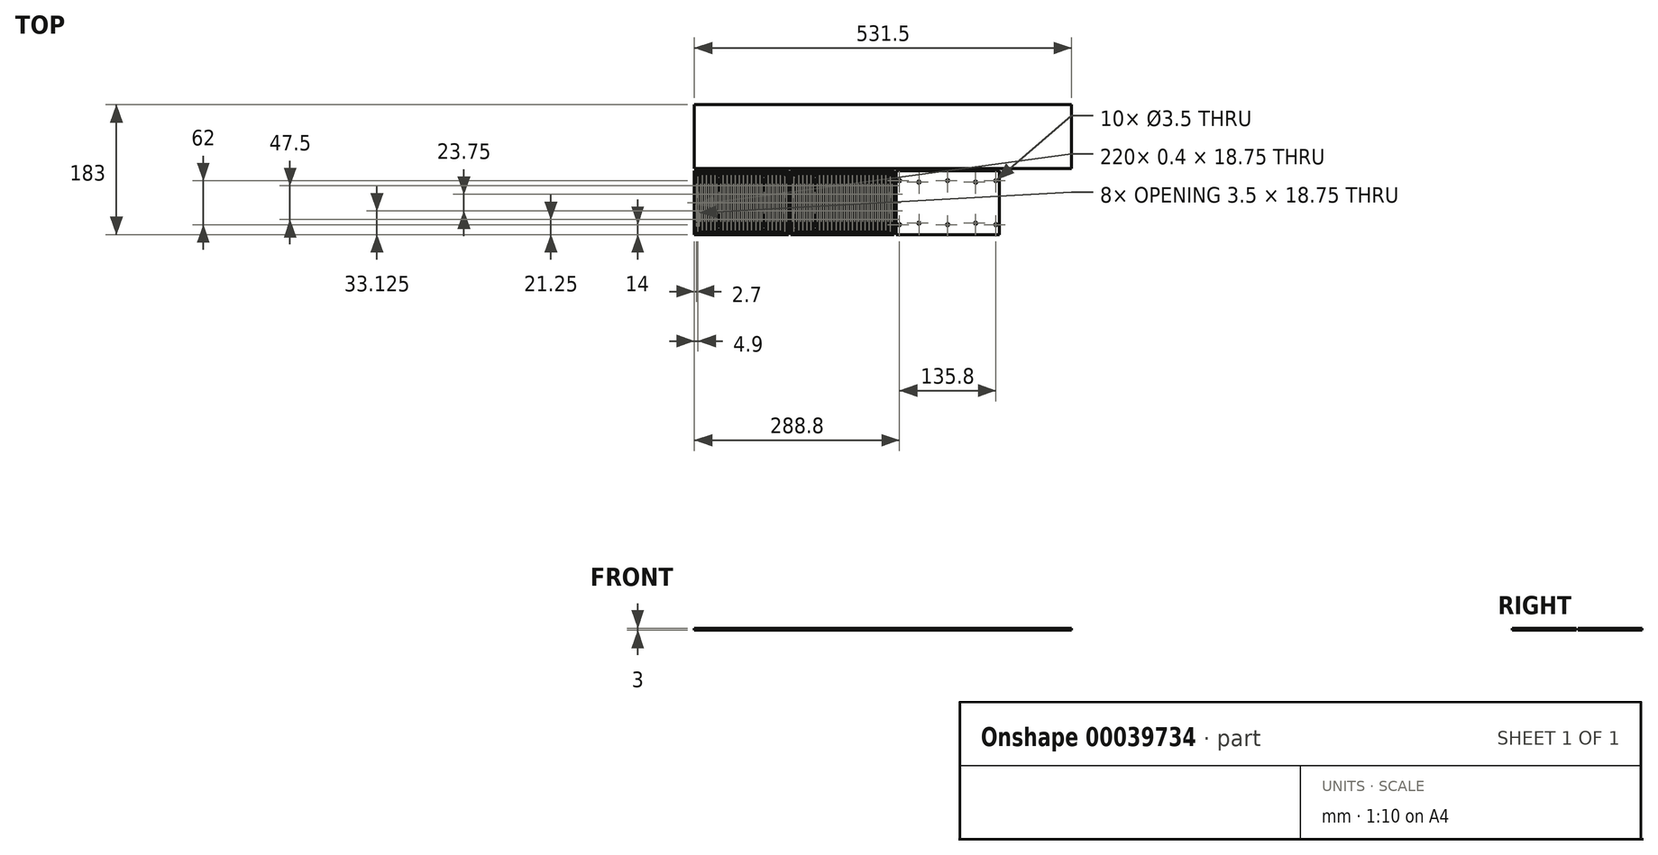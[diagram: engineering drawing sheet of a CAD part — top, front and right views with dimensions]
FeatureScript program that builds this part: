
annotation { "Feature Type Name" : "Feature", "Feature Type Description" : "" }
export const myFeature = defineFeature(function(context is Context, id is Id, definition is map)
    precondition{}
    {
        {
            var Q0;
            Q0=qCreatedBy(makeId("Top.planeOp"),FACE);
            var sketch = newSketch(context, id + "F0", { "sketchPlane" : qUnion([Q0])});
            skLineSegment(sketch, "E0.bottom", {"start": v(0, 0) * mm, "end": v(531.5, 0) * mm});
            skLineSegment(sketch, "E0.top", {"start": v(0, -90) * mm, "end": v(531.5, -90) * mm});
            skLineSegment(sketch, "E0.left", {"start": v(0, 0) * mm, "end": v(0, -90) * mm});
            skLineSegment(sketch, "E0.right", {"start": v(531.5, 0) * mm, "end": v(531.5, -90) * mm});
            skLineSegment(sketch, "E1.bottom", {"start": v(0, -93) * mm, "end": v(132.3, -93) * mm});
            skLineSegment(sketch, "E1.top", {"start": v(0, -183) * mm, "end": v(132.3, -183) * mm});
            skLineSegment(sketch, "E1.left", {"start": v(0, -93) * mm, "end": v(0, -183) * mm});
            skLineSegment(sketch, "E1.right", {"start": v(132.3, -93) * mm, "end": v(132.3, -183) * mm});
            skLineSegment(sketch, "E2.bottom", {"start": v(135.3, -93) * mm, "end": v(280.9, -93) * mm});
            skLineSegment(sketch, "E2.top", {"start": v(135.3, -183) * mm, "end": v(280.9, -183) * mm});
            skLineSegment(sketch, "E2.left", {"start": v(135.3, -93) * mm, "end": v(135.3, -183) * mm});
            skLineSegment(sketch, "E2.right", {"start": v(280.9, -93) * mm, "end": v(280.9, -183) * mm});
            skLineSegment(sketch, "E3", {"start": v(282.4, -93) * mm, "end": v(282.4, -183) * mm, "construction": true});
            skLineSegment(sketch, "E4.bottom", {"start": v(32.85, -109) * mm, "end": v(99.45, -109) * mm, "construction": true});
            skLineSegment(sketch, "E4.top", {"start": v(32.85, -167) * mm, "end": v(99.45, -167) * mm, "construction": true});
            skLineSegment(sketch, "E4.left", {"start": v(32.85, -109) * mm, "end": v(32.85, -167) * mm, "construction": true});
            skLineSegment(sketch, "E4.right", {"start": v(99.45, -109) * mm, "end": v(99.45, -167) * mm, "construction": true});
            skLineSegment(sketch, "E5.bottom", {"start": v(168.65, -109) * mm, "end": v(248.55, -109) * mm, "construction": true});
            skLineSegment(sketch, "E5.top", {"start": v(168.65, -167) * mm, "end": v(248.55, -167) * mm, "construction": true});
            skLineSegment(sketch, "E5.left", {"start": v(168.65, -109) * mm, "end": v(168.65, -167) * mm, "construction": true});
            skLineSegment(sketch, "E5.right", {"start": v(248.55, -109) * mm, "end": v(248.55, -167) * mm, "construction": true});
            skLineSegment(sketch, "E6", {"start": v(66.15, -93) * mm, "end": v(66.15, -183) * mm, "construction": true});
            skLineSegment(sketch, "E7", {"start": v(208.1, -93) * mm, "end": v(208.1, -183) * mm, "construction": true});
            skLineSegment(sketch, "E8", {"start": v(280.9, -138) * mm, "end": v(0, -138) * mm, "construction": true});
            skLineSegment(sketch, "E9.MirrorCS", {"start": v(283.9, -93) * mm, "end": v(283.9, -183) * mm});
            skLineSegment(sketch, "E10.MirrorCS", {"start": v(429.5, -93) * mm, "end": v(283.9, -93) * mm});
            skLineSegment(sketch, "E11.MirrorCS", {"start": v(429.5, -93) * mm, "end": v(429.5, -183) * mm});
            skLineSegment(sketch, "E12.MirrorCS", {"start": v(429.5, -183) * mm, "end": v(283.9, -183) * mm});
            skLineSegment(sketch, "E13.MirrorCS", {"start": v(396.15, -109) * mm, "end": v(316.25, -109) * mm, "construction": true});
            skLineSegment(sketch, "E14.MirrorCS", {"start": v(396.15, -109) * mm, "end": v(396.15, -167) * mm, "construction": true});
            skLineSegment(sketch, "E15.MirrorCS", {"start": v(396.15, -167) * mm, "end": v(316.25, -167) * mm, "construction": true});
            skLineSegment(sketch, "E16.MirrorCS", {"start": v(316.25, -109) * mm, "end": v(316.25, -167) * mm, "construction": true});
            skSolve(sketch);
        }
        {
            var Q0;
            Q0=makeQuery(id+"F0.imprint","IMPRINT",FACE,{"disambiguationData":[TD([[makeQuery(id+"F0.imprint","IMPRINT",EDGE,{"derivedFrom":sQuery(id+"F0.wireOp",EDGE,"E1.bottom")}),-1.0]])]});
            var Q1;
            Q1=makeQuery(id+"F0.imprint","IMPRINT",FACE,{"disambiguationData":[TD([[makeQuery(id+"F0.imprint","IMPRINT",EDGE,{"derivedFrom":sQuery(id+"F0.wireOp",EDGE,"E0.bottom")}),-1.0]])]});
            var Q2;
            Q2=makeQuery(id+"F0.imprint","IMPRINT",FACE,{"disambiguationData":[TD([[makeQuery(id+"F0.imprint","IMPRINT",EDGE,{"derivedFrom":sQuery(id+"F0.wireOp",EDGE,"E2.bottom")}),-1.0]])]});
            var Q3;
            Q3=makeQuery(id+"F0.imprint","IMPRINT",FACE,{"disambiguationData":[TD([[makeQuery(id+"F0.imprint","IMPRINT",EDGE,{"derivedFrom":sQuery(id+"F0.wireOp",EDGE,"E9.MirrorCS")}),1.0]])]});
            extrude(context, id + "F1", {"entities" : qUnion([Q0, Q1, Q2, Q3]), "depth" : 3 * mm});
        }
        {
            var Q0;
            Q0=makeQuery(id+"F1.opExtrude","CAP_FACE",FACE,{"disambiguationData":[OSD([sQuery(id+"F0.wireOp",EDGE,"E1.bottom"),sQuery(id+"F0.wireOp",EDGE,"E1.top"),sQuery(id+"F0.wireOp",EDGE,"E1.left"),sQuery(id+"F0.wireOp",EDGE,"E1.right")])],"isStart":false});
            var sketch = newSketch(context, id + "F2", { "sketchPlane" : qUnion([Q0])});
            skPoint(sketch, "E17.MirrorP", {"position": v(356.7, -183) * mm});
            skLineSegment(sketch, "E18.right", {"start": v(137.8, -183) * mm, "end": v(137.8, -93) * mm, "construction": true});
            skLineSegment(sketch, "E18.left", {"start": v(141.1, -183) * mm, "end": v(141.1, -93) * mm, "construction": true});
            skLineSegment(sketch, "E19.left", {"start": v(137.8, -164.25) * mm, "end": v(137.8, -183) * mm});
            skLineSegment(sketch, "E20.left", {"start": v(140.7, -176.12) * mm, "end": v(140.7, -183) * mm});
            skLineSegment(sketch, "E20.right", {"start": v(141.1, -176.12) * mm, "end": v(141.1, -183) * mm});
            skLineSegment(sketch, "E21.left", {"start": v(140.7, -152.37) * mm, "end": v(140.7, -171.12) * mm});
            skLineSegment(sketch, "E21.right", {"start": v(141.1, -152.37) * mm, "end": v(141.1, -171.12) * mm});
            skLineSegment(sketch, "E22.left", {"start": v(137.8, -140.5) * mm, "end": v(137.8, -159.25) * mm});
            skLineSegment(sketch, "E23.left", {"start": v(140.7, -128.62) * mm, "end": v(140.7, -147.37) * mm});
            skLineSegment(sketch, "E23.right", {"start": v(141.1, -128.62) * mm, "end": v(141.1, -147.37) * mm});
            skLineSegment(sketch, "E24.left", {"start": v(137.8, -116.75) * mm, "end": v(137.8, -135.5) * mm});
            skLineSegment(sketch, "E25.left", {"start": v(140.7, -104.87) * mm, "end": v(140.7, -123.62) * mm});
            skLineSegment(sketch, "E25.right", {"start": v(141.1, -104.87) * mm, "end": v(141.1, -123.62) * mm});
            skLineSegment(sketch, "E26.right", {"start": v(138.2, -93) * mm, "end": v(138.2, -111.75) * mm});
            skLineSegment(sketch, "E26.left", {"start": v(137.8, -93) * mm, "end": v(137.8, -111.75) * mm});
            skLineSegment(sketch, "E27.left", {"start": v(140.7, -99.87) * mm, "end": v(140.7, -93) * mm});
            skLineSegment(sketch, "E27.right", {"start": v(141.1, -99.87) * mm, "end": v(141.1, -93) * mm});
            skLineSegment(sketch, "E20.bottom", {"start": v(140.7, -176.12) * mm, "end": v(141.1, -176.12) * mm});
            skLineSegment(sketch, "E21.top", {"start": v(140.7, -171.12) * mm, "end": v(141.1, -171.12) * mm});
            skLineSegment(sketch, "E21.bottom", {"start": v(140.7, -152.37) * mm, "end": v(141.1, -152.37) * mm});
            skLineSegment(sketch, "E23.top", {"start": v(140.7, -147.37) * mm, "end": v(141.1, -147.37) * mm});
            skLineSegment(sketch, "E23.bottom", {"start": v(140.7, -128.62) * mm, "end": v(141.1, -128.62) * mm});
            skLineSegment(sketch, "E25.top", {"start": v(140.7, -123.62) * mm, "end": v(141.1, -123.62) * mm});
            skLineSegment(sketch, "E25.bottom", {"start": v(140.7, -104.87) * mm, "end": v(141.1, -104.87) * mm});
            skLineSegment(sketch, "E27.bottom", {"start": v(140.7, -99.87) * mm, "end": v(141.1, -99.87) * mm});
            skLineSegment(sketch, "E18.top", {"start": v(141.1, -93) * mm, "end": v(137.8, -93) * mm, "construction": true});
            skLineSegment(sketch, "E27.top", {"start": v(140.7, -93) * mm, "end": v(141.1, -93) * mm});
            skLineSegment(sketch, "E18.bottom", {"start": v(141.1, -183) * mm, "end": v(137.8, -183) * mm, "construction": true});
            skLineSegment(sketch, "E20.top", {"start": v(140.7, -183) * mm, "end": v(141.1, -183) * mm});
            skLineSegment(sketch, "E28", {"start": v(137.8, -111.75) * mm, "end": v(138.2, -111.75) * mm});
            skLineSegment(sketch, "E29.bottom", {"start": v(137.8, -116.75) * mm, "end": v(138.2, -116.75) * mm});
            skLineSegment(sketch, "E29.top", {"start": v(137.8, -135.5) * mm, "end": v(138.2, -135.5) * mm});
            skLineSegment(sketch, "E29.right", {"start": v(138.2, -116.75) * mm, "end": v(138.2, -135.5) * mm});
            skLineSegment(sketch, "E30.bottom", {"start": v(137.8, -159.25) * mm, "end": v(138.2, -159.25) * mm});
            skLineSegment(sketch, "E30.top", {"start": v(137.8, -140.5) * mm, "end": v(138.2, -140.5) * mm});
            skLineSegment(sketch, "E30.left", {"start": v(137.8, -159.25) * mm, "end": v(137.8, -140.5) * mm});
            skLineSegment(sketch, "E30.right", {"start": v(138.2, -159.25) * mm, "end": v(138.2, -140.5) * mm});
            skLineSegment(sketch, "E31.bottom", {"start": v(137.8, -164.25) * mm, "end": v(138.2, -164.25) * mm});
            skLineSegment(sketch, "E31.top", {"start": v(137.8, -183) * mm, "end": v(138.2, -183) * mm});
            skLineSegment(sketch, "E31.right", {"start": v(138.2, -164.25) * mm, "end": v(138.2, -183) * mm});
            skLineSegment(sketch, "E32.bottom", {"start": v(138.2, -111.75) * mm, "end": v(137.8, -111.75) * mm});
            skLineSegment(sketch, "E32.top", {"start": v(138.2, -93) * mm, "end": v(137.8, -93) * mm});
            skLineSegment(sketch, "E32.left", {"start": v(138.2, -111.75) * mm, "end": v(138.2, -93) * mm});
            skLineSegment(sketch, "E32.right", {"start": v(137.8, -111.75) * mm, "end": v(137.8, -93) * mm});
            skLineSegment(sketch, "E33.1.0.0", {"start": v(146.55, -99.87) * mm, "end": v(146.55, -93) * mm});
            skLineSegment(sketch, "E33.1.0.1", {"start": v(143.65, -183) * mm, "end": v(143.65, -93) * mm, "construction": true});
            skLineSegment(sketch, "E33.1.0.2", {"start": v(146.95, -152.37) * mm, "end": v(146.95, -171.12) * mm});
            skLineSegment(sketch, "E33.1.0.3", {"start": v(146.55, -104.87) * mm, "end": v(146.55, -123.62) * mm});
            skLineSegment(sketch, "E33.1.0.4", {"start": v(144.05, -159.25) * mm, "end": v(144.05, -140.5) * mm});
            skLineSegment(sketch, "E33.1.0.5", {"start": v(146.95, -128.62) * mm, "end": v(146.95, -147.37) * mm});
            skLineSegment(sketch, "E33.1.0.6", {"start": v(146.55, -128.62) * mm, "end": v(146.55, -147.37) * mm});
            skLineSegment(sketch, "E33.1.0.7", {"start": v(143.65, -164.25) * mm, "end": v(143.65, -183) * mm});
            skLineSegment(sketch, "E33.1.0.8", {"start": v(144.05, -164.25) * mm, "end": v(144.05, -183) * mm});
            skLineSegment(sketch, "E33.1.0.9", {"start": v(146.55, -176.12) * mm, "end": v(146.55, -183) * mm});
            skLineSegment(sketch, "E33.1.0.10", {"start": v(146.95, -176.12) * mm, "end": v(146.95, -183) * mm});
            skLineSegment(sketch, "E33.1.0.11", {"start": v(146.95, -183) * mm, "end": v(146.95, -93) * mm, "construction": true});
            skLineSegment(sketch, "E33.1.0.12", {"start": v(146.55, -152.37) * mm, "end": v(146.55, -171.12) * mm});
            skLineSegment(sketch, "E33.1.0.13", {"start": v(143.65, -140.5) * mm, "end": v(143.65, -159.25) * mm});
            skLineSegment(sketch, "E33.1.0.14", {"start": v(143.65, -116.75) * mm, "end": v(143.65, -135.5) * mm});
            skLineSegment(sketch, "E33.1.0.15", {"start": v(144.05, -116.75) * mm, "end": v(144.05, -135.5) * mm});
            skLineSegment(sketch, "E33.1.0.16", {"start": v(146.95, -104.87) * mm, "end": v(146.95, -123.62) * mm});
            skLineSegment(sketch, "E33.1.0.17", {"start": v(143.65, -93) * mm, "end": v(143.65, -111.75) * mm});
            skLineSegment(sketch, "E33.1.0.18", {"start": v(144.05, -93) * mm, "end": v(144.05, -111.75) * mm});
            skLineSegment(sketch, "E33.1.0.19", {"start": v(146.95, -99.87) * mm, "end": v(146.95, -93) * mm});
            skLineSegment(sketch, "E33.1.0.20", {"start": v(143.65, -159.25) * mm, "end": v(143.65, -140.5) * mm});
            skLineSegment(sketch, "E33.1.0.21", {"start": v(143.65, -116.75) * mm, "end": v(143.65, -135.5) * mm});
            skLineSegment(sketch, "E33.1.0.22", {"start": v(144.05, -111.75) * mm, "end": v(144.05, -93) * mm});
            skLineSegment(sketch, "E33.1.0.23", {"start": v(143.65, -164.25) * mm, "end": v(143.65, -183) * mm});
            skLineSegment(sketch, "E33.1.0.24", {"start": v(143.65, -111.75) * mm, "end": v(143.65, -93) * mm});
            skLineSegment(sketch, "E33.1.0.25", {"start": v(146.55, -176.12) * mm, "end": v(146.95, -176.12) * mm});
            skLineSegment(sketch, "E33.1.0.26", {"start": v(146.55, -171.12) * mm, "end": v(146.95, -171.12) * mm});
            skLineSegment(sketch, "E33.1.0.27", {"start": v(146.55, -152.37) * mm, "end": v(146.95, -152.37) * mm});
            skLineSegment(sketch, "E33.1.0.28", {"start": v(146.55, -147.37) * mm, "end": v(146.95, -147.37) * mm});
            skLineSegment(sketch, "E33.1.0.29", {"start": v(146.55, -128.62) * mm, "end": v(146.95, -128.62) * mm});
            skLineSegment(sketch, "E33.1.0.30", {"start": v(146.55, -123.62) * mm, "end": v(146.95, -123.62) * mm});
            skLineSegment(sketch, "E33.1.0.31", {"start": v(146.55, -104.87) * mm, "end": v(146.95, -104.87) * mm});
            skLineSegment(sketch, "E33.1.0.32", {"start": v(146.55, -99.87) * mm, "end": v(146.95, -99.87) * mm});
            skLineSegment(sketch, "E33.1.0.33", {"start": v(143.65, -164.25) * mm, "end": v(144.05, -164.25) * mm});
            skLineSegment(sketch, "E33.1.0.34", {"start": v(143.65, -159.25) * mm, "end": v(144.05, -159.25) * mm});
            skLineSegment(sketch, "E33.1.0.35", {"start": v(146.95, -93) * mm, "end": v(143.65, -93) * mm, "construction": true});
            skLineSegment(sketch, "E33.1.0.36", {"start": v(143.65, -140.5) * mm, "end": v(144.05, -140.5) * mm});
            skLineSegment(sketch, "E33.1.0.37", {"start": v(143.65, -135.5) * mm, "end": v(144.05, -135.5) * mm});
            skLineSegment(sketch, "E33.1.0.38", {"start": v(143.65, -116.75) * mm, "end": v(144.05, -116.75) * mm});
            skLineSegment(sketch, "E33.1.0.39", {"start": v(146.55, -183) * mm, "end": v(146.95, -183) * mm});
            skLineSegment(sketch, "E33.1.0.40", {"start": v(146.55, -93) * mm, "end": v(146.95, -93) * mm});
            skLineSegment(sketch, "E33.1.0.41", {"start": v(146.95, -183) * mm, "end": v(143.65, -183) * mm, "construction": true});
            skLineSegment(sketch, "E33.1.0.42", {"start": v(144.05, -111.75) * mm, "end": v(143.65, -111.75) * mm});
            skLineSegment(sketch, "E33.1.0.43", {"start": v(143.65, -183) * mm, "end": v(144.05, -183) * mm});
            skLineSegment(sketch, "E33.1.0.44", {"start": v(143.65, -111.75) * mm, "end": v(144.05, -111.75) * mm});
            skLineSegment(sketch, "E33.1.0.45", {"start": v(144.05, -93) * mm, "end": v(143.65, -93) * mm});
            skLineSegment(sketch, "E33.2.0.0", {"start": v(152.4, -99.87) * mm, "end": v(152.4, -93) * mm});
            skLineSegment(sketch, "E33.2.0.1", {"start": v(149.5, -183) * mm, "end": v(149.5, -93) * mm, "construction": true});
            skLineSegment(sketch, "E33.2.0.2", {"start": v(152.8, -152.37) * mm, "end": v(152.8, -171.12) * mm});
            skLineSegment(sketch, "E33.2.0.3", {"start": v(152.4, -104.87) * mm, "end": v(152.4, -123.62) * mm});
            skLineSegment(sketch, "E33.2.0.4", {"start": v(149.9, -159.25) * mm, "end": v(149.9, -140.5) * mm});
            skLineSegment(sketch, "E33.2.0.5", {"start": v(152.8, -128.62) * mm, "end": v(152.8, -147.37) * mm});
            skLineSegment(sketch, "E33.2.0.6", {"start": v(152.4, -128.62) * mm, "end": v(152.4, -147.37) * mm});
            skLineSegment(sketch, "E33.2.0.7", {"start": v(149.5, -164.25) * mm, "end": v(149.5, -183) * mm});
            skLineSegment(sketch, "E33.2.0.8", {"start": v(149.9, -164.25) * mm, "end": v(149.9, -183) * mm});
            skLineSegment(sketch, "E33.2.0.9", {"start": v(152.4, -176.12) * mm, "end": v(152.4, -183) * mm});
            skLineSegment(sketch, "E33.2.0.10", {"start": v(152.8, -176.12) * mm, "end": v(152.8, -183) * mm});
            skLineSegment(sketch, "E33.2.0.11", {"start": v(152.8, -183) * mm, "end": v(152.8, -93) * mm, "construction": true});
            skLineSegment(sketch, "E33.2.0.12", {"start": v(152.4, -152.37) * mm, "end": v(152.4, -171.12) * mm});
            skLineSegment(sketch, "E33.2.0.13", {"start": v(149.5, -140.5) * mm, "end": v(149.5, -159.25) * mm});
            skLineSegment(sketch, "E33.2.0.14", {"start": v(149.5, -116.75) * mm, "end": v(149.5, -135.5) * mm});
            skLineSegment(sketch, "E33.2.0.15", {"start": v(149.9, -116.75) * mm, "end": v(149.9, -135.5) * mm});
            skLineSegment(sketch, "E33.2.0.16", {"start": v(152.8, -104.87) * mm, "end": v(152.8, -123.62) * mm});
            skLineSegment(sketch, "E33.2.0.17", {"start": v(149.5, -93) * mm, "end": v(149.5, -111.75) * mm});
            skLineSegment(sketch, "E33.2.0.18", {"start": v(149.9, -93) * mm, "end": v(149.9, -111.75) * mm});
            skLineSegment(sketch, "E33.2.0.19", {"start": v(152.8, -99.87) * mm, "end": v(152.8, -93) * mm});
            skLineSegment(sketch, "E33.2.0.20", {"start": v(149.5, -159.25) * mm, "end": v(149.5, -140.5) * mm});
            skLineSegment(sketch, "E33.2.0.21", {"start": v(149.5, -116.75) * mm, "end": v(149.5, -135.5) * mm});
            skLineSegment(sketch, "E33.2.0.22", {"start": v(149.9, -111.75) * mm, "end": v(149.9, -93) * mm});
            skLineSegment(sketch, "E33.2.0.23", {"start": v(149.5, -164.25) * mm, "end": v(149.5, -183) * mm});
            skLineSegment(sketch, "E33.2.0.24", {"start": v(149.5, -111.75) * mm, "end": v(149.5, -93) * mm});
            skLineSegment(sketch, "E33.2.0.25", {"start": v(152.4, -176.12) * mm, "end": v(152.8, -176.12) * mm});
            skLineSegment(sketch, "E33.2.0.26", {"start": v(152.4, -171.12) * mm, "end": v(152.8, -171.12) * mm});
            skLineSegment(sketch, "E33.2.0.27", {"start": v(152.4, -152.37) * mm, "end": v(152.8, -152.37) * mm});
            skLineSegment(sketch, "E33.2.0.28", {"start": v(152.4, -147.37) * mm, "end": v(152.8, -147.37) * mm});
            skLineSegment(sketch, "E33.2.0.29", {"start": v(152.4, -128.62) * mm, "end": v(152.8, -128.62) * mm});
            skLineSegment(sketch, "E33.2.0.30", {"start": v(152.4, -123.62) * mm, "end": v(152.8, -123.62) * mm});
            skLineSegment(sketch, "E33.2.0.31", {"start": v(152.4, -104.87) * mm, "end": v(152.8, -104.87) * mm});
            skLineSegment(sketch, "E33.2.0.32", {"start": v(152.4, -99.87) * mm, "end": v(152.8, -99.87) * mm});
            skLineSegment(sketch, "E33.2.0.33", {"start": v(149.5, -164.25) * mm, "end": v(149.9, -164.25) * mm});
            skLineSegment(sketch, "E33.2.0.34", {"start": v(149.5, -159.25) * mm, "end": v(149.9, -159.25) * mm});
            skLineSegment(sketch, "E33.2.0.35", {"start": v(152.8, -93) * mm, "end": v(149.5, -93) * mm, "construction": true});
            skLineSegment(sketch, "E33.2.0.36", {"start": v(149.5, -140.5) * mm, "end": v(149.9, -140.5) * mm});
            skLineSegment(sketch, "E33.2.0.37", {"start": v(149.5, -135.5) * mm, "end": v(149.9, -135.5) * mm});
            skLineSegment(sketch, "E33.2.0.38", {"start": v(149.5, -116.75) * mm, "end": v(149.9, -116.75) * mm});
            skLineSegment(sketch, "E33.2.0.39", {"start": v(152.4, -183) * mm, "end": v(152.8, -183) * mm});
            skLineSegment(sketch, "E33.2.0.40", {"start": v(152.4, -93) * mm, "end": v(152.8, -93) * mm});
            skLineSegment(sketch, "E33.2.0.41", {"start": v(152.8, -183) * mm, "end": v(149.5, -183) * mm, "construction": true});
            skLineSegment(sketch, "E33.2.0.42", {"start": v(149.9, -111.75) * mm, "end": v(149.5, -111.75) * mm});
            skLineSegment(sketch, "E33.2.0.43", {"start": v(149.5, -183) * mm, "end": v(149.9, -183) * mm});
            skLineSegment(sketch, "E33.2.0.44", {"start": v(149.5, -111.75) * mm, "end": v(149.9, -111.75) * mm});
            skLineSegment(sketch, "E33.2.0.45", {"start": v(149.9, -93) * mm, "end": v(149.5, -93) * mm});
            skLineSegment(sketch, "E33.3.0.0", {"start": v(158.25, -99.87) * mm, "end": v(158.25, -93) * mm});
            skLineSegment(sketch, "E33.3.0.1", {"start": v(155.35, -183) * mm, "end": v(155.35, -93) * mm, "construction": true});
            skLineSegment(sketch, "E33.3.0.2", {"start": v(158.65, -152.37) * mm, "end": v(158.65, -171.12) * mm});
            skLineSegment(sketch, "E33.3.0.3", {"start": v(158.25, -104.87) * mm, "end": v(158.25, -123.62) * mm});
            skLineSegment(sketch, "E33.3.0.4", {"start": v(155.75, -159.25) * mm, "end": v(155.75, -140.5) * mm});
            skLineSegment(sketch, "E33.3.0.5", {"start": v(158.65, -128.62) * mm, "end": v(158.65, -147.37) * mm});
            skLineSegment(sketch, "E33.3.0.6", {"start": v(158.25, -128.62) * mm, "end": v(158.25, -147.37) * mm});
            skLineSegment(sketch, "E33.3.0.7", {"start": v(155.35, -164.25) * mm, "end": v(155.35, -183) * mm});
            skLineSegment(sketch, "E33.3.0.8", {"start": v(155.75, -164.25) * mm, "end": v(155.75, -183) * mm});
            skLineSegment(sketch, "E33.3.0.9", {"start": v(158.25, -176.12) * mm, "end": v(158.25, -183) * mm});
            skLineSegment(sketch, "E33.3.0.10", {"start": v(158.65, -176.12) * mm, "end": v(158.65, -183) * mm});
            skLineSegment(sketch, "E33.3.0.11", {"start": v(158.65, -183) * mm, "end": v(158.65, -93) * mm, "construction": true});
            skLineSegment(sketch, "E33.3.0.12", {"start": v(158.25, -152.37) * mm, "end": v(158.25, -171.12) * mm});
            skLineSegment(sketch, "E33.3.0.13", {"start": v(155.35, -140.5) * mm, "end": v(155.35, -159.25) * mm});
            skLineSegment(sketch, "E33.3.0.14", {"start": v(155.35, -116.75) * mm, "end": v(155.35, -135.5) * mm});
            skLineSegment(sketch, "E33.3.0.15", {"start": v(155.75, -116.75) * mm, "end": v(155.75, -135.5) * mm});
            skLineSegment(sketch, "E33.3.0.16", {"start": v(158.65, -104.87) * mm, "end": v(158.65, -123.62) * mm});
            skLineSegment(sketch, "E33.3.0.17", {"start": v(155.35, -93) * mm, "end": v(155.35, -111.75) * mm});
            skLineSegment(sketch, "E33.3.0.18", {"start": v(155.75, -93) * mm, "end": v(155.75, -111.75) * mm});
            skLineSegment(sketch, "E33.3.0.19", {"start": v(158.65, -99.87) * mm, "end": v(158.65, -93) * mm});
            skLineSegment(sketch, "E33.3.0.20", {"start": v(155.35, -159.25) * mm, "end": v(155.35, -140.5) * mm});
            skLineSegment(sketch, "E33.3.0.21", {"start": v(155.35, -116.75) * mm, "end": v(155.35, -135.5) * mm});
            skLineSegment(sketch, "E33.3.0.22", {"start": v(155.75, -111.75) * mm, "end": v(155.75, -93) * mm});
            skLineSegment(sketch, "E33.3.0.23", {"start": v(155.35, -164.25) * mm, "end": v(155.35, -183) * mm});
            skLineSegment(sketch, "E33.3.0.24", {"start": v(155.35, -111.75) * mm, "end": v(155.35, -93) * mm});
            skLineSegment(sketch, "E33.3.0.25", {"start": v(158.25, -176.12) * mm, "end": v(158.65, -176.12) * mm});
            skLineSegment(sketch, "E33.3.0.26", {"start": v(158.25, -171.12) * mm, "end": v(158.65, -171.12) * mm});
            skLineSegment(sketch, "E33.3.0.27", {"start": v(158.25, -152.37) * mm, "end": v(158.65, -152.37) * mm});
            skLineSegment(sketch, "E33.3.0.28", {"start": v(158.25, -147.37) * mm, "end": v(158.65, -147.37) * mm});
            skLineSegment(sketch, "E33.3.0.29", {"start": v(158.25, -128.62) * mm, "end": v(158.65, -128.62) * mm});
            skLineSegment(sketch, "E33.3.0.30", {"start": v(158.25, -123.62) * mm, "end": v(158.65, -123.62) * mm});
            skLineSegment(sketch, "E33.3.0.31", {"start": v(158.25, -104.87) * mm, "end": v(158.65, -104.87) * mm});
            skLineSegment(sketch, "E33.3.0.32", {"start": v(158.25, -99.87) * mm, "end": v(158.65, -99.87) * mm});
            skLineSegment(sketch, "E33.3.0.33", {"start": v(155.35, -164.25) * mm, "end": v(155.75, -164.25) * mm});
            skLineSegment(sketch, "E33.3.0.34", {"start": v(155.35, -159.25) * mm, "end": v(155.75, -159.25) * mm});
            skLineSegment(sketch, "E33.3.0.35", {"start": v(158.65, -93) * mm, "end": v(155.35, -93) * mm, "construction": true});
            skLineSegment(sketch, "E33.3.0.36", {"start": v(155.35, -140.5) * mm, "end": v(155.75, -140.5) * mm});
            skLineSegment(sketch, "E33.3.0.37", {"start": v(155.35, -135.5) * mm, "end": v(155.75, -135.5) * mm});
            skLineSegment(sketch, "E33.3.0.38", {"start": v(155.35, -116.75) * mm, "end": v(155.75, -116.75) * mm});
            skLineSegment(sketch, "E33.3.0.39", {"start": v(158.25, -183) * mm, "end": v(158.65, -183) * mm});
            skLineSegment(sketch, "E33.3.0.40", {"start": v(158.25, -93) * mm, "end": v(158.65, -93) * mm});
            skLineSegment(sketch, "E33.3.0.41", {"start": v(158.65, -183) * mm, "end": v(155.35, -183) * mm, "construction": true});
            skLineSegment(sketch, "E33.3.0.42", {"start": v(155.75, -111.75) * mm, "end": v(155.35, -111.75) * mm});
            skLineSegment(sketch, "E33.3.0.43", {"start": v(155.35, -183) * mm, "end": v(155.75, -183) * mm});
            skLineSegment(sketch, "E33.3.0.44", {"start": v(155.35, -111.75) * mm, "end": v(155.75, -111.75) * mm});
            skLineSegment(sketch, "E33.3.0.45", {"start": v(155.75, -93) * mm, "end": v(155.35, -93) * mm});
            skLineSegment(sketch, "E33.4.0.0", {"start": v(164.1, -99.87) * mm, "end": v(164.1, -93) * mm});
            skLineSegment(sketch, "E33.4.0.1", {"start": v(161.2, -183) * mm, "end": v(161.2, -93) * mm, "construction": true});
            skLineSegment(sketch, "E33.4.0.2", {"start": v(164.5, -152.37) * mm, "end": v(164.5, -171.12) * mm});
            skLineSegment(sketch, "E33.4.0.3", {"start": v(164.1, -104.87) * mm, "end": v(164.1, -123.62) * mm});
            skLineSegment(sketch, "E33.4.0.4", {"start": v(161.6, -159.25) * mm, "end": v(161.6, -140.5) * mm});
            skLineSegment(sketch, "E33.4.0.5", {"start": v(164.5, -128.62) * mm, "end": v(164.5, -147.37) * mm});
            skLineSegment(sketch, "E33.4.0.6", {"start": v(164.1, -128.62) * mm, "end": v(164.1, -147.37) * mm});
            skLineSegment(sketch, "E33.4.0.7", {"start": v(161.2, -164.25) * mm, "end": v(161.2, -183) * mm});
            skLineSegment(sketch, "E33.4.0.8", {"start": v(161.6, -164.25) * mm, "end": v(161.6, -183) * mm});
            skLineSegment(sketch, "E33.4.0.9", {"start": v(164.1, -176.12) * mm, "end": v(164.1, -183) * mm});
            skLineSegment(sketch, "E33.4.0.10", {"start": v(164.5, -176.12) * mm, "end": v(164.5, -183) * mm});
            skLineSegment(sketch, "E33.4.0.11", {"start": v(164.5, -183) * mm, "end": v(164.5, -93) * mm, "construction": true});
            skLineSegment(sketch, "E33.4.0.12", {"start": v(164.1, -152.37) * mm, "end": v(164.1, -171.12) * mm});
            skLineSegment(sketch, "E33.4.0.13", {"start": v(161.2, -140.5) * mm, "end": v(161.2, -159.25) * mm});
            skLineSegment(sketch, "E33.4.0.14", {"start": v(161.2, -116.75) * mm, "end": v(161.2, -135.5) * mm});
            skLineSegment(sketch, "E33.4.0.15", {"start": v(161.6, -116.75) * mm, "end": v(161.6, -135.5) * mm});
            skLineSegment(sketch, "E33.4.0.16", {"start": v(164.5, -104.87) * mm, "end": v(164.5, -123.62) * mm});
            skLineSegment(sketch, "E33.4.0.17", {"start": v(161.2, -93) * mm, "end": v(161.2, -111.75) * mm});
            skLineSegment(sketch, "E33.4.0.18", {"start": v(161.6, -93) * mm, "end": v(161.6, -111.75) * mm});
            skLineSegment(sketch, "E33.4.0.19", {"start": v(164.5, -99.87) * mm, "end": v(164.5, -93) * mm});
            skLineSegment(sketch, "E33.4.0.20", {"start": v(161.2, -159.25) * mm, "end": v(161.2, -140.5) * mm});
            skLineSegment(sketch, "E33.4.0.21", {"start": v(161.2, -116.75) * mm, "end": v(161.2, -135.5) * mm});
            skLineSegment(sketch, "E33.4.0.22", {"start": v(161.6, -111.75) * mm, "end": v(161.6, -93) * mm});
            skLineSegment(sketch, "E33.4.0.23", {"start": v(161.2, -164.25) * mm, "end": v(161.2, -183) * mm});
            skLineSegment(sketch, "E33.4.0.24", {"start": v(161.2, -111.75) * mm, "end": v(161.2, -93) * mm});
            skLineSegment(sketch, "E33.4.0.25", {"start": v(164.1, -176.12) * mm, "end": v(164.5, -176.12) * mm});
            skLineSegment(sketch, "E33.4.0.26", {"start": v(164.1, -171.12) * mm, "end": v(164.5, -171.12) * mm});
            skLineSegment(sketch, "E33.4.0.27", {"start": v(164.1, -152.37) * mm, "end": v(164.5, -152.37) * mm});
            skLineSegment(sketch, "E33.4.0.28", {"start": v(164.1, -147.37) * mm, "end": v(164.5, -147.37) * mm});
            skLineSegment(sketch, "E33.4.0.29", {"start": v(164.1, -128.62) * mm, "end": v(164.5, -128.62) * mm});
            skLineSegment(sketch, "E33.4.0.30", {"start": v(164.1, -123.62) * mm, "end": v(164.5, -123.62) * mm});
            skLineSegment(sketch, "E33.4.0.31", {"start": v(164.1, -104.87) * mm, "end": v(164.5, -104.87) * mm});
            skLineSegment(sketch, "E33.4.0.32", {"start": v(164.1, -99.87) * mm, "end": v(164.5, -99.87) * mm});
            skLineSegment(sketch, "E33.4.0.33", {"start": v(161.2, -164.25) * mm, "end": v(161.6, -164.25) * mm});
            skLineSegment(sketch, "E33.4.0.34", {"start": v(161.2, -159.25) * mm, "end": v(161.6, -159.25) * mm});
            skLineSegment(sketch, "E33.4.0.35", {"start": v(164.5, -93) * mm, "end": v(161.2, -93) * mm, "construction": true});
            skLineSegment(sketch, "E33.4.0.36", {"start": v(161.2, -140.5) * mm, "end": v(161.6, -140.5) * mm});
            skLineSegment(sketch, "E33.4.0.37", {"start": v(161.2, -135.5) * mm, "end": v(161.6, -135.5) * mm});
            skLineSegment(sketch, "E33.4.0.38", {"start": v(161.2, -116.75) * mm, "end": v(161.6, -116.75) * mm});
            skLineSegment(sketch, "E33.4.0.39", {"start": v(164.1, -183) * mm, "end": v(164.5, -183) * mm});
            skLineSegment(sketch, "E33.4.0.40", {"start": v(164.1, -93) * mm, "end": v(164.5, -93) * mm});
            skLineSegment(sketch, "E33.4.0.41", {"start": v(164.5, -183) * mm, "end": v(161.2, -183) * mm, "construction": true});
            skLineSegment(sketch, "E33.4.0.42", {"start": v(161.6, -111.75) * mm, "end": v(161.2, -111.75) * mm});
            skLineSegment(sketch, "E33.4.0.43", {"start": v(161.2, -183) * mm, "end": v(161.6, -183) * mm});
            skLineSegment(sketch, "E33.4.0.44", {"start": v(161.2, -111.75) * mm, "end": v(161.6, -111.75) * mm});
            skLineSegment(sketch, "E33.4.0.45", {"start": v(161.6, -93) * mm, "end": v(161.2, -93) * mm});
            skLineSegment(sketch, "E33.5.0.0", {"start": v(169.95, -99.87) * mm, "end": v(169.95, -93) * mm});
            skLineSegment(sketch, "E33.5.0.1", {"start": v(167.05, -183) * mm, "end": v(167.05, -93) * mm, "construction": true});
            skLineSegment(sketch, "E33.5.0.2", {"start": v(170.35, -152.37) * mm, "end": v(170.35, -171.12) * mm});
            skLineSegment(sketch, "E33.5.0.3", {"start": v(169.95, -104.87) * mm, "end": v(169.95, -123.62) * mm});
            skLineSegment(sketch, "E33.5.0.4", {"start": v(167.45, -159.25) * mm, "end": v(167.45, -140.5) * mm});
            skLineSegment(sketch, "E33.5.0.5", {"start": v(170.35, -128.62) * mm, "end": v(170.35, -147.37) * mm});
            skLineSegment(sketch, "E33.5.0.6", {"start": v(169.95, -128.62) * mm, "end": v(169.95, -147.37) * mm});
            skLineSegment(sketch, "E33.5.0.7", {"start": v(167.05, -164.25) * mm, "end": v(167.05, -183) * mm});
            skLineSegment(sketch, "E33.5.0.8", {"start": v(167.45, -164.25) * mm, "end": v(167.45, -183) * mm});
            skLineSegment(sketch, "E33.5.0.9", {"start": v(169.95, -176.12) * mm, "end": v(169.95, -183) * mm});
            skLineSegment(sketch, "E33.5.0.10", {"start": v(170.35, -176.12) * mm, "end": v(170.35, -183) * mm});
            skLineSegment(sketch, "E33.5.0.11", {"start": v(170.35, -183) * mm, "end": v(170.35, -93) * mm, "construction": true});
            skLineSegment(sketch, "E33.5.0.12", {"start": v(169.95, -152.37) * mm, "end": v(169.95, -171.12) * mm});
            skLineSegment(sketch, "E33.5.0.13", {"start": v(167.05, -140.5) * mm, "end": v(167.05, -159.25) * mm});
            skLineSegment(sketch, "E33.5.0.14", {"start": v(167.05, -116.75) * mm, "end": v(167.05, -135.5) * mm});
            skLineSegment(sketch, "E33.5.0.15", {"start": v(167.45, -116.75) * mm, "end": v(167.45, -135.5) * mm});
            skLineSegment(sketch, "E33.5.0.16", {"start": v(170.35, -104.87) * mm, "end": v(170.35, -123.62) * mm});
            skLineSegment(sketch, "E33.5.0.17", {"start": v(167.05, -93) * mm, "end": v(167.05, -111.75) * mm});
            skLineSegment(sketch, "E33.5.0.18", {"start": v(167.45, -93) * mm, "end": v(167.45, -111.75) * mm});
            skLineSegment(sketch, "E33.5.0.19", {"start": v(170.35, -99.87) * mm, "end": v(170.35, -93) * mm});
            skLineSegment(sketch, "E33.5.0.20", {"start": v(167.05, -159.25) * mm, "end": v(167.05, -140.5) * mm});
            skLineSegment(sketch, "E33.5.0.21", {"start": v(167.05, -116.75) * mm, "end": v(167.05, -135.5) * mm});
            skLineSegment(sketch, "E33.5.0.22", {"start": v(167.45, -111.75) * mm, "end": v(167.45, -93) * mm});
            skLineSegment(sketch, "E33.5.0.23", {"start": v(167.05, -164.25) * mm, "end": v(167.05, -183) * mm});
            skLineSegment(sketch, "E33.5.0.24", {"start": v(167.05, -111.75) * mm, "end": v(167.05, -93) * mm});
            skLineSegment(sketch, "E33.5.0.25", {"start": v(169.95, -176.12) * mm, "end": v(170.35, -176.12) * mm});
            skLineSegment(sketch, "E33.5.0.26", {"start": v(169.95, -171.12) * mm, "end": v(170.35, -171.12) * mm});
            skLineSegment(sketch, "E33.5.0.27", {"start": v(169.95, -152.37) * mm, "end": v(170.35, -152.37) * mm});
            skLineSegment(sketch, "E33.5.0.28", {"start": v(169.95, -147.37) * mm, "end": v(170.35, -147.37) * mm});
            skLineSegment(sketch, "E33.5.0.29", {"start": v(169.95, -128.62) * mm, "end": v(170.35, -128.62) * mm});
            skLineSegment(sketch, "E33.5.0.30", {"start": v(169.95, -123.62) * mm, "end": v(170.35, -123.62) * mm});
            skLineSegment(sketch, "E33.5.0.31", {"start": v(169.95, -104.87) * mm, "end": v(170.35, -104.87) * mm});
            skLineSegment(sketch, "E33.5.0.32", {"start": v(169.95, -99.87) * mm, "end": v(170.35, -99.87) * mm});
            skLineSegment(sketch, "E33.5.0.33", {"start": v(167.05, -164.25) * mm, "end": v(167.45, -164.25) * mm});
            skLineSegment(sketch, "E33.5.0.34", {"start": v(167.05, -159.25) * mm, "end": v(167.45, -159.25) * mm});
            skLineSegment(sketch, "E33.5.0.35", {"start": v(170.35, -93) * mm, "end": v(167.05, -93) * mm, "construction": true});
            skLineSegment(sketch, "E33.5.0.36", {"start": v(167.05, -140.5) * mm, "end": v(167.45, -140.5) * mm});
            skLineSegment(sketch, "E33.5.0.37", {"start": v(167.05, -135.5) * mm, "end": v(167.45, -135.5) * mm});
            skLineSegment(sketch, "E33.5.0.38", {"start": v(167.05, -116.75) * mm, "end": v(167.45, -116.75) * mm});
            skLineSegment(sketch, "E33.5.0.39", {"start": v(169.95, -183) * mm, "end": v(170.35, -183) * mm});
            skLineSegment(sketch, "E33.5.0.40", {"start": v(169.95, -93) * mm, "end": v(170.35, -93) * mm});
            skLineSegment(sketch, "E33.5.0.41", {"start": v(170.35, -183) * mm, "end": v(167.05, -183) * mm, "construction": true});
            skLineSegment(sketch, "E33.5.0.42", {"start": v(167.45, -111.75) * mm, "end": v(167.05, -111.75) * mm});
            skLineSegment(sketch, "E33.5.0.43", {"start": v(167.05, -183) * mm, "end": v(167.45, -183) * mm});
            skLineSegment(sketch, "E33.5.0.44", {"start": v(167.05, -111.75) * mm, "end": v(167.45, -111.75) * mm});
            skLineSegment(sketch, "E33.5.0.45", {"start": v(167.45, -93) * mm, "end": v(167.05, -93) * mm});
            skLineSegment(sketch, "E33.6.0.0", {"start": v(175.8, -99.87) * mm, "end": v(175.8, -93) * mm});
            skLineSegment(sketch, "E33.6.0.1", {"start": v(172.9, -183) * mm, "end": v(172.9, -93) * mm, "construction": true});
            skLineSegment(sketch, "E33.6.0.2", {"start": v(176.2, -152.37) * mm, "end": v(176.2, -171.12) * mm});
            skLineSegment(sketch, "E33.6.0.3", {"start": v(175.8, -104.87) * mm, "end": v(175.8, -123.62) * mm});
            skLineSegment(sketch, "E33.6.0.4", {"start": v(173.3, -159.25) * mm, "end": v(173.3, -140.5) * mm});
            skLineSegment(sketch, "E33.6.0.5", {"start": v(176.2, -128.62) * mm, "end": v(176.2, -147.37) * mm});
            skLineSegment(sketch, "E33.6.0.6", {"start": v(175.8, -128.62) * mm, "end": v(175.8, -147.37) * mm});
            skLineSegment(sketch, "E33.6.0.7", {"start": v(172.9, -164.25) * mm, "end": v(172.9, -183) * mm});
            skLineSegment(sketch, "E33.6.0.8", {"start": v(173.3, -164.25) * mm, "end": v(173.3, -183) * mm});
            skLineSegment(sketch, "E33.6.0.9", {"start": v(175.8, -176.12) * mm, "end": v(175.8, -183) * mm});
            skLineSegment(sketch, "E33.6.0.10", {"start": v(176.2, -176.12) * mm, "end": v(176.2, -183) * mm});
            skLineSegment(sketch, "E33.6.0.11", {"start": v(176.2, -183) * mm, "end": v(176.2, -93) * mm, "construction": true});
            skLineSegment(sketch, "E33.6.0.12", {"start": v(175.8, -152.37) * mm, "end": v(175.8, -171.12) * mm});
            skLineSegment(sketch, "E33.6.0.13", {"start": v(172.9, -140.5) * mm, "end": v(172.9, -159.25) * mm});
            skLineSegment(sketch, "E33.6.0.14", {"start": v(172.9, -116.75) * mm, "end": v(172.9, -135.5) * mm});
            skLineSegment(sketch, "E33.6.0.15", {"start": v(173.3, -116.75) * mm, "end": v(173.3, -135.5) * mm});
            skLineSegment(sketch, "E33.6.0.16", {"start": v(176.2, -104.87) * mm, "end": v(176.2, -123.62) * mm});
            skLineSegment(sketch, "E33.6.0.17", {"start": v(172.9, -93) * mm, "end": v(172.9, -111.75) * mm});
            skLineSegment(sketch, "E33.6.0.18", {"start": v(173.3, -93) * mm, "end": v(173.3, -111.75) * mm});
            skLineSegment(sketch, "E33.6.0.19", {"start": v(176.2, -99.87) * mm, "end": v(176.2, -93) * mm});
            skLineSegment(sketch, "E33.6.0.20", {"start": v(172.9, -159.25) * mm, "end": v(172.9, -140.5) * mm});
            skLineSegment(sketch, "E33.6.0.21", {"start": v(172.9, -116.75) * mm, "end": v(172.9, -135.5) * mm});
            skLineSegment(sketch, "E33.6.0.22", {"start": v(173.3, -111.75) * mm, "end": v(173.3, -93) * mm});
            skLineSegment(sketch, "E33.6.0.23", {"start": v(172.9, -164.25) * mm, "end": v(172.9, -183) * mm});
            skLineSegment(sketch, "E33.6.0.24", {"start": v(172.9, -111.75) * mm, "end": v(172.9, -93) * mm});
            skLineSegment(sketch, "E33.6.0.25", {"start": v(175.8, -176.12) * mm, "end": v(176.2, -176.12) * mm});
            skLineSegment(sketch, "E33.6.0.26", {"start": v(175.8, -171.12) * mm, "end": v(176.2, -171.12) * mm});
            skLineSegment(sketch, "E33.6.0.27", {"start": v(175.8, -152.37) * mm, "end": v(176.2, -152.37) * mm});
            skLineSegment(sketch, "E33.6.0.28", {"start": v(175.8, -147.37) * mm, "end": v(176.2, -147.37) * mm});
            skLineSegment(sketch, "E33.6.0.29", {"start": v(175.8, -128.62) * mm, "end": v(176.2, -128.62) * mm});
            skLineSegment(sketch, "E33.6.0.30", {"start": v(175.8, -123.62) * mm, "end": v(176.2, -123.62) * mm});
            skLineSegment(sketch, "E33.6.0.31", {"start": v(175.8, -104.87) * mm, "end": v(176.2, -104.87) * mm});
            skLineSegment(sketch, "E33.6.0.32", {"start": v(175.8, -99.87) * mm, "end": v(176.2, -99.87) * mm});
            skLineSegment(sketch, "E33.6.0.33", {"start": v(172.9, -164.25) * mm, "end": v(173.3, -164.25) * mm});
            skLineSegment(sketch, "E33.6.0.34", {"start": v(172.9, -159.25) * mm, "end": v(173.3, -159.25) * mm});
            skLineSegment(sketch, "E33.6.0.35", {"start": v(176.2, -93) * mm, "end": v(172.9, -93) * mm, "construction": true});
            skLineSegment(sketch, "E33.6.0.36", {"start": v(172.9, -140.5) * mm, "end": v(173.3, -140.5) * mm});
            skLineSegment(sketch, "E33.6.0.37", {"start": v(172.9, -135.5) * mm, "end": v(173.3, -135.5) * mm});
            skLineSegment(sketch, "E33.6.0.38", {"start": v(172.9, -116.75) * mm, "end": v(173.3, -116.75) * mm});
            skLineSegment(sketch, "E33.6.0.39", {"start": v(175.8, -183) * mm, "end": v(176.2, -183) * mm});
            skLineSegment(sketch, "E33.6.0.40", {"start": v(175.8, -93) * mm, "end": v(176.2, -93) * mm});
            skLineSegment(sketch, "E33.6.0.41", {"start": v(176.2, -183) * mm, "end": v(172.9, -183) * mm, "construction": true});
            skLineSegment(sketch, "E33.6.0.42", {"start": v(173.3, -111.75) * mm, "end": v(172.9, -111.75) * mm});
            skLineSegment(sketch, "E33.6.0.43", {"start": v(172.9, -183) * mm, "end": v(173.3, -183) * mm});
            skLineSegment(sketch, "E33.6.0.44", {"start": v(172.9, -111.75) * mm, "end": v(173.3, -111.75) * mm});
            skLineSegment(sketch, "E33.6.0.45", {"start": v(173.3, -93) * mm, "end": v(172.9, -93) * mm});
            skLineSegment(sketch, "E33.7.0.0", {"start": v(181.65, -99.87) * mm, "end": v(181.65, -93) * mm});
            skLineSegment(sketch, "E33.7.0.1", {"start": v(178.75, -183) * mm, "end": v(178.75, -93) * mm, "construction": true});
            skLineSegment(sketch, "E33.7.0.2", {"start": v(182.05, -152.37) * mm, "end": v(182.05, -171.12) * mm});
            skLineSegment(sketch, "E33.7.0.3", {"start": v(181.65, -104.87) * mm, "end": v(181.65, -123.62) * mm});
            skLineSegment(sketch, "E33.7.0.4", {"start": v(179.15, -159.25) * mm, "end": v(179.15, -140.5) * mm});
            skLineSegment(sketch, "E33.7.0.5", {"start": v(182.05, -128.62) * mm, "end": v(182.05, -147.37) * mm});
            skLineSegment(sketch, "E33.7.0.6", {"start": v(181.65, -128.62) * mm, "end": v(181.65, -147.37) * mm});
            skLineSegment(sketch, "E33.7.0.7", {"start": v(178.75, -164.25) * mm, "end": v(178.75, -183) * mm});
            skLineSegment(sketch, "E33.7.0.8", {"start": v(179.15, -164.25) * mm, "end": v(179.15, -183) * mm});
            skLineSegment(sketch, "E33.7.0.9", {"start": v(181.65, -176.12) * mm, "end": v(181.65, -183) * mm});
            skLineSegment(sketch, "E33.7.0.10", {"start": v(182.05, -176.12) * mm, "end": v(182.05, -183) * mm});
            skLineSegment(sketch, "E33.7.0.11", {"start": v(182.05, -183) * mm, "end": v(182.05, -93) * mm, "construction": true});
            skLineSegment(sketch, "E33.7.0.12", {"start": v(181.65, -152.37) * mm, "end": v(181.65, -171.12) * mm});
            skLineSegment(sketch, "E33.7.0.13", {"start": v(178.75, -140.5) * mm, "end": v(178.75, -159.25) * mm});
            skLineSegment(sketch, "E33.7.0.14", {"start": v(178.75, -116.75) * mm, "end": v(178.75, -135.5) * mm});
            skLineSegment(sketch, "E33.7.0.15", {"start": v(179.15, -116.75) * mm, "end": v(179.15, -135.5) * mm});
            skLineSegment(sketch, "E33.7.0.16", {"start": v(182.05, -104.87) * mm, "end": v(182.05, -123.62) * mm});
            skLineSegment(sketch, "E33.7.0.17", {"start": v(178.75, -93) * mm, "end": v(178.75, -111.75) * mm});
            skLineSegment(sketch, "E33.7.0.18", {"start": v(179.15, -93) * mm, "end": v(179.15, -111.75) * mm});
            skLineSegment(sketch, "E33.7.0.19", {"start": v(182.05, -99.87) * mm, "end": v(182.05, -93) * mm});
            skLineSegment(sketch, "E33.7.0.20", {"start": v(178.75, -159.25) * mm, "end": v(178.75, -140.5) * mm});
            skLineSegment(sketch, "E33.7.0.21", {"start": v(178.75, -116.75) * mm, "end": v(178.75, -135.5) * mm});
            skLineSegment(sketch, "E33.7.0.22", {"start": v(179.15, -111.75) * mm, "end": v(179.15, -93) * mm});
            skLineSegment(sketch, "E33.7.0.23", {"start": v(178.75, -164.25) * mm, "end": v(178.75, -183) * mm});
            skLineSegment(sketch, "E33.7.0.24", {"start": v(178.75, -111.75) * mm, "end": v(178.75, -93) * mm});
            skLineSegment(sketch, "E33.7.0.25", {"start": v(181.65, -176.12) * mm, "end": v(182.05, -176.12) * mm});
            skLineSegment(sketch, "E33.7.0.26", {"start": v(181.65, -171.12) * mm, "end": v(182.05, -171.12) * mm});
            skLineSegment(sketch, "E33.7.0.27", {"start": v(181.65, -152.37) * mm, "end": v(182.05, -152.37) * mm});
            skLineSegment(sketch, "E33.7.0.28", {"start": v(181.65, -147.37) * mm, "end": v(182.05, -147.37) * mm});
            skLineSegment(sketch, "E33.7.0.29", {"start": v(181.65, -128.62) * mm, "end": v(182.05, -128.62) * mm});
            skLineSegment(sketch, "E33.7.0.30", {"start": v(181.65, -123.62) * mm, "end": v(182.05, -123.62) * mm});
            skLineSegment(sketch, "E33.7.0.31", {"start": v(181.65, -104.87) * mm, "end": v(182.05, -104.87) * mm});
            skLineSegment(sketch, "E33.7.0.32", {"start": v(181.65, -99.87) * mm, "end": v(182.05, -99.87) * mm});
            skLineSegment(sketch, "E33.7.0.33", {"start": v(178.75, -164.25) * mm, "end": v(179.15, -164.25) * mm});
            skLineSegment(sketch, "E33.7.0.34", {"start": v(178.75, -159.25) * mm, "end": v(179.15, -159.25) * mm});
            skLineSegment(sketch, "E33.7.0.35", {"start": v(182.05, -93) * mm, "end": v(178.75, -93) * mm, "construction": true});
            skLineSegment(sketch, "E33.7.0.36", {"start": v(178.75, -140.5) * mm, "end": v(179.15, -140.5) * mm});
            skLineSegment(sketch, "E33.7.0.37", {"start": v(178.75, -135.5) * mm, "end": v(179.15, -135.5) * mm});
            skLineSegment(sketch, "E33.7.0.38", {"start": v(178.75, -116.75) * mm, "end": v(179.15, -116.75) * mm});
            skLineSegment(sketch, "E33.7.0.39", {"start": v(181.65, -183) * mm, "end": v(182.05, -183) * mm});
            skLineSegment(sketch, "E33.7.0.40", {"start": v(181.65, -93) * mm, "end": v(182.05, -93) * mm});
            skLineSegment(sketch, "E33.7.0.41", {"start": v(182.05, -183) * mm, "end": v(178.75, -183) * mm, "construction": true});
            skLineSegment(sketch, "E33.7.0.42", {"start": v(179.15, -111.75) * mm, "end": v(178.75, -111.75) * mm});
            skLineSegment(sketch, "E33.7.0.43", {"start": v(178.75, -183) * mm, "end": v(179.15, -183) * mm});
            skLineSegment(sketch, "E33.7.0.44", {"start": v(178.75, -111.75) * mm, "end": v(179.15, -111.75) * mm});
            skLineSegment(sketch, "E33.7.0.45", {"start": v(179.15, -93) * mm, "end": v(178.75, -93) * mm});
            skLineSegment(sketch, "E33.8.0.0", {"start": v(187.5, -99.87) * mm, "end": v(187.5, -93) * mm});
            skLineSegment(sketch, "E33.8.0.1", {"start": v(184.6, -183) * mm, "end": v(184.6, -93) * mm, "construction": true});
            skLineSegment(sketch, "E33.8.0.2", {"start": v(187.9, -152.37) * mm, "end": v(187.9, -171.12) * mm});
            skLineSegment(sketch, "E33.8.0.3", {"start": v(187.5, -104.87) * mm, "end": v(187.5, -123.62) * mm});
            skLineSegment(sketch, "E33.8.0.4", {"start": v(185, -159.25) * mm, "end": v(185, -140.5) * mm});
            skLineSegment(sketch, "E33.8.0.5", {"start": v(187.9, -128.62) * mm, "end": v(187.9, -147.37) * mm});
            skLineSegment(sketch, "E33.8.0.6", {"start": v(187.5, -128.62) * mm, "end": v(187.5, -147.37) * mm});
            skLineSegment(sketch, "E33.8.0.7", {"start": v(184.6, -164.25) * mm, "end": v(184.6, -183) * mm});
            skLineSegment(sketch, "E33.8.0.8", {"start": v(185, -164.25) * mm, "end": v(185, -183) * mm});
            skLineSegment(sketch, "E33.8.0.9", {"start": v(187.5, -176.12) * mm, "end": v(187.5, -183) * mm});
            skLineSegment(sketch, "E33.8.0.10", {"start": v(187.9, -176.12) * mm, "end": v(187.9, -183) * mm});
            skLineSegment(sketch, "E33.8.0.11", {"start": v(187.9, -183) * mm, "end": v(187.9, -93) * mm, "construction": true});
            skLineSegment(sketch, "E33.8.0.12", {"start": v(187.5, -152.37) * mm, "end": v(187.5, -171.12) * mm});
            skLineSegment(sketch, "E33.8.0.13", {"start": v(184.6, -140.5) * mm, "end": v(184.6, -159.25) * mm});
            skLineSegment(sketch, "E33.8.0.14", {"start": v(184.6, -116.75) * mm, "end": v(184.6, -135.5) * mm});
            skLineSegment(sketch, "E33.8.0.15", {"start": v(185, -116.75) * mm, "end": v(185, -135.5) * mm});
            skLineSegment(sketch, "E33.8.0.16", {"start": v(187.9, -104.87) * mm, "end": v(187.9, -123.62) * mm});
            skLineSegment(sketch, "E33.8.0.17", {"start": v(184.6, -93) * mm, "end": v(184.6, -111.75) * mm});
            skLineSegment(sketch, "E33.8.0.18", {"start": v(185, -93) * mm, "end": v(185, -111.75) * mm});
            skLineSegment(sketch, "E33.8.0.19", {"start": v(187.9, -99.87) * mm, "end": v(187.9, -93) * mm});
            skLineSegment(sketch, "E33.8.0.20", {"start": v(184.6, -159.25) * mm, "end": v(184.6, -140.5) * mm});
            skLineSegment(sketch, "E33.8.0.21", {"start": v(184.6, -116.75) * mm, "end": v(184.6, -135.5) * mm});
            skLineSegment(sketch, "E33.8.0.22", {"start": v(185, -111.75) * mm, "end": v(185, -93) * mm});
            skLineSegment(sketch, "E33.8.0.23", {"start": v(184.6, -164.25) * mm, "end": v(184.6, -183) * mm});
            skLineSegment(sketch, "E33.8.0.24", {"start": v(184.6, -111.75) * mm, "end": v(184.6, -93) * mm});
            skLineSegment(sketch, "E33.8.0.25", {"start": v(187.5, -176.12) * mm, "end": v(187.9, -176.12) * mm});
            skLineSegment(sketch, "E33.8.0.26", {"start": v(187.5, -171.12) * mm, "end": v(187.9, -171.12) * mm});
            skLineSegment(sketch, "E33.8.0.27", {"start": v(187.5, -152.37) * mm, "end": v(187.9, -152.37) * mm});
            skLineSegment(sketch, "E33.8.0.28", {"start": v(187.5, -147.37) * mm, "end": v(187.9, -147.37) * mm});
            skLineSegment(sketch, "E33.8.0.29", {"start": v(187.5, -128.62) * mm, "end": v(187.9, -128.62) * mm});
            skLineSegment(sketch, "E33.8.0.30", {"start": v(187.5, -123.62) * mm, "end": v(187.9, -123.62) * mm});
            skLineSegment(sketch, "E33.8.0.31", {"start": v(187.5, -104.87) * mm, "end": v(187.9, -104.87) * mm});
            skLineSegment(sketch, "E33.8.0.32", {"start": v(187.5, -99.87) * mm, "end": v(187.9, -99.87) * mm});
            skLineSegment(sketch, "E33.8.0.33", {"start": v(184.6, -164.25) * mm, "end": v(185, -164.25) * mm});
            skLineSegment(sketch, "E33.8.0.34", {"start": v(184.6, -159.25) * mm, "end": v(185, -159.25) * mm});
            skLineSegment(sketch, "E33.8.0.35", {"start": v(187.9, -93) * mm, "end": v(184.6, -93) * mm, "construction": true});
            skLineSegment(sketch, "E33.8.0.36", {"start": v(184.6, -140.5) * mm, "end": v(185, -140.5) * mm});
            skLineSegment(sketch, "E33.8.0.37", {"start": v(184.6, -135.5) * mm, "end": v(185, -135.5) * mm});
            skLineSegment(sketch, "E33.8.0.38", {"start": v(184.6, -116.75) * mm, "end": v(185, -116.75) * mm});
            skLineSegment(sketch, "E33.8.0.39", {"start": v(187.5, -183) * mm, "end": v(187.9, -183) * mm});
            skLineSegment(sketch, "E33.8.0.40", {"start": v(187.5, -93) * mm, "end": v(187.9, -93) * mm});
            skLineSegment(sketch, "E33.8.0.41", {"start": v(187.9, -183) * mm, "end": v(184.6, -183) * mm, "construction": true});
            skLineSegment(sketch, "E33.8.0.42", {"start": v(185, -111.75) * mm, "end": v(184.6, -111.75) * mm});
            skLineSegment(sketch, "E33.8.0.43", {"start": v(184.6, -183) * mm, "end": v(185, -183) * mm});
            skLineSegment(sketch, "E33.8.0.44", {"start": v(184.6, -111.75) * mm, "end": v(185, -111.75) * mm});
            skLineSegment(sketch, "E33.8.0.45", {"start": v(185, -93) * mm, "end": v(184.6, -93) * mm});
            skLineSegment(sketch, "E33.9.0.0", {"start": v(193.35, -99.87) * mm, "end": v(193.35, -93) * mm});
            skLineSegment(sketch, "E33.9.0.1", {"start": v(190.45, -183) * mm, "end": v(190.45, -93) * mm, "construction": true});
            skLineSegment(sketch, "E33.9.0.2", {"start": v(193.75, -152.37) * mm, "end": v(193.75, -171.12) * mm});
            skLineSegment(sketch, "E33.9.0.3", {"start": v(193.35, -104.87) * mm, "end": v(193.35, -123.62) * mm});
            skLineSegment(sketch, "E33.9.0.4", {"start": v(190.85, -159.25) * mm, "end": v(190.85, -140.5) * mm});
            skLineSegment(sketch, "E33.9.0.5", {"start": v(193.75, -128.62) * mm, "end": v(193.75, -147.37) * mm});
            skLineSegment(sketch, "E33.9.0.6", {"start": v(193.35, -128.62) * mm, "end": v(193.35, -147.37) * mm});
            skLineSegment(sketch, "E33.9.0.7", {"start": v(190.45, -164.25) * mm, "end": v(190.45, -183) * mm});
            skLineSegment(sketch, "E33.9.0.8", {"start": v(190.85, -164.25) * mm, "end": v(190.85, -183) * mm});
            skLineSegment(sketch, "E33.9.0.9", {"start": v(193.35, -176.12) * mm, "end": v(193.35, -183) * mm});
            skLineSegment(sketch, "E33.9.0.10", {"start": v(193.75, -176.12) * mm, "end": v(193.75, -183) * mm});
            skLineSegment(sketch, "E33.9.0.11", {"start": v(193.75, -183) * mm, "end": v(193.75, -93) * mm, "construction": true});
            skLineSegment(sketch, "E33.9.0.12", {"start": v(193.35, -152.37) * mm, "end": v(193.35, -171.12) * mm});
            skLineSegment(sketch, "E33.9.0.13", {"start": v(190.45, -140.5) * mm, "end": v(190.45, -159.25) * mm});
            skLineSegment(sketch, "E33.9.0.14", {"start": v(190.45, -116.75) * mm, "end": v(190.45, -135.5) * mm});
            skLineSegment(sketch, "E33.9.0.15", {"start": v(190.85, -116.75) * mm, "end": v(190.85, -135.5) * mm});
            skLineSegment(sketch, "E33.9.0.16", {"start": v(193.75, -104.87) * mm, "end": v(193.75, -123.62) * mm});
            skLineSegment(sketch, "E33.9.0.17", {"start": v(190.45, -93) * mm, "end": v(190.45, -111.75) * mm});
            skLineSegment(sketch, "E33.9.0.18", {"start": v(190.85, -93) * mm, "end": v(190.85, -111.75) * mm});
            skLineSegment(sketch, "E33.9.0.19", {"start": v(193.75, -99.87) * mm, "end": v(193.75, -93) * mm});
            skLineSegment(sketch, "E33.9.0.20", {"start": v(190.45, -159.25) * mm, "end": v(190.45, -140.5) * mm});
            skLineSegment(sketch, "E33.9.0.21", {"start": v(190.45, -116.75) * mm, "end": v(190.45, -135.5) * mm});
            skLineSegment(sketch, "E33.9.0.22", {"start": v(190.85, -111.75) * mm, "end": v(190.85, -93) * mm});
            skLineSegment(sketch, "E33.9.0.23", {"start": v(190.45, -164.25) * mm, "end": v(190.45, -183) * mm});
            skLineSegment(sketch, "E33.9.0.24", {"start": v(190.45, -111.75) * mm, "end": v(190.45, -93) * mm});
            skLineSegment(sketch, "E33.9.0.25", {"start": v(193.35, -176.12) * mm, "end": v(193.75, -176.12) * mm});
            skLineSegment(sketch, "E33.9.0.26", {"start": v(193.35, -171.12) * mm, "end": v(193.75, -171.12) * mm});
            skLineSegment(sketch, "E33.9.0.27", {"start": v(193.35, -152.37) * mm, "end": v(193.75, -152.37) * mm});
            skLineSegment(sketch, "E33.9.0.28", {"start": v(193.35, -147.37) * mm, "end": v(193.75, -147.37) * mm});
            skLineSegment(sketch, "E33.9.0.29", {"start": v(193.35, -128.62) * mm, "end": v(193.75, -128.62) * mm});
            skLineSegment(sketch, "E33.9.0.30", {"start": v(193.35, -123.62) * mm, "end": v(193.75, -123.62) * mm});
            skLineSegment(sketch, "E33.9.0.31", {"start": v(193.35, -104.87) * mm, "end": v(193.75, -104.87) * mm});
            skLineSegment(sketch, "E33.9.0.32", {"start": v(193.35, -99.87) * mm, "end": v(193.75, -99.87) * mm});
            skLineSegment(sketch, "E33.9.0.33", {"start": v(190.45, -164.25) * mm, "end": v(190.85, -164.25) * mm});
            skLineSegment(sketch, "E33.9.0.34", {"start": v(190.45, -159.25) * mm, "end": v(190.85, -159.25) * mm});
            skLineSegment(sketch, "E33.9.0.35", {"start": v(193.75, -93) * mm, "end": v(190.45, -93) * mm, "construction": true});
            skLineSegment(sketch, "E33.9.0.36", {"start": v(190.45, -140.5) * mm, "end": v(190.85, -140.5) * mm});
            skLineSegment(sketch, "E33.9.0.37", {"start": v(190.45, -135.5) * mm, "end": v(190.85, -135.5) * mm});
            skLineSegment(sketch, "E33.9.0.38", {"start": v(190.45, -116.75) * mm, "end": v(190.85, -116.75) * mm});
            skLineSegment(sketch, "E33.9.0.39", {"start": v(193.35, -183) * mm, "end": v(193.75, -183) * mm});
            skLineSegment(sketch, "E33.9.0.40", {"start": v(193.35, -93) * mm, "end": v(193.75, -93) * mm});
            skLineSegment(sketch, "E33.9.0.41", {"start": v(193.75, -183) * mm, "end": v(190.45, -183) * mm, "construction": true});
            skLineSegment(sketch, "E33.9.0.42", {"start": v(190.85, -111.75) * mm, "end": v(190.45, -111.75) * mm});
            skLineSegment(sketch, "E33.9.0.43", {"start": v(190.45, -183) * mm, "end": v(190.85, -183) * mm});
            skLineSegment(sketch, "E33.9.0.44", {"start": v(190.45, -111.75) * mm, "end": v(190.85, -111.75) * mm});
            skLineSegment(sketch, "E33.9.0.45", {"start": v(190.85, -93) * mm, "end": v(190.45, -93) * mm});
            skLineSegment(sketch, "E33.10.0.0", {"start": v(199.2, -99.87) * mm, "end": v(199.2, -93) * mm});
            skLineSegment(sketch, "E33.10.0.1", {"start": v(196.3, -183) * mm, "end": v(196.3, -93) * mm, "construction": true});
            skLineSegment(sketch, "E33.10.0.2", {"start": v(199.6, -152.37) * mm, "end": v(199.6, -171.12) * mm});
            skLineSegment(sketch, "E33.10.0.3", {"start": v(199.2, -104.87) * mm, "end": v(199.2, -123.62) * mm});
            skLineSegment(sketch, "E33.10.0.4", {"start": v(196.7, -159.25) * mm, "end": v(196.7, -140.5) * mm});
            skLineSegment(sketch, "E33.10.0.5", {"start": v(199.6, -128.62) * mm, "end": v(199.6, -147.37) * mm});
            skLineSegment(sketch, "E33.10.0.6", {"start": v(199.2, -128.62) * mm, "end": v(199.2, -147.37) * mm});
            skLineSegment(sketch, "E33.10.0.7", {"start": v(196.3, -164.25) * mm, "end": v(196.3, -183) * mm});
            skLineSegment(sketch, "E33.10.0.8", {"start": v(196.7, -164.25) * mm, "end": v(196.7, -183) * mm});
            skLineSegment(sketch, "E33.10.0.9", {"start": v(199.2, -176.12) * mm, "end": v(199.2, -183) * mm});
            skLineSegment(sketch, "E33.10.0.10", {"start": v(199.6, -176.12) * mm, "end": v(199.6, -183) * mm});
            skLineSegment(sketch, "E33.10.0.11", {"start": v(199.6, -183) * mm, "end": v(199.6, -93) * mm, "construction": true});
            skLineSegment(sketch, "E33.10.0.12", {"start": v(199.2, -152.37) * mm, "end": v(199.2, -171.12) * mm});
            skLineSegment(sketch, "E33.10.0.13", {"start": v(196.3, -140.5) * mm, "end": v(196.3, -159.25) * mm});
            skLineSegment(sketch, "E33.10.0.14", {"start": v(196.3, -116.75) * mm, "end": v(196.3, -135.5) * mm});
            skLineSegment(sketch, "E33.10.0.15", {"start": v(196.7, -116.75) * mm, "end": v(196.7, -135.5) * mm});
            skLineSegment(sketch, "E33.10.0.16", {"start": v(199.6, -104.87) * mm, "end": v(199.6, -123.62) * mm});
            skLineSegment(sketch, "E33.10.0.17", {"start": v(196.3, -93) * mm, "end": v(196.3, -111.75) * mm});
            skLineSegment(sketch, "E33.10.0.18", {"start": v(196.7, -93) * mm, "end": v(196.7, -111.75) * mm});
            skLineSegment(sketch, "E33.10.0.19", {"start": v(199.6, -99.87) * mm, "end": v(199.6, -93) * mm});
            skLineSegment(sketch, "E33.10.0.20", {"start": v(196.3, -159.25) * mm, "end": v(196.3, -140.5) * mm});
            skLineSegment(sketch, "E33.10.0.21", {"start": v(196.3, -116.75) * mm, "end": v(196.3, -135.5) * mm});
            skLineSegment(sketch, "E33.10.0.22", {"start": v(196.7, -111.75) * mm, "end": v(196.7, -93) * mm});
            skLineSegment(sketch, "E33.10.0.23", {"start": v(196.3, -164.25) * mm, "end": v(196.3, -183) * mm});
            skLineSegment(sketch, "E33.10.0.24", {"start": v(196.3, -111.75) * mm, "end": v(196.3, -93) * mm});
            skLineSegment(sketch, "E33.10.0.25", {"start": v(199.2, -176.12) * mm, "end": v(199.6, -176.12) * mm});
            skLineSegment(sketch, "E33.10.0.26", {"start": v(199.2, -171.12) * mm, "end": v(199.6, -171.12) * mm});
            skLineSegment(sketch, "E33.10.0.27", {"start": v(199.2, -152.37) * mm, "end": v(199.6, -152.37) * mm});
            skLineSegment(sketch, "E33.10.0.28", {"start": v(199.2, -147.37) * mm, "end": v(199.6, -147.37) * mm});
            skLineSegment(sketch, "E33.10.0.29", {"start": v(199.2, -128.62) * mm, "end": v(199.6, -128.62) * mm});
            skLineSegment(sketch, "E33.10.0.30", {"start": v(199.2, -123.62) * mm, "end": v(199.6, -123.62) * mm});
            skLineSegment(sketch, "E33.10.0.31", {"start": v(199.2, -104.87) * mm, "end": v(199.6, -104.87) * mm});
            skLineSegment(sketch, "E33.10.0.32", {"start": v(199.2, -99.87) * mm, "end": v(199.6, -99.87) * mm});
            skLineSegment(sketch, "E33.10.0.33", {"start": v(196.3, -164.25) * mm, "end": v(196.7, -164.25) * mm});
            skLineSegment(sketch, "E33.10.0.34", {"start": v(196.3, -159.25) * mm, "end": v(196.7, -159.25) * mm});
            skLineSegment(sketch, "E33.10.0.35", {"start": v(199.6, -93) * mm, "end": v(196.3, -93) * mm, "construction": true});
            skLineSegment(sketch, "E33.10.0.36", {"start": v(196.3, -140.5) * mm, "end": v(196.7, -140.5) * mm});
            skLineSegment(sketch, "E33.10.0.37", {"start": v(196.3, -135.5) * mm, "end": v(196.7, -135.5) * mm});
            skLineSegment(sketch, "E33.10.0.38", {"start": v(196.3, -116.75) * mm, "end": v(196.7, -116.75) * mm});
            skLineSegment(sketch, "E33.10.0.39", {"start": v(199.2, -183) * mm, "end": v(199.6, -183) * mm});
            skLineSegment(sketch, "E33.10.0.40", {"start": v(199.2, -93) * mm, "end": v(199.6, -93) * mm});
            skLineSegment(sketch, "E33.10.0.41", {"start": v(199.6, -183) * mm, "end": v(196.3, -183) * mm, "construction": true});
            skLineSegment(sketch, "E33.10.0.42", {"start": v(196.7, -111.75) * mm, "end": v(196.3, -111.75) * mm});
            skLineSegment(sketch, "E33.10.0.43", {"start": v(196.3, -183) * mm, "end": v(196.7, -183) * mm});
            skLineSegment(sketch, "E33.10.0.44", {"start": v(196.3, -111.75) * mm, "end": v(196.7, -111.75) * mm});
            skLineSegment(sketch, "E33.10.0.45", {"start": v(196.7, -93) * mm, "end": v(196.3, -93) * mm});
            skLineSegment(sketch, "E33.11.0.0", {"start": v(205.05, -99.87) * mm, "end": v(205.05, -93) * mm});
            skLineSegment(sketch, "E33.11.0.1", {"start": v(202.15, -183) * mm, "end": v(202.15, -93) * mm, "construction": true});
            skLineSegment(sketch, "E33.11.0.2", {"start": v(205.45, -152.37) * mm, "end": v(205.45, -171.12) * mm});
            skLineSegment(sketch, "E33.11.0.3", {"start": v(205.05, -104.87) * mm, "end": v(205.05, -123.62) * mm});
            skLineSegment(sketch, "E33.11.0.4", {"start": v(202.55, -159.25) * mm, "end": v(202.55, -140.5) * mm});
            skLineSegment(sketch, "E33.11.0.5", {"start": v(205.45, -128.62) * mm, "end": v(205.45, -147.37) * mm});
            skLineSegment(sketch, "E33.11.0.6", {"start": v(205.05, -128.62) * mm, "end": v(205.05, -147.37) * mm});
            skLineSegment(sketch, "E33.11.0.7", {"start": v(202.15, -164.25) * mm, "end": v(202.15, -183) * mm});
            skLineSegment(sketch, "E33.11.0.8", {"start": v(202.55, -164.25) * mm, "end": v(202.55, -183) * mm});
            skLineSegment(sketch, "E33.11.0.9", {"start": v(205.05, -176.12) * mm, "end": v(205.05, -183) * mm});
            skLineSegment(sketch, "E33.11.0.10", {"start": v(205.45, -176.12) * mm, "end": v(205.45, -183) * mm});
            skLineSegment(sketch, "E33.11.0.11", {"start": v(205.45, -183) * mm, "end": v(205.45, -93) * mm, "construction": true});
            skLineSegment(sketch, "E33.11.0.12", {"start": v(205.05, -152.37) * mm, "end": v(205.05, -171.12) * mm});
            skLineSegment(sketch, "E33.11.0.13", {"start": v(202.15, -140.5) * mm, "end": v(202.15, -159.25) * mm});
            skLineSegment(sketch, "E33.11.0.14", {"start": v(202.15, -116.75) * mm, "end": v(202.15, -135.5) * mm});
            skLineSegment(sketch, "E33.11.0.15", {"start": v(202.55, -116.75) * mm, "end": v(202.55, -135.5) * mm});
            skLineSegment(sketch, "E33.11.0.16", {"start": v(205.45, -104.87) * mm, "end": v(205.45, -123.62) * mm});
            skLineSegment(sketch, "E33.11.0.17", {"start": v(202.15, -93) * mm, "end": v(202.15, -111.75) * mm});
            skLineSegment(sketch, "E33.11.0.18", {"start": v(202.55, -93) * mm, "end": v(202.55, -111.75) * mm});
            skLineSegment(sketch, "E33.11.0.19", {"start": v(205.45, -99.87) * mm, "end": v(205.45, -93) * mm});
            skLineSegment(sketch, "E33.11.0.20", {"start": v(202.15, -159.25) * mm, "end": v(202.15, -140.5) * mm});
            skLineSegment(sketch, "E33.11.0.21", {"start": v(202.15, -116.75) * mm, "end": v(202.15, -135.5) * mm});
            skLineSegment(sketch, "E33.11.0.22", {"start": v(202.55, -111.75) * mm, "end": v(202.55, -93) * mm});
            skLineSegment(sketch, "E33.11.0.23", {"start": v(202.15, -164.25) * mm, "end": v(202.15, -183) * mm});
            skLineSegment(sketch, "E33.11.0.24", {"start": v(202.15, -111.75) * mm, "end": v(202.15, -93) * mm});
            skLineSegment(sketch, "E33.11.0.25", {"start": v(205.05, -176.12) * mm, "end": v(205.45, -176.12) * mm});
            skLineSegment(sketch, "E33.11.0.26", {"start": v(205.05, -171.12) * mm, "end": v(205.45, -171.12) * mm});
            skLineSegment(sketch, "E33.11.0.27", {"start": v(205.05, -152.37) * mm, "end": v(205.45, -152.37) * mm});
            skLineSegment(sketch, "E33.11.0.28", {"start": v(205.05, -147.37) * mm, "end": v(205.45, -147.37) * mm});
            skLineSegment(sketch, "E33.11.0.29", {"start": v(205.05, -128.62) * mm, "end": v(205.45, -128.62) * mm});
            skLineSegment(sketch, "E33.11.0.30", {"start": v(205.05, -123.62) * mm, "end": v(205.45, -123.62) * mm});
            skLineSegment(sketch, "E33.11.0.31", {"start": v(205.05, -104.87) * mm, "end": v(205.45, -104.87) * mm});
            skLineSegment(sketch, "E33.11.0.32", {"start": v(205.05, -99.87) * mm, "end": v(205.45, -99.87) * mm});
            skLineSegment(sketch, "E33.11.0.33", {"start": v(202.15, -164.25) * mm, "end": v(202.55, -164.25) * mm});
            skLineSegment(sketch, "E33.11.0.34", {"start": v(202.15, -159.25) * mm, "end": v(202.55, -159.25) * mm});
            skLineSegment(sketch, "E33.11.0.35", {"start": v(205.45, -93) * mm, "end": v(202.15, -93) * mm, "construction": true});
            skLineSegment(sketch, "E33.11.0.36", {"start": v(202.15, -140.5) * mm, "end": v(202.55, -140.5) * mm});
            skLineSegment(sketch, "E33.11.0.37", {"start": v(202.15, -135.5) * mm, "end": v(202.55, -135.5) * mm});
            skLineSegment(sketch, "E33.11.0.38", {"start": v(202.15, -116.75) * mm, "end": v(202.55, -116.75) * mm});
            skLineSegment(sketch, "E33.11.0.39", {"start": v(205.05, -183) * mm, "end": v(205.45, -183) * mm});
            skLineSegment(sketch, "E33.11.0.40", {"start": v(205.05, -93) * mm, "end": v(205.45, -93) * mm});
            skLineSegment(sketch, "E33.11.0.41", {"start": v(205.45, -183) * mm, "end": v(202.15, -183) * mm, "construction": true});
            skLineSegment(sketch, "E33.11.0.42", {"start": v(202.55, -111.75) * mm, "end": v(202.15, -111.75) * mm});
            skLineSegment(sketch, "E33.11.0.43", {"start": v(202.15, -183) * mm, "end": v(202.55, -183) * mm});
            skLineSegment(sketch, "E33.11.0.44", {"start": v(202.15, -111.75) * mm, "end": v(202.55, -111.75) * mm});
            skLineSegment(sketch, "E33.11.0.45", {"start": v(202.55, -93) * mm, "end": v(202.15, -93) * mm});
            skLineSegment(sketch, "E33.12.0.0", {"start": v(210.9, -99.87) * mm, "end": v(210.9, -93) * mm});
            skLineSegment(sketch, "E33.12.0.1", {"start": v(208, -183) * mm, "end": v(208, -93) * mm, "construction": true});
            skLineSegment(sketch, "E33.12.0.2", {"start": v(211.3, -152.37) * mm, "end": v(211.3, -171.12) * mm});
            skLineSegment(sketch, "E33.12.0.3", {"start": v(210.9, -104.87) * mm, "end": v(210.9, -123.62) * mm});
            skLineSegment(sketch, "E33.12.0.4", {"start": v(208.4, -159.25) * mm, "end": v(208.4, -140.5) * mm});
            skLineSegment(sketch, "E33.12.0.5", {"start": v(211.3, -128.62) * mm, "end": v(211.3, -147.37) * mm});
            skLineSegment(sketch, "E33.12.0.6", {"start": v(210.9, -128.62) * mm, "end": v(210.9, -147.37) * mm});
            skLineSegment(sketch, "E33.12.0.7", {"start": v(208, -164.25) * mm, "end": v(208, -183) * mm});
            skLineSegment(sketch, "E33.12.0.8", {"start": v(208.4, -164.25) * mm, "end": v(208.4, -183) * mm});
            skLineSegment(sketch, "E33.12.0.9", {"start": v(210.9, -176.12) * mm, "end": v(210.9, -183) * mm});
            skLineSegment(sketch, "E33.12.0.10", {"start": v(211.3, -176.12) * mm, "end": v(211.3, -183) * mm});
            skLineSegment(sketch, "E33.12.0.11", {"start": v(211.3, -183) * mm, "end": v(211.3, -93) * mm, "construction": true});
            skLineSegment(sketch, "E33.12.0.12", {"start": v(210.9, -152.37) * mm, "end": v(210.9, -171.12) * mm});
            skLineSegment(sketch, "E33.12.0.13", {"start": v(208, -140.5) * mm, "end": v(208, -159.25) * mm});
            skLineSegment(sketch, "E33.12.0.14", {"start": v(208, -116.75) * mm, "end": v(208, -135.5) * mm});
            skLineSegment(sketch, "E33.12.0.15", {"start": v(208.4, -116.75) * mm, "end": v(208.4, -135.5) * mm});
            skLineSegment(sketch, "E33.12.0.16", {"start": v(211.3, -104.87) * mm, "end": v(211.3, -123.62) * mm});
            skLineSegment(sketch, "E33.12.0.17", {"start": v(208, -93) * mm, "end": v(208, -111.75) * mm});
            skLineSegment(sketch, "E33.12.0.18", {"start": v(208.4, -93) * mm, "end": v(208.4, -111.75) * mm});
            skLineSegment(sketch, "E33.12.0.19", {"start": v(211.3, -99.87) * mm, "end": v(211.3, -93) * mm});
            skLineSegment(sketch, "E33.12.0.20", {"start": v(208, -159.25) * mm, "end": v(208, -140.5) * mm});
            skLineSegment(sketch, "E33.12.0.21", {"start": v(208, -116.75) * mm, "end": v(208, -135.5) * mm});
            skLineSegment(sketch, "E33.12.0.22", {"start": v(208.4, -111.75) * mm, "end": v(208.4, -93) * mm});
            skLineSegment(sketch, "E33.12.0.23", {"start": v(208, -164.25) * mm, "end": v(208, -183) * mm});
            skLineSegment(sketch, "E33.12.0.24", {"start": v(208, -111.75) * mm, "end": v(208, -93) * mm});
            skLineSegment(sketch, "E33.12.0.25", {"start": v(210.9, -176.12) * mm, "end": v(211.3, -176.12) * mm});
            skLineSegment(sketch, "E33.12.0.26", {"start": v(210.9, -171.12) * mm, "end": v(211.3, -171.12) * mm});
            skLineSegment(sketch, "E33.12.0.27", {"start": v(210.9, -152.37) * mm, "end": v(211.3, -152.37) * mm});
            skLineSegment(sketch, "E33.12.0.28", {"start": v(210.9, -147.37) * mm, "end": v(211.3, -147.37) * mm});
            skLineSegment(sketch, "E33.12.0.29", {"start": v(210.9, -128.62) * mm, "end": v(211.3, -128.62) * mm});
            skLineSegment(sketch, "E33.12.0.30", {"start": v(210.9, -123.62) * mm, "end": v(211.3, -123.62) * mm});
            skLineSegment(sketch, "E33.12.0.31", {"start": v(210.9, -104.87) * mm, "end": v(211.3, -104.87) * mm});
            skLineSegment(sketch, "E33.12.0.32", {"start": v(210.9, -99.87) * mm, "end": v(211.3, -99.87) * mm});
            skLineSegment(sketch, "E33.12.0.33", {"start": v(208, -164.25) * mm, "end": v(208.4, -164.25) * mm});
            skLineSegment(sketch, "E33.12.0.34", {"start": v(208, -159.25) * mm, "end": v(208.4, -159.25) * mm});
            skLineSegment(sketch, "E33.12.0.35", {"start": v(211.3, -93) * mm, "end": v(208, -93) * mm, "construction": true});
            skLineSegment(sketch, "E33.12.0.36", {"start": v(208, -140.5) * mm, "end": v(208.4, -140.5) * mm});
            skLineSegment(sketch, "E33.12.0.37", {"start": v(208, -135.5) * mm, "end": v(208.4, -135.5) * mm});
            skLineSegment(sketch, "E33.12.0.38", {"start": v(208, -116.75) * mm, "end": v(208.4, -116.75) * mm});
            skLineSegment(sketch, "E33.12.0.39", {"start": v(210.9, -183) * mm, "end": v(211.3, -183) * mm});
            skLineSegment(sketch, "E33.12.0.40", {"start": v(210.9, -93) * mm, "end": v(211.3, -93) * mm});
            skLineSegment(sketch, "E33.12.0.41", {"start": v(211.3, -183) * mm, "end": v(208, -183) * mm, "construction": true});
            skLineSegment(sketch, "E33.12.0.42", {"start": v(208.4, -111.75) * mm, "end": v(208, -111.75) * mm});
            skLineSegment(sketch, "E33.12.0.43", {"start": v(208, -183) * mm, "end": v(208.4, -183) * mm});
            skLineSegment(sketch, "E33.12.0.44", {"start": v(208, -111.75) * mm, "end": v(208.4, -111.75) * mm});
            skLineSegment(sketch, "E33.12.0.45", {"start": v(208.4, -93) * mm, "end": v(208, -93) * mm});
            skLineSegment(sketch, "E33.13.0.0", {"start": v(216.75, -99.87) * mm, "end": v(216.75, -93) * mm});
            skLineSegment(sketch, "E33.13.0.1", {"start": v(213.85, -183) * mm, "end": v(213.85, -93) * mm, "construction": true});
            skLineSegment(sketch, "E33.13.0.2", {"start": v(217.15, -152.37) * mm, "end": v(217.15, -171.12) * mm});
            skLineSegment(sketch, "E33.13.0.3", {"start": v(216.75, -104.87) * mm, "end": v(216.75, -123.62) * mm});
            skLineSegment(sketch, "E33.13.0.4", {"start": v(214.25, -159.25) * mm, "end": v(214.25, -140.5) * mm});
            skLineSegment(sketch, "E33.13.0.5", {"start": v(217.15, -128.62) * mm, "end": v(217.15, -147.37) * mm});
            skLineSegment(sketch, "E33.13.0.6", {"start": v(216.75, -128.62) * mm, "end": v(216.75, -147.37) * mm});
            skLineSegment(sketch, "E33.13.0.7", {"start": v(213.85, -164.25) * mm, "end": v(213.85, -183) * mm});
            skLineSegment(sketch, "E33.13.0.8", {"start": v(214.25, -164.25) * mm, "end": v(214.25, -183) * mm});
            skLineSegment(sketch, "E33.13.0.9", {"start": v(216.75, -176.12) * mm, "end": v(216.75, -183) * mm});
            skLineSegment(sketch, "E33.13.0.10", {"start": v(217.15, -176.12) * mm, "end": v(217.15, -183) * mm});
            skLineSegment(sketch, "E33.13.0.11", {"start": v(217.15, -183) * mm, "end": v(217.15, -93) * mm, "construction": true});
            skLineSegment(sketch, "E33.13.0.12", {"start": v(216.75, -152.37) * mm, "end": v(216.75, -171.12) * mm});
            skLineSegment(sketch, "E33.13.0.13", {"start": v(213.85, -140.5) * mm, "end": v(213.85, -159.25) * mm});
            skLineSegment(sketch, "E33.13.0.14", {"start": v(213.85, -116.75) * mm, "end": v(213.85, -135.5) * mm});
            skLineSegment(sketch, "E33.13.0.15", {"start": v(214.25, -116.75) * mm, "end": v(214.25, -135.5) * mm});
            skLineSegment(sketch, "E33.13.0.16", {"start": v(217.15, -104.87) * mm, "end": v(217.15, -123.62) * mm});
            skLineSegment(sketch, "E33.13.0.17", {"start": v(213.85, -93) * mm, "end": v(213.85, -111.75) * mm});
            skLineSegment(sketch, "E33.13.0.18", {"start": v(214.25, -93) * mm, "end": v(214.25, -111.75) * mm});
            skLineSegment(sketch, "E33.13.0.19", {"start": v(217.15, -99.87) * mm, "end": v(217.15, -93) * mm});
            skLineSegment(sketch, "E33.13.0.20", {"start": v(213.85, -159.25) * mm, "end": v(213.85, -140.5) * mm});
            skLineSegment(sketch, "E33.13.0.21", {"start": v(213.85, -116.75) * mm, "end": v(213.85, -135.5) * mm});
            skLineSegment(sketch, "E33.13.0.22", {"start": v(214.25, -111.75) * mm, "end": v(214.25, -93) * mm});
            skLineSegment(sketch, "E33.13.0.23", {"start": v(213.85, -164.25) * mm, "end": v(213.85, -183) * mm});
            skLineSegment(sketch, "E33.13.0.24", {"start": v(213.85, -111.75) * mm, "end": v(213.85, -93) * mm});
            skLineSegment(sketch, "E33.13.0.25", {"start": v(216.75, -176.12) * mm, "end": v(217.15, -176.12) * mm});
            skLineSegment(sketch, "E33.13.0.26", {"start": v(216.75, -171.12) * mm, "end": v(217.15, -171.12) * mm});
            skLineSegment(sketch, "E33.13.0.27", {"start": v(216.75, -152.37) * mm, "end": v(217.15, -152.37) * mm});
            skLineSegment(sketch, "E33.13.0.28", {"start": v(216.75, -147.37) * mm, "end": v(217.15, -147.37) * mm});
            skLineSegment(sketch, "E33.13.0.29", {"start": v(216.75, -128.62) * mm, "end": v(217.15, -128.62) * mm});
            skLineSegment(sketch, "E33.13.0.30", {"start": v(216.75, -123.62) * mm, "end": v(217.15, -123.62) * mm});
            skLineSegment(sketch, "E33.13.0.31", {"start": v(216.75, -104.87) * mm, "end": v(217.15, -104.87) * mm});
            skLineSegment(sketch, "E33.13.0.32", {"start": v(216.75, -99.87) * mm, "end": v(217.15, -99.87) * mm});
            skLineSegment(sketch, "E33.13.0.33", {"start": v(213.85, -164.25) * mm, "end": v(214.25, -164.25) * mm});
            skLineSegment(sketch, "E33.13.0.34", {"start": v(213.85, -159.25) * mm, "end": v(214.25, -159.25) * mm});
            skLineSegment(sketch, "E33.13.0.35", {"start": v(217.15, -93) * mm, "end": v(213.85, -93) * mm, "construction": true});
            skLineSegment(sketch, "E33.13.0.36", {"start": v(213.85, -140.5) * mm, "end": v(214.25, -140.5) * mm});
            skLineSegment(sketch, "E33.13.0.37", {"start": v(213.85, -135.5) * mm, "end": v(214.25, -135.5) * mm});
            skLineSegment(sketch, "E33.13.0.38", {"start": v(213.85, -116.75) * mm, "end": v(214.25, -116.75) * mm});
            skLineSegment(sketch, "E33.13.0.39", {"start": v(216.75, -183) * mm, "end": v(217.15, -183) * mm});
            skLineSegment(sketch, "E33.13.0.40", {"start": v(216.75, -93) * mm, "end": v(217.15, -93) * mm});
            skLineSegment(sketch, "E33.13.0.41", {"start": v(217.15, -183) * mm, "end": v(213.85, -183) * mm, "construction": true});
            skLineSegment(sketch, "E33.13.0.42", {"start": v(214.25, -111.75) * mm, "end": v(213.85, -111.75) * mm});
            skLineSegment(sketch, "E33.13.0.43", {"start": v(213.85, -183) * mm, "end": v(214.25, -183) * mm});
            skLineSegment(sketch, "E33.13.0.44", {"start": v(213.85, -111.75) * mm, "end": v(214.25, -111.75) * mm});
            skLineSegment(sketch, "E33.13.0.45", {"start": v(214.25, -93) * mm, "end": v(213.85, -93) * mm});
            skLineSegment(sketch, "E33.14.0.0", {"start": v(222.6, -99.87) * mm, "end": v(222.6, -93) * mm});
            skLineSegment(sketch, "E33.14.0.1", {"start": v(219.7, -183) * mm, "end": v(219.7, -93) * mm, "construction": true});
            skLineSegment(sketch, "E33.14.0.2", {"start": v(223, -152.37) * mm, "end": v(223, -171.12) * mm});
            skLineSegment(sketch, "E33.14.0.3", {"start": v(222.6, -104.87) * mm, "end": v(222.6, -123.62) * mm});
            skLineSegment(sketch, "E33.14.0.4", {"start": v(220.1, -159.25) * mm, "end": v(220.1, -140.5) * mm});
            skLineSegment(sketch, "E33.14.0.5", {"start": v(223, -128.62) * mm, "end": v(223, -147.37) * mm});
            skLineSegment(sketch, "E33.14.0.6", {"start": v(222.6, -128.62) * mm, "end": v(222.6, -147.37) * mm});
            skLineSegment(sketch, "E33.14.0.7", {"start": v(219.7, -164.25) * mm, "end": v(219.7, -183) * mm});
            skLineSegment(sketch, "E33.14.0.8", {"start": v(220.1, -164.25) * mm, "end": v(220.1, -183) * mm});
            skLineSegment(sketch, "E33.14.0.9", {"start": v(222.6, -176.12) * mm, "end": v(222.6, -183) * mm});
            skLineSegment(sketch, "E33.14.0.10", {"start": v(223, -176.12) * mm, "end": v(223, -183) * mm});
            skLineSegment(sketch, "E33.14.0.11", {"start": v(223, -183) * mm, "end": v(223, -93) * mm, "construction": true});
            skLineSegment(sketch, "E33.14.0.12", {"start": v(222.6, -152.37) * mm, "end": v(222.6, -171.12) * mm});
            skLineSegment(sketch, "E33.14.0.13", {"start": v(219.7, -140.5) * mm, "end": v(219.7, -159.25) * mm});
            skLineSegment(sketch, "E33.14.0.14", {"start": v(219.7, -116.75) * mm, "end": v(219.7, -135.5) * mm});
            skLineSegment(sketch, "E33.14.0.15", {"start": v(220.1, -116.75) * mm, "end": v(220.1, -135.5) * mm});
            skLineSegment(sketch, "E33.14.0.16", {"start": v(223, -104.87) * mm, "end": v(223, -123.62) * mm});
            skLineSegment(sketch, "E33.14.0.17", {"start": v(219.7, -93) * mm, "end": v(219.7, -111.75) * mm});
            skLineSegment(sketch, "E33.14.0.18", {"start": v(220.1, -93) * mm, "end": v(220.1, -111.75) * mm});
            skLineSegment(sketch, "E33.14.0.19", {"start": v(223, -99.87) * mm, "end": v(223, -93) * mm});
            skLineSegment(sketch, "E33.14.0.20", {"start": v(219.7, -159.25) * mm, "end": v(219.7, -140.5) * mm});
            skLineSegment(sketch, "E33.14.0.21", {"start": v(219.7, -116.75) * mm, "end": v(219.7, -135.5) * mm});
            skLineSegment(sketch, "E33.14.0.22", {"start": v(220.1, -111.75) * mm, "end": v(220.1, -93) * mm});
            skLineSegment(sketch, "E33.14.0.23", {"start": v(219.7, -164.25) * mm, "end": v(219.7, -183) * mm});
            skLineSegment(sketch, "E33.14.0.24", {"start": v(219.7, -111.75) * mm, "end": v(219.7, -93) * mm});
            skLineSegment(sketch, "E33.14.0.25", {"start": v(222.6, -176.12) * mm, "end": v(223, -176.12) * mm});
            skLineSegment(sketch, "E33.14.0.26", {"start": v(222.6, -171.12) * mm, "end": v(223, -171.12) * mm});
            skLineSegment(sketch, "E33.14.0.27", {"start": v(222.6, -152.37) * mm, "end": v(223, -152.37) * mm});
            skLineSegment(sketch, "E33.14.0.28", {"start": v(222.6, -147.37) * mm, "end": v(223, -147.37) * mm});
            skLineSegment(sketch, "E33.14.0.29", {"start": v(222.6, -128.62) * mm, "end": v(223, -128.62) * mm});
            skLineSegment(sketch, "E33.14.0.30", {"start": v(222.6, -123.62) * mm, "end": v(223, -123.62) * mm});
            skLineSegment(sketch, "E33.14.0.31", {"start": v(222.6, -104.87) * mm, "end": v(223, -104.87) * mm});
            skLineSegment(sketch, "E33.14.0.32", {"start": v(222.6, -99.87) * mm, "end": v(223, -99.87) * mm});
            skLineSegment(sketch, "E33.14.0.33", {"start": v(219.7, -164.25) * mm, "end": v(220.1, -164.25) * mm});
            skLineSegment(sketch, "E33.14.0.34", {"start": v(219.7, -159.25) * mm, "end": v(220.1, -159.25) * mm});
            skLineSegment(sketch, "E33.14.0.35", {"start": v(223, -93) * mm, "end": v(219.7, -93) * mm, "construction": true});
            skLineSegment(sketch, "E33.14.0.36", {"start": v(219.7, -140.5) * mm, "end": v(220.1, -140.5) * mm});
            skLineSegment(sketch, "E33.14.0.37", {"start": v(219.7, -135.5) * mm, "end": v(220.1, -135.5) * mm});
            skLineSegment(sketch, "E33.14.0.38", {"start": v(219.7, -116.75) * mm, "end": v(220.1, -116.75) * mm});
            skLineSegment(sketch, "E33.14.0.39", {"start": v(222.6, -183) * mm, "end": v(223, -183) * mm});
            skLineSegment(sketch, "E33.14.0.40", {"start": v(222.6, -93) * mm, "end": v(223, -93) * mm});
            skLineSegment(sketch, "E33.14.0.41", {"start": v(223, -183) * mm, "end": v(219.7, -183) * mm, "construction": true});
            skLineSegment(sketch, "E33.14.0.42", {"start": v(220.1, -111.75) * mm, "end": v(219.7, -111.75) * mm});
            skLineSegment(sketch, "E33.14.0.43", {"start": v(219.7, -183) * mm, "end": v(220.1, -183) * mm});
            skLineSegment(sketch, "E33.14.0.44", {"start": v(219.7, -111.75) * mm, "end": v(220.1, -111.75) * mm});
            skLineSegment(sketch, "E33.14.0.45", {"start": v(220.1, -93) * mm, "end": v(219.7, -93) * mm});
            skLineSegment(sketch, "E33.15.0.0", {"start": v(228.45, -99.87) * mm, "end": v(228.45, -93) * mm});
            skLineSegment(sketch, "E33.15.0.1", {"start": v(225.55, -183) * mm, "end": v(225.55, -93) * mm, "construction": true});
            skLineSegment(sketch, "E33.15.0.2", {"start": v(228.85, -152.37) * mm, "end": v(228.85, -171.12) * mm});
            skLineSegment(sketch, "E33.15.0.3", {"start": v(228.45, -104.87) * mm, "end": v(228.45, -123.62) * mm});
            skLineSegment(sketch, "E33.15.0.4", {"start": v(225.95, -159.25) * mm, "end": v(225.95, -140.5) * mm});
            skLineSegment(sketch, "E33.15.0.5", {"start": v(228.85, -128.62) * mm, "end": v(228.85, -147.37) * mm});
            skLineSegment(sketch, "E33.15.0.6", {"start": v(228.45, -128.62) * mm, "end": v(228.45, -147.37) * mm});
            skLineSegment(sketch, "E33.15.0.7", {"start": v(225.55, -164.25) * mm, "end": v(225.55, -183) * mm});
            skLineSegment(sketch, "E33.15.0.8", {"start": v(225.95, -164.25) * mm, "end": v(225.95, -183) * mm});
            skLineSegment(sketch, "E33.15.0.9", {"start": v(228.45, -176.12) * mm, "end": v(228.45, -183) * mm});
            skLineSegment(sketch, "E33.15.0.10", {"start": v(228.85, -176.12) * mm, "end": v(228.85, -183) * mm});
            skLineSegment(sketch, "E33.15.0.11", {"start": v(228.85, -183) * mm, "end": v(228.85, -93) * mm, "construction": true});
            skLineSegment(sketch, "E33.15.0.12", {"start": v(228.45, -152.37) * mm, "end": v(228.45, -171.12) * mm});
            skLineSegment(sketch, "E33.15.0.13", {"start": v(225.55, -140.5) * mm, "end": v(225.55, -159.25) * mm});
            skLineSegment(sketch, "E33.15.0.14", {"start": v(225.55, -116.75) * mm, "end": v(225.55, -135.5) * mm});
            skLineSegment(sketch, "E33.15.0.15", {"start": v(225.95, -116.75) * mm, "end": v(225.95, -135.5) * mm});
            skLineSegment(sketch, "E33.15.0.16", {"start": v(228.85, -104.87) * mm, "end": v(228.85, -123.62) * mm});
            skLineSegment(sketch, "E33.15.0.17", {"start": v(225.55, -93) * mm, "end": v(225.55, -111.75) * mm});
            skLineSegment(sketch, "E33.15.0.18", {"start": v(225.95, -93) * mm, "end": v(225.95, -111.75) * mm});
            skLineSegment(sketch, "E33.15.0.19", {"start": v(228.85, -99.87) * mm, "end": v(228.85, -93) * mm});
            skLineSegment(sketch, "E33.15.0.20", {"start": v(225.55, -159.25) * mm, "end": v(225.55, -140.5) * mm});
            skLineSegment(sketch, "E33.15.0.21", {"start": v(225.55, -116.75) * mm, "end": v(225.55, -135.5) * mm});
            skLineSegment(sketch, "E33.15.0.22", {"start": v(225.95, -111.75) * mm, "end": v(225.95, -93) * mm});
            skLineSegment(sketch, "E33.15.0.23", {"start": v(225.55, -164.25) * mm, "end": v(225.55, -183) * mm});
            skLineSegment(sketch, "E33.15.0.24", {"start": v(225.55, -111.75) * mm, "end": v(225.55, -93) * mm});
            skLineSegment(sketch, "E33.15.0.25", {"start": v(228.45, -176.12) * mm, "end": v(228.85, -176.12) * mm});
            skLineSegment(sketch, "E33.15.0.26", {"start": v(228.45, -171.12) * mm, "end": v(228.85, -171.12) * mm});
            skLineSegment(sketch, "E33.15.0.27", {"start": v(228.45, -152.37) * mm, "end": v(228.85, -152.37) * mm});
            skLineSegment(sketch, "E33.15.0.28", {"start": v(228.45, -147.37) * mm, "end": v(228.85, -147.37) * mm});
            skLineSegment(sketch, "E33.15.0.29", {"start": v(228.45, -128.62) * mm, "end": v(228.85, -128.62) * mm});
            skLineSegment(sketch, "E33.15.0.30", {"start": v(228.45, -123.62) * mm, "end": v(228.85, -123.62) * mm});
            skLineSegment(sketch, "E33.15.0.31", {"start": v(228.45, -104.87) * mm, "end": v(228.85, -104.87) * mm});
            skLineSegment(sketch, "E33.15.0.32", {"start": v(228.45, -99.87) * mm, "end": v(228.85, -99.87) * mm});
            skLineSegment(sketch, "E33.15.0.33", {"start": v(225.55, -164.25) * mm, "end": v(225.95, -164.25) * mm});
            skLineSegment(sketch, "E33.15.0.34", {"start": v(225.55, -159.25) * mm, "end": v(225.95, -159.25) * mm});
            skLineSegment(sketch, "E33.15.0.35", {"start": v(228.85, -93) * mm, "end": v(225.55, -93) * mm, "construction": true});
            skLineSegment(sketch, "E33.15.0.36", {"start": v(225.55, -140.5) * mm, "end": v(225.95, -140.5) * mm});
            skLineSegment(sketch, "E33.15.0.37", {"start": v(225.55, -135.5) * mm, "end": v(225.95, -135.5) * mm});
            skLineSegment(sketch, "E33.15.0.38", {"start": v(225.55, -116.75) * mm, "end": v(225.95, -116.75) * mm});
            skLineSegment(sketch, "E33.15.0.39", {"start": v(228.45, -183) * mm, "end": v(228.85, -183) * mm});
            skLineSegment(sketch, "E33.15.0.40", {"start": v(228.45, -93) * mm, "end": v(228.85, -93) * mm});
            skLineSegment(sketch, "E33.15.0.41", {"start": v(228.85, -183) * mm, "end": v(225.55, -183) * mm, "construction": true});
            skLineSegment(sketch, "E33.15.0.42", {"start": v(225.95, -111.75) * mm, "end": v(225.55, -111.75) * mm});
            skLineSegment(sketch, "E33.15.0.43", {"start": v(225.55, -183) * mm, "end": v(225.95, -183) * mm});
            skLineSegment(sketch, "E33.15.0.44", {"start": v(225.55, -111.75) * mm, "end": v(225.95, -111.75) * mm});
            skLineSegment(sketch, "E33.15.0.45", {"start": v(225.95, -93) * mm, "end": v(225.55, -93) * mm});
            skLineSegment(sketch, "E33.16.0.0", {"start": v(234.3, -99.87) * mm, "end": v(234.3, -93) * mm});
            skLineSegment(sketch, "E33.16.0.1", {"start": v(231.4, -183) * mm, "end": v(231.4, -93) * mm, "construction": true});
            skLineSegment(sketch, "E33.16.0.2", {"start": v(234.7, -152.37) * mm, "end": v(234.7, -171.12) * mm});
            skLineSegment(sketch, "E33.16.0.3", {"start": v(234.3, -104.87) * mm, "end": v(234.3, -123.62) * mm});
            skLineSegment(sketch, "E33.16.0.4", {"start": v(231.8, -159.25) * mm, "end": v(231.8, -140.5) * mm});
            skLineSegment(sketch, "E33.16.0.5", {"start": v(234.7, -128.62) * mm, "end": v(234.7, -147.37) * mm});
            skLineSegment(sketch, "E33.16.0.6", {"start": v(234.3, -128.62) * mm, "end": v(234.3, -147.37) * mm});
            skLineSegment(sketch, "E33.16.0.7", {"start": v(231.4, -164.25) * mm, "end": v(231.4, -183) * mm});
            skLineSegment(sketch, "E33.16.0.8", {"start": v(231.8, -164.25) * mm, "end": v(231.8, -183) * mm});
            skLineSegment(sketch, "E33.16.0.9", {"start": v(234.3, -176.12) * mm, "end": v(234.3, -183) * mm});
            skLineSegment(sketch, "E33.16.0.10", {"start": v(234.7, -176.12) * mm, "end": v(234.7, -183) * mm});
            skLineSegment(sketch, "E33.16.0.11", {"start": v(234.7, -183) * mm, "end": v(234.7, -93) * mm, "construction": true});
            skLineSegment(sketch, "E33.16.0.12", {"start": v(234.3, -152.37) * mm, "end": v(234.3, -171.12) * mm});
            skLineSegment(sketch, "E33.16.0.13", {"start": v(231.4, -140.5) * mm, "end": v(231.4, -159.25) * mm});
            skLineSegment(sketch, "E33.16.0.14", {"start": v(231.4, -116.75) * mm, "end": v(231.4, -135.5) * mm});
            skLineSegment(sketch, "E33.16.0.15", {"start": v(231.8, -116.75) * mm, "end": v(231.8, -135.5) * mm});
            skLineSegment(sketch, "E33.16.0.16", {"start": v(234.7, -104.87) * mm, "end": v(234.7, -123.62) * mm});
            skLineSegment(sketch, "E33.16.0.17", {"start": v(231.4, -93) * mm, "end": v(231.4, -111.75) * mm});
            skLineSegment(sketch, "E33.16.0.18", {"start": v(231.8, -93) * mm, "end": v(231.8, -111.75) * mm});
            skLineSegment(sketch, "E33.16.0.19", {"start": v(234.7, -99.87) * mm, "end": v(234.7, -93) * mm});
            skLineSegment(sketch, "E33.16.0.20", {"start": v(231.4, -159.25) * mm, "end": v(231.4, -140.5) * mm});
            skLineSegment(sketch, "E33.16.0.21", {"start": v(231.4, -116.75) * mm, "end": v(231.4, -135.5) * mm});
            skLineSegment(sketch, "E33.16.0.22", {"start": v(231.8, -111.75) * mm, "end": v(231.8, -93) * mm});
            skLineSegment(sketch, "E33.16.0.23", {"start": v(231.4, -164.25) * mm, "end": v(231.4, -183) * mm});
            skLineSegment(sketch, "E33.16.0.24", {"start": v(231.4, -111.75) * mm, "end": v(231.4, -93) * mm});
            skLineSegment(sketch, "E33.16.0.25", {"start": v(234.3, -176.12) * mm, "end": v(234.7, -176.12) * mm});
            skLineSegment(sketch, "E33.16.0.26", {"start": v(234.3, -171.12) * mm, "end": v(234.7, -171.12) * mm});
            skLineSegment(sketch, "E33.16.0.27", {"start": v(234.3, -152.37) * mm, "end": v(234.7, -152.37) * mm});
            skLineSegment(sketch, "E33.16.0.28", {"start": v(234.3, -147.37) * mm, "end": v(234.7, -147.37) * mm});
            skLineSegment(sketch, "E33.16.0.29", {"start": v(234.3, -128.62) * mm, "end": v(234.7, -128.62) * mm});
            skLineSegment(sketch, "E33.16.0.30", {"start": v(234.3, -123.62) * mm, "end": v(234.7, -123.62) * mm});
            skLineSegment(sketch, "E33.16.0.31", {"start": v(234.3, -104.87) * mm, "end": v(234.7, -104.87) * mm});
            skLineSegment(sketch, "E33.16.0.32", {"start": v(234.3, -99.87) * mm, "end": v(234.7, -99.87) * mm});
            skLineSegment(sketch, "E33.16.0.33", {"start": v(231.4, -164.25) * mm, "end": v(231.8, -164.25) * mm});
            skLineSegment(sketch, "E33.16.0.34", {"start": v(231.4, -159.25) * mm, "end": v(231.8, -159.25) * mm});
            skLineSegment(sketch, "E33.16.0.35", {"start": v(234.7, -93) * mm, "end": v(231.4, -93) * mm, "construction": true});
            skLineSegment(sketch, "E33.16.0.36", {"start": v(231.4, -140.5) * mm, "end": v(231.8, -140.5) * mm});
            skLineSegment(sketch, "E33.16.0.37", {"start": v(231.4, -135.5) * mm, "end": v(231.8, -135.5) * mm});
            skLineSegment(sketch, "E33.16.0.38", {"start": v(231.4, -116.75) * mm, "end": v(231.8, -116.75) * mm});
            skLineSegment(sketch, "E33.16.0.39", {"start": v(234.3, -183) * mm, "end": v(234.7, -183) * mm});
            skLineSegment(sketch, "E33.16.0.40", {"start": v(234.3, -93) * mm, "end": v(234.7, -93) * mm});
            skLineSegment(sketch, "E33.16.0.41", {"start": v(234.7, -183) * mm, "end": v(231.4, -183) * mm, "construction": true});
            skLineSegment(sketch, "E33.16.0.42", {"start": v(231.8, -111.75) * mm, "end": v(231.4, -111.75) * mm});
            skLineSegment(sketch, "E33.16.0.43", {"start": v(231.4, -183) * mm, "end": v(231.8, -183) * mm});
            skLineSegment(sketch, "E33.16.0.44", {"start": v(231.4, -111.75) * mm, "end": v(231.8, -111.75) * mm});
            skLineSegment(sketch, "E33.16.0.45", {"start": v(231.8, -93) * mm, "end": v(231.4, -93) * mm});
            skLineSegment(sketch, "E33.17.0.0", {"start": v(240.15, -99.87) * mm, "end": v(240.15, -93) * mm});
            skLineSegment(sketch, "E33.17.0.1", {"start": v(237.25, -183) * mm, "end": v(237.25, -93) * mm, "construction": true});
            skLineSegment(sketch, "E33.17.0.2", {"start": v(240.55, -152.37) * mm, "end": v(240.55, -171.12) * mm});
            skLineSegment(sketch, "E33.17.0.3", {"start": v(240.15, -104.87) * mm, "end": v(240.15, -123.62) * mm});
            skLineSegment(sketch, "E33.17.0.4", {"start": v(237.65, -159.25) * mm, "end": v(237.65, -140.5) * mm});
            skLineSegment(sketch, "E33.17.0.5", {"start": v(240.55, -128.62) * mm, "end": v(240.55, -147.37) * mm});
            skLineSegment(sketch, "E33.17.0.6", {"start": v(240.15, -128.62) * mm, "end": v(240.15, -147.37) * mm});
            skLineSegment(sketch, "E33.17.0.7", {"start": v(237.25, -164.25) * mm, "end": v(237.25, -183) * mm});
            skLineSegment(sketch, "E33.17.0.8", {"start": v(237.65, -164.25) * mm, "end": v(237.65, -183) * mm});
            skLineSegment(sketch, "E33.17.0.9", {"start": v(240.15, -176.12) * mm, "end": v(240.15, -183) * mm});
            skLineSegment(sketch, "E33.17.0.10", {"start": v(240.55, -176.12) * mm, "end": v(240.55, -183) * mm});
            skLineSegment(sketch, "E33.17.0.11", {"start": v(240.55, -183) * mm, "end": v(240.55, -93) * mm, "construction": true});
            skLineSegment(sketch, "E33.17.0.12", {"start": v(240.15, -152.37) * mm, "end": v(240.15, -171.12) * mm});
            skLineSegment(sketch, "E33.17.0.13", {"start": v(237.25, -140.5) * mm, "end": v(237.25, -159.25) * mm});
            skLineSegment(sketch, "E33.17.0.14", {"start": v(237.25, -116.75) * mm, "end": v(237.25, -135.5) * mm});
            skLineSegment(sketch, "E33.17.0.15", {"start": v(237.65, -116.75) * mm, "end": v(237.65, -135.5) * mm});
            skLineSegment(sketch, "E33.17.0.16", {"start": v(240.55, -104.87) * mm, "end": v(240.55, -123.62) * mm});
            skLineSegment(sketch, "E33.17.0.17", {"start": v(237.25, -93) * mm, "end": v(237.25, -111.75) * mm});
            skLineSegment(sketch, "E33.17.0.18", {"start": v(237.65, -93) * mm, "end": v(237.65, -111.75) * mm});
            skLineSegment(sketch, "E33.17.0.19", {"start": v(240.55, -99.87) * mm, "end": v(240.55, -93) * mm});
            skLineSegment(sketch, "E33.17.0.20", {"start": v(237.25, -159.25) * mm, "end": v(237.25, -140.5) * mm});
            skLineSegment(sketch, "E33.17.0.21", {"start": v(237.25, -116.75) * mm, "end": v(237.25, -135.5) * mm});
            skLineSegment(sketch, "E33.17.0.22", {"start": v(237.65, -111.75) * mm, "end": v(237.65, -93) * mm});
            skLineSegment(sketch, "E33.17.0.23", {"start": v(237.25, -164.25) * mm, "end": v(237.25, -183) * mm});
            skLineSegment(sketch, "E33.17.0.24", {"start": v(237.25, -111.75) * mm, "end": v(237.25, -93) * mm});
            skLineSegment(sketch, "E33.17.0.25", {"start": v(240.15, -176.12) * mm, "end": v(240.55, -176.12) * mm});
            skLineSegment(sketch, "E33.17.0.26", {"start": v(240.15, -171.12) * mm, "end": v(240.55, -171.12) * mm});
            skLineSegment(sketch, "E33.17.0.27", {"start": v(240.15, -152.37) * mm, "end": v(240.55, -152.37) * mm});
            skLineSegment(sketch, "E33.17.0.28", {"start": v(240.15, -147.37) * mm, "end": v(240.55, -147.37) * mm});
            skLineSegment(sketch, "E33.17.0.29", {"start": v(240.15, -128.62) * mm, "end": v(240.55, -128.62) * mm});
            skLineSegment(sketch, "E33.17.0.30", {"start": v(240.15, -123.62) * mm, "end": v(240.55, -123.62) * mm});
            skLineSegment(sketch, "E33.17.0.31", {"start": v(240.15, -104.87) * mm, "end": v(240.55, -104.87) * mm});
            skLineSegment(sketch, "E33.17.0.32", {"start": v(240.15, -99.87) * mm, "end": v(240.55, -99.87) * mm});
            skLineSegment(sketch, "E33.17.0.33", {"start": v(237.25, -164.25) * mm, "end": v(237.65, -164.25) * mm});
            skLineSegment(sketch, "E33.17.0.34", {"start": v(237.25, -159.25) * mm, "end": v(237.65, -159.25) * mm});
            skLineSegment(sketch, "E33.17.0.35", {"start": v(240.55, -93) * mm, "end": v(237.25, -93) * mm, "construction": true});
            skLineSegment(sketch, "E33.17.0.36", {"start": v(237.25, -140.5) * mm, "end": v(237.65, -140.5) * mm});
            skLineSegment(sketch, "E33.17.0.37", {"start": v(237.25, -135.5) * mm, "end": v(237.65, -135.5) * mm});
            skLineSegment(sketch, "E33.17.0.38", {"start": v(237.25, -116.75) * mm, "end": v(237.65, -116.75) * mm});
            skLineSegment(sketch, "E33.17.0.39", {"start": v(240.15, -183) * mm, "end": v(240.55, -183) * mm});
            skLineSegment(sketch, "E33.17.0.40", {"start": v(240.15, -93) * mm, "end": v(240.55, -93) * mm});
            skLineSegment(sketch, "E33.17.0.41", {"start": v(240.55, -183) * mm, "end": v(237.25, -183) * mm, "construction": true});
            skLineSegment(sketch, "E33.17.0.42", {"start": v(237.65, -111.75) * mm, "end": v(237.25, -111.75) * mm});
            skLineSegment(sketch, "E33.17.0.43", {"start": v(237.25, -183) * mm, "end": v(237.65, -183) * mm});
            skLineSegment(sketch, "E33.17.0.44", {"start": v(237.25, -111.75) * mm, "end": v(237.65, -111.75) * mm});
            skLineSegment(sketch, "E33.17.0.45", {"start": v(237.65, -93) * mm, "end": v(237.25, -93) * mm});
            skLineSegment(sketch, "E33.18.0.0", {"start": v(246, -99.87) * mm, "end": v(246, -93) * mm});
            skLineSegment(sketch, "E33.18.0.1", {"start": v(243.1, -183) * mm, "end": v(243.1, -93) * mm, "construction": true});
            skLineSegment(sketch, "E33.18.0.2", {"start": v(246.4, -152.37) * mm, "end": v(246.4, -171.12) * mm});
            skLineSegment(sketch, "E33.18.0.3", {"start": v(246, -104.87) * mm, "end": v(246, -123.62) * mm});
            skLineSegment(sketch, "E33.18.0.4", {"start": v(243.5, -159.25) * mm, "end": v(243.5, -140.5) * mm});
            skLineSegment(sketch, "E33.18.0.5", {"start": v(246.4, -128.62) * mm, "end": v(246.4, -147.37) * mm});
            skLineSegment(sketch, "E33.18.0.6", {"start": v(246, -128.62) * mm, "end": v(246, -147.37) * mm});
            skLineSegment(sketch, "E33.18.0.7", {"start": v(243.1, -164.25) * mm, "end": v(243.1, -183) * mm});
            skLineSegment(sketch, "E33.18.0.8", {"start": v(243.5, -164.25) * mm, "end": v(243.5, -183) * mm});
            skLineSegment(sketch, "E33.18.0.9", {"start": v(246, -176.12) * mm, "end": v(246, -183) * mm});
            skLineSegment(sketch, "E33.18.0.10", {"start": v(246.4, -176.12) * mm, "end": v(246.4, -183) * mm});
            skLineSegment(sketch, "E33.18.0.11", {"start": v(246.4, -183) * mm, "end": v(246.4, -93) * mm, "construction": true});
            skLineSegment(sketch, "E33.18.0.12", {"start": v(246, -152.37) * mm, "end": v(246, -171.12) * mm});
            skLineSegment(sketch, "E33.18.0.13", {"start": v(243.1, -140.5) * mm, "end": v(243.1, -159.25) * mm});
            skLineSegment(sketch, "E33.18.0.14", {"start": v(243.1, -116.75) * mm, "end": v(243.1, -135.5) * mm});
            skLineSegment(sketch, "E33.18.0.15", {"start": v(243.5, -116.75) * mm, "end": v(243.5, -135.5) * mm});
            skLineSegment(sketch, "E33.18.0.16", {"start": v(246.4, -104.87) * mm, "end": v(246.4, -123.62) * mm});
            skLineSegment(sketch, "E33.18.0.17", {"start": v(243.1, -93) * mm, "end": v(243.1, -111.75) * mm});
            skLineSegment(sketch, "E33.18.0.18", {"start": v(243.5, -93) * mm, "end": v(243.5, -111.75) * mm});
            skLineSegment(sketch, "E33.18.0.19", {"start": v(246.4, -99.87) * mm, "end": v(246.4, -93) * mm});
            skLineSegment(sketch, "E33.18.0.20", {"start": v(243.1, -159.25) * mm, "end": v(243.1, -140.5) * mm});
            skLineSegment(sketch, "E33.18.0.21", {"start": v(243.1, -116.75) * mm, "end": v(243.1, -135.5) * mm});
            skLineSegment(sketch, "E33.18.0.22", {"start": v(243.5, -111.75) * mm, "end": v(243.5, -93) * mm});
            skLineSegment(sketch, "E33.18.0.23", {"start": v(243.1, -164.25) * mm, "end": v(243.1, -183) * mm});
            skLineSegment(sketch, "E33.18.0.24", {"start": v(243.1, -111.75) * mm, "end": v(243.1, -93) * mm});
            skLineSegment(sketch, "E33.18.0.25", {"start": v(246, -176.12) * mm, "end": v(246.4, -176.12) * mm});
            skLineSegment(sketch, "E33.18.0.26", {"start": v(246, -171.12) * mm, "end": v(246.4, -171.12) * mm});
            skLineSegment(sketch, "E33.18.0.27", {"start": v(246, -152.37) * mm, "end": v(246.4, -152.37) * mm});
            skLineSegment(sketch, "E33.18.0.28", {"start": v(246, -147.37) * mm, "end": v(246.4, -147.37) * mm});
            skLineSegment(sketch, "E33.18.0.29", {"start": v(246, -128.62) * mm, "end": v(246.4, -128.62) * mm});
            skLineSegment(sketch, "E33.18.0.30", {"start": v(246, -123.62) * mm, "end": v(246.4, -123.62) * mm});
            skLineSegment(sketch, "E33.18.0.31", {"start": v(246, -104.87) * mm, "end": v(246.4, -104.87) * mm});
            skLineSegment(sketch, "E33.18.0.32", {"start": v(246, -99.87) * mm, "end": v(246.4, -99.87) * mm});
            skLineSegment(sketch, "E33.18.0.33", {"start": v(243.1, -164.25) * mm, "end": v(243.5, -164.25) * mm});
            skLineSegment(sketch, "E33.18.0.34", {"start": v(243.1, -159.25) * mm, "end": v(243.5, -159.25) * mm});
            skLineSegment(sketch, "E33.18.0.35", {"start": v(246.4, -93) * mm, "end": v(243.1, -93) * mm, "construction": true});
            skLineSegment(sketch, "E33.18.0.36", {"start": v(243.1, -140.5) * mm, "end": v(243.5, -140.5) * mm});
            skLineSegment(sketch, "E33.18.0.37", {"start": v(243.1, -135.5) * mm, "end": v(243.5, -135.5) * mm});
            skLineSegment(sketch, "E33.18.0.38", {"start": v(243.1, -116.75) * mm, "end": v(243.5, -116.75) * mm});
            skLineSegment(sketch, "E33.18.0.39", {"start": v(246, -183) * mm, "end": v(246.4, -183) * mm});
            skLineSegment(sketch, "E33.18.0.40", {"start": v(246, -93) * mm, "end": v(246.4, -93) * mm});
            skLineSegment(sketch, "E33.18.0.41", {"start": v(246.4, -183) * mm, "end": v(243.1, -183) * mm, "construction": true});
            skLineSegment(sketch, "E33.18.0.42", {"start": v(243.5, -111.75) * mm, "end": v(243.1, -111.75) * mm});
            skLineSegment(sketch, "E33.18.0.43", {"start": v(243.1, -183) * mm, "end": v(243.5, -183) * mm});
            skLineSegment(sketch, "E33.18.0.44", {"start": v(243.1, -111.75) * mm, "end": v(243.5, -111.75) * mm});
            skLineSegment(sketch, "E33.18.0.45", {"start": v(243.5, -93) * mm, "end": v(243.1, -93) * mm});
            skLineSegment(sketch, "E33.19.0.0", {"start": v(251.85, -99.87) * mm, "end": v(251.85, -93) * mm});
            skLineSegment(sketch, "E33.19.0.1", {"start": v(248.95, -183) * mm, "end": v(248.95, -93) * mm, "construction": true});
            skLineSegment(sketch, "E33.19.0.2", {"start": v(252.25, -152.37) * mm, "end": v(252.25, -171.12) * mm});
            skLineSegment(sketch, "E33.19.0.3", {"start": v(251.85, -104.87) * mm, "end": v(251.85, -123.62) * mm});
            skLineSegment(sketch, "E33.19.0.4", {"start": v(249.35, -159.25) * mm, "end": v(249.35, -140.5) * mm});
            skLineSegment(sketch, "E33.19.0.5", {"start": v(252.25, -128.62) * mm, "end": v(252.25, -147.37) * mm});
            skLineSegment(sketch, "E33.19.0.6", {"start": v(251.85, -128.62) * mm, "end": v(251.85, -147.37) * mm});
            skLineSegment(sketch, "E33.19.0.7", {"start": v(248.95, -164.25) * mm, "end": v(248.95, -183) * mm});
            skLineSegment(sketch, "E33.19.0.8", {"start": v(249.35, -164.25) * mm, "end": v(249.35, -183) * mm});
            skLineSegment(sketch, "E33.19.0.9", {"start": v(251.85, -176.12) * mm, "end": v(251.85, -183) * mm});
            skLineSegment(sketch, "E33.19.0.10", {"start": v(252.25, -176.12) * mm, "end": v(252.25, -183) * mm});
            skLineSegment(sketch, "E33.19.0.11", {"start": v(252.25, -183) * mm, "end": v(252.25, -93) * mm, "construction": true});
            skLineSegment(sketch, "E33.19.0.12", {"start": v(251.85, -152.37) * mm, "end": v(251.85, -171.12) * mm});
            skLineSegment(sketch, "E33.19.0.13", {"start": v(248.95, -140.5) * mm, "end": v(248.95, -159.25) * mm});
            skLineSegment(sketch, "E33.19.0.14", {"start": v(248.95, -116.75) * mm, "end": v(248.95, -135.5) * mm});
            skLineSegment(sketch, "E33.19.0.15", {"start": v(249.35, -116.75) * mm, "end": v(249.35, -135.5) * mm});
            skLineSegment(sketch, "E33.19.0.16", {"start": v(252.25, -104.87) * mm, "end": v(252.25, -123.62) * mm});
            skLineSegment(sketch, "E33.19.0.17", {"start": v(248.95, -93) * mm, "end": v(248.95, -111.75) * mm});
            skLineSegment(sketch, "E33.19.0.18", {"start": v(249.35, -93) * mm, "end": v(249.35, -111.75) * mm});
            skLineSegment(sketch, "E33.19.0.19", {"start": v(252.25, -99.87) * mm, "end": v(252.25, -93) * mm});
            skLineSegment(sketch, "E33.19.0.20", {"start": v(248.95, -159.25) * mm, "end": v(248.95, -140.5) * mm});
            skLineSegment(sketch, "E33.19.0.21", {"start": v(248.95, -116.75) * mm, "end": v(248.95, -135.5) * mm});
            skLineSegment(sketch, "E33.19.0.22", {"start": v(249.35, -111.75) * mm, "end": v(249.35, -93) * mm});
            skLineSegment(sketch, "E33.19.0.23", {"start": v(248.95, -164.25) * mm, "end": v(248.95, -183) * mm});
            skLineSegment(sketch, "E33.19.0.24", {"start": v(248.95, -111.75) * mm, "end": v(248.95, -93) * mm});
            skLineSegment(sketch, "E33.19.0.25", {"start": v(251.85, -176.12) * mm, "end": v(252.25, -176.12) * mm});
            skLineSegment(sketch, "E33.19.0.26", {"start": v(251.85, -171.12) * mm, "end": v(252.25, -171.12) * mm});
            skLineSegment(sketch, "E33.19.0.27", {"start": v(251.85, -152.37) * mm, "end": v(252.25, -152.37) * mm});
            skLineSegment(sketch, "E33.19.0.28", {"start": v(251.85, -147.37) * mm, "end": v(252.25, -147.37) * mm});
            skLineSegment(sketch, "E33.19.0.29", {"start": v(251.85, -128.62) * mm, "end": v(252.25, -128.62) * mm});
            skLineSegment(sketch, "E33.19.0.30", {"start": v(251.85, -123.62) * mm, "end": v(252.25, -123.62) * mm});
            skLineSegment(sketch, "E33.19.0.31", {"start": v(251.85, -104.87) * mm, "end": v(252.25, -104.87) * mm});
            skLineSegment(sketch, "E33.19.0.32", {"start": v(251.85, -99.87) * mm, "end": v(252.25, -99.87) * mm});
            skLineSegment(sketch, "E33.19.0.33", {"start": v(248.95, -164.25) * mm, "end": v(249.35, -164.25) * mm});
            skLineSegment(sketch, "E33.19.0.34", {"start": v(248.95, -159.25) * mm, "end": v(249.35, -159.25) * mm});
            skLineSegment(sketch, "E33.19.0.35", {"start": v(252.25, -93) * mm, "end": v(248.95, -93) * mm, "construction": true});
            skLineSegment(sketch, "E33.19.0.36", {"start": v(248.95, -140.5) * mm, "end": v(249.35, -140.5) * mm});
            skLineSegment(sketch, "E33.19.0.37", {"start": v(248.95, -135.5) * mm, "end": v(249.35, -135.5) * mm});
            skLineSegment(sketch, "E33.19.0.38", {"start": v(248.95, -116.75) * mm, "end": v(249.35, -116.75) * mm});
            skLineSegment(sketch, "E33.19.0.39", {"start": v(251.85, -183) * mm, "end": v(252.25, -183) * mm});
            skLineSegment(sketch, "E33.19.0.40", {"start": v(251.85, -93) * mm, "end": v(252.25, -93) * mm});
            skLineSegment(sketch, "E33.19.0.41", {"start": v(252.25, -183) * mm, "end": v(248.95, -183) * mm, "construction": true});
            skLineSegment(sketch, "E33.19.0.42", {"start": v(249.35, -111.75) * mm, "end": v(248.95, -111.75) * mm});
            skLineSegment(sketch, "E33.19.0.43", {"start": v(248.95, -183) * mm, "end": v(249.35, -183) * mm});
            skLineSegment(sketch, "E33.19.0.44", {"start": v(248.95, -111.75) * mm, "end": v(249.35, -111.75) * mm});
            skLineSegment(sketch, "E33.19.0.45", {"start": v(249.35, -93) * mm, "end": v(248.95, -93) * mm});
            skLineSegment(sketch, "E33.20.0.0", {"start": v(257.7, -99.87) * mm, "end": v(257.7, -93) * mm});
            skLineSegment(sketch, "E33.20.0.1", {"start": v(254.8, -183) * mm, "end": v(254.8, -93) * mm, "construction": true});
            skLineSegment(sketch, "E33.20.0.2", {"start": v(258.1, -152.37) * mm, "end": v(258.1, -171.12) * mm});
            skLineSegment(sketch, "E33.20.0.3", {"start": v(257.7, -104.87) * mm, "end": v(257.7, -123.62) * mm});
            skLineSegment(sketch, "E33.20.0.4", {"start": v(255.2, -159.25) * mm, "end": v(255.2, -140.5) * mm});
            skLineSegment(sketch, "E33.20.0.5", {"start": v(258.1, -128.62) * mm, "end": v(258.1, -147.37) * mm});
            skLineSegment(sketch, "E33.20.0.6", {"start": v(257.7, -128.62) * mm, "end": v(257.7, -147.37) * mm});
            skLineSegment(sketch, "E33.20.0.7", {"start": v(254.8, -164.25) * mm, "end": v(254.8, -183) * mm});
            skLineSegment(sketch, "E33.20.0.8", {"start": v(255.2, -164.25) * mm, "end": v(255.2, -183) * mm});
            skLineSegment(sketch, "E33.20.0.9", {"start": v(257.7, -176.12) * mm, "end": v(257.7, -183) * mm});
            skLineSegment(sketch, "E33.20.0.10", {"start": v(258.1, -176.12) * mm, "end": v(258.1, -183) * mm});
            skLineSegment(sketch, "E33.20.0.11", {"start": v(258.1, -183) * mm, "end": v(258.1, -93) * mm, "construction": true});
            skLineSegment(sketch, "E33.20.0.12", {"start": v(257.7, -152.37) * mm, "end": v(257.7, -171.12) * mm});
            skLineSegment(sketch, "E33.20.0.13", {"start": v(254.8, -140.5) * mm, "end": v(254.8, -159.25) * mm});
            skLineSegment(sketch, "E33.20.0.14", {"start": v(254.8, -116.75) * mm, "end": v(254.8, -135.5) * mm});
            skLineSegment(sketch, "E33.20.0.15", {"start": v(255.2, -116.75) * mm, "end": v(255.2, -135.5) * mm});
            skLineSegment(sketch, "E33.20.0.16", {"start": v(258.1, -104.87) * mm, "end": v(258.1, -123.62) * mm});
            skLineSegment(sketch, "E33.20.0.17", {"start": v(254.8, -93) * mm, "end": v(254.8, -111.75) * mm});
            skLineSegment(sketch, "E33.20.0.18", {"start": v(255.2, -93) * mm, "end": v(255.2, -111.75) * mm});
            skLineSegment(sketch, "E33.20.0.19", {"start": v(258.1, -99.87) * mm, "end": v(258.1, -93) * mm});
            skLineSegment(sketch, "E33.20.0.20", {"start": v(254.8, -159.25) * mm, "end": v(254.8, -140.5) * mm});
            skLineSegment(sketch, "E33.20.0.21", {"start": v(254.8, -116.75) * mm, "end": v(254.8, -135.5) * mm});
            skLineSegment(sketch, "E33.20.0.22", {"start": v(255.2, -111.75) * mm, "end": v(255.2, -93) * mm});
            skLineSegment(sketch, "E33.20.0.23", {"start": v(254.8, -164.25) * mm, "end": v(254.8, -183) * mm});
            skLineSegment(sketch, "E33.20.0.24", {"start": v(254.8, -111.75) * mm, "end": v(254.8, -93) * mm});
            skLineSegment(sketch, "E33.20.0.25", {"start": v(257.7, -176.12) * mm, "end": v(258.1, -176.12) * mm});
            skLineSegment(sketch, "E33.20.0.26", {"start": v(257.7, -171.12) * mm, "end": v(258.1, -171.12) * mm});
            skLineSegment(sketch, "E33.20.0.27", {"start": v(257.7, -152.37) * mm, "end": v(258.1, -152.37) * mm});
            skLineSegment(sketch, "E33.20.0.28", {"start": v(257.7, -147.37) * mm, "end": v(258.1, -147.37) * mm});
            skLineSegment(sketch, "E33.20.0.29", {"start": v(257.7, -128.62) * mm, "end": v(258.1, -128.62) * mm});
            skLineSegment(sketch, "E33.20.0.30", {"start": v(257.7, -123.62) * mm, "end": v(258.1, -123.62) * mm});
            skLineSegment(sketch, "E33.20.0.31", {"start": v(257.7, -104.87) * mm, "end": v(258.1, -104.87) * mm});
            skLineSegment(sketch, "E33.20.0.32", {"start": v(257.7, -99.87) * mm, "end": v(258.1, -99.87) * mm});
            skLineSegment(sketch, "E33.20.0.33", {"start": v(254.8, -164.25) * mm, "end": v(255.2, -164.25) * mm});
            skLineSegment(sketch, "E33.20.0.34", {"start": v(254.8, -159.25) * mm, "end": v(255.2, -159.25) * mm});
            skLineSegment(sketch, "E33.20.0.35", {"start": v(258.1, -93) * mm, "end": v(254.8, -93) * mm, "construction": true});
            skLineSegment(sketch, "E33.20.0.36", {"start": v(254.8, -140.5) * mm, "end": v(255.2, -140.5) * mm});
            skLineSegment(sketch, "E33.20.0.37", {"start": v(254.8, -135.5) * mm, "end": v(255.2, -135.5) * mm});
            skLineSegment(sketch, "E33.20.0.38", {"start": v(254.8, -116.75) * mm, "end": v(255.2, -116.75) * mm});
            skLineSegment(sketch, "E33.20.0.39", {"start": v(257.7, -183) * mm, "end": v(258.1, -183) * mm});
            skLineSegment(sketch, "E33.20.0.40", {"start": v(257.7, -93) * mm, "end": v(258.1, -93) * mm});
            skLineSegment(sketch, "E33.20.0.41", {"start": v(258.1, -183) * mm, "end": v(254.8, -183) * mm, "construction": true});
            skLineSegment(sketch, "E33.20.0.42", {"start": v(255.2, -111.75) * mm, "end": v(254.8, -111.75) * mm});
            skLineSegment(sketch, "E33.20.0.43", {"start": v(254.8, -183) * mm, "end": v(255.2, -183) * mm});
            skLineSegment(sketch, "E33.20.0.44", {"start": v(254.8, -111.75) * mm, "end": v(255.2, -111.75) * mm});
            skLineSegment(sketch, "E33.20.0.45", {"start": v(255.2, -93) * mm, "end": v(254.8, -93) * mm});
            skLineSegment(sketch, "E33.21.0.0", {"start": v(263.55, -99.87) * mm, "end": v(263.55, -93) * mm});
            skLineSegment(sketch, "E33.21.0.1", {"start": v(260.65, -183) * mm, "end": v(260.65, -93) * mm, "construction": true});
            skLineSegment(sketch, "E33.21.0.2", {"start": v(263.95, -152.37) * mm, "end": v(263.95, -171.12) * mm});
            skLineSegment(sketch, "E33.21.0.3", {"start": v(263.55, -104.87) * mm, "end": v(263.55, -123.62) * mm});
            skLineSegment(sketch, "E33.21.0.4", {"start": v(261.05, -159.25) * mm, "end": v(261.05, -140.5) * mm});
            skLineSegment(sketch, "E33.21.0.5", {"start": v(263.95, -128.62) * mm, "end": v(263.95, -147.37) * mm});
            skLineSegment(sketch, "E33.21.0.6", {"start": v(263.55, -128.62) * mm, "end": v(263.55, -147.37) * mm});
            skLineSegment(sketch, "E33.21.0.7", {"start": v(260.65, -164.25) * mm, "end": v(260.65, -183) * mm});
            skLineSegment(sketch, "E33.21.0.8", {"start": v(261.05, -164.25) * mm, "end": v(261.05, -183) * mm});
            skLineSegment(sketch, "E33.21.0.9", {"start": v(263.55, -176.12) * mm, "end": v(263.55, -183) * mm});
            skLineSegment(sketch, "E33.21.0.10", {"start": v(263.95, -176.12) * mm, "end": v(263.95, -183) * mm});
            skLineSegment(sketch, "E33.21.0.11", {"start": v(263.95, -183) * mm, "end": v(263.95, -93) * mm, "construction": true});
            skLineSegment(sketch, "E33.21.0.12", {"start": v(263.55, -152.37) * mm, "end": v(263.55, -171.12) * mm});
            skLineSegment(sketch, "E33.21.0.13", {"start": v(260.65, -140.5) * mm, "end": v(260.65, -159.25) * mm});
            skLineSegment(sketch, "E33.21.0.14", {"start": v(260.65, -116.75) * mm, "end": v(260.65, -135.5) * mm});
            skLineSegment(sketch, "E33.21.0.15", {"start": v(261.05, -116.75) * mm, "end": v(261.05, -135.5) * mm});
            skLineSegment(sketch, "E33.21.0.16", {"start": v(263.95, -104.87) * mm, "end": v(263.95, -123.62) * mm});
            skLineSegment(sketch, "E33.21.0.17", {"start": v(260.65, -93) * mm, "end": v(260.65, -111.75) * mm});
            skLineSegment(sketch, "E33.21.0.18", {"start": v(261.05, -93) * mm, "end": v(261.05, -111.75) * mm});
            skLineSegment(sketch, "E33.21.0.19", {"start": v(263.95, -99.87) * mm, "end": v(263.95, -93) * mm});
            skLineSegment(sketch, "E33.21.0.20", {"start": v(260.65, -159.25) * mm, "end": v(260.65, -140.5) * mm});
            skLineSegment(sketch, "E33.21.0.21", {"start": v(260.65, -116.75) * mm, "end": v(260.65, -135.5) * mm});
            skLineSegment(sketch, "E33.21.0.22", {"start": v(261.05, -111.75) * mm, "end": v(261.05, -93) * mm});
            skLineSegment(sketch, "E33.21.0.23", {"start": v(260.65, -164.25) * mm, "end": v(260.65, -183) * mm});
            skLineSegment(sketch, "E33.21.0.24", {"start": v(260.65, -111.75) * mm, "end": v(260.65, -93) * mm});
            skLineSegment(sketch, "E33.21.0.25", {"start": v(263.55, -176.12) * mm, "end": v(263.95, -176.12) * mm});
            skLineSegment(sketch, "E33.21.0.26", {"start": v(263.55, -171.12) * mm, "end": v(263.95, -171.12) * mm});
            skLineSegment(sketch, "E33.21.0.27", {"start": v(263.55, -152.37) * mm, "end": v(263.95, -152.37) * mm});
            skLineSegment(sketch, "E33.21.0.28", {"start": v(263.55, -147.37) * mm, "end": v(263.95, -147.37) * mm});
            skLineSegment(sketch, "E33.21.0.29", {"start": v(263.55, -128.62) * mm, "end": v(263.95, -128.62) * mm});
            skLineSegment(sketch, "E33.21.0.30", {"start": v(263.55, -123.62) * mm, "end": v(263.95, -123.62) * mm});
            skLineSegment(sketch, "E33.21.0.31", {"start": v(263.55, -104.87) * mm, "end": v(263.95, -104.87) * mm});
            skLineSegment(sketch, "E33.21.0.32", {"start": v(263.55, -99.87) * mm, "end": v(263.95, -99.87) * mm});
            skLineSegment(sketch, "E33.21.0.33", {"start": v(260.65, -164.25) * mm, "end": v(261.05, -164.25) * mm});
            skLineSegment(sketch, "E33.21.0.34", {"start": v(260.65, -159.25) * mm, "end": v(261.05, -159.25) * mm});
            skLineSegment(sketch, "E33.21.0.35", {"start": v(263.95, -93) * mm, "end": v(260.65, -93) * mm, "construction": true});
            skLineSegment(sketch, "E33.21.0.36", {"start": v(260.65, -140.5) * mm, "end": v(261.05, -140.5) * mm});
            skLineSegment(sketch, "E33.21.0.37", {"start": v(260.65, -135.5) * mm, "end": v(261.05, -135.5) * mm});
            skLineSegment(sketch, "E33.21.0.38", {"start": v(260.65, -116.75) * mm, "end": v(261.05, -116.75) * mm});
            skLineSegment(sketch, "E33.21.0.39", {"start": v(263.55, -183) * mm, "end": v(263.95, -183) * mm});
            skLineSegment(sketch, "E33.21.0.40", {"start": v(263.55, -93) * mm, "end": v(263.95, -93) * mm});
            skLineSegment(sketch, "E33.21.0.41", {"start": v(263.95, -183) * mm, "end": v(260.65, -183) * mm, "construction": true});
            skLineSegment(sketch, "E33.21.0.42", {"start": v(261.05, -111.75) * mm, "end": v(260.65, -111.75) * mm});
            skLineSegment(sketch, "E33.21.0.43", {"start": v(260.65, -183) * mm, "end": v(261.05, -183) * mm});
            skLineSegment(sketch, "E33.21.0.44", {"start": v(260.65, -111.75) * mm, "end": v(261.05, -111.75) * mm});
            skLineSegment(sketch, "E33.21.0.45", {"start": v(261.05, -93) * mm, "end": v(260.65, -93) * mm});
            skLineSegment(sketch, "E33.22.0.0", {"start": v(269.4, -99.87) * mm, "end": v(269.4, -93) * mm});
            skLineSegment(sketch, "E33.22.0.1", {"start": v(266.5, -183) * mm, "end": v(266.5, -93) * mm, "construction": true});
            skLineSegment(sketch, "E33.22.0.2", {"start": v(269.8, -152.37) * mm, "end": v(269.8, -171.12) * mm});
            skLineSegment(sketch, "E33.22.0.3", {"start": v(269.4, -104.87) * mm, "end": v(269.4, -123.62) * mm});
            skLineSegment(sketch, "E33.22.0.4", {"start": v(266.9, -159.25) * mm, "end": v(266.9, -140.5) * mm});
            skLineSegment(sketch, "E33.22.0.5", {"start": v(269.8, -128.62) * mm, "end": v(269.8, -147.37) * mm});
            skLineSegment(sketch, "E33.22.0.6", {"start": v(269.4, -128.62) * mm, "end": v(269.4, -147.37) * mm});
            skLineSegment(sketch, "E33.22.0.7", {"start": v(266.5, -164.25) * mm, "end": v(266.5, -183) * mm});
            skLineSegment(sketch, "E33.22.0.8", {"start": v(266.9, -164.25) * mm, "end": v(266.9, -183) * mm});
            skLineSegment(sketch, "E33.22.0.9", {"start": v(269.4, -176.12) * mm, "end": v(269.4, -183) * mm});
            skLineSegment(sketch, "E33.22.0.10", {"start": v(269.8, -176.12) * mm, "end": v(269.8, -183) * mm});
            skLineSegment(sketch, "E33.22.0.11", {"start": v(269.8, -183) * mm, "end": v(269.8, -93) * mm, "construction": true});
            skLineSegment(sketch, "E33.22.0.12", {"start": v(269.4, -152.37) * mm, "end": v(269.4, -171.12) * mm});
            skLineSegment(sketch, "E33.22.0.13", {"start": v(266.5, -140.5) * mm, "end": v(266.5, -159.25) * mm});
            skLineSegment(sketch, "E33.22.0.14", {"start": v(266.5, -116.75) * mm, "end": v(266.5, -135.5) * mm});
            skLineSegment(sketch, "E33.22.0.15", {"start": v(266.9, -116.75) * mm, "end": v(266.9, -135.5) * mm});
            skLineSegment(sketch, "E33.22.0.16", {"start": v(269.8, -104.87) * mm, "end": v(269.8, -123.62) * mm});
            skLineSegment(sketch, "E33.22.0.17", {"start": v(266.5, -93) * mm, "end": v(266.5, -111.75) * mm});
            skLineSegment(sketch, "E33.22.0.18", {"start": v(266.9, -93) * mm, "end": v(266.9, -111.75) * mm});
            skLineSegment(sketch, "E33.22.0.19", {"start": v(269.8, -99.87) * mm, "end": v(269.8, -93) * mm});
            skLineSegment(sketch, "E33.22.0.20", {"start": v(266.5, -159.25) * mm, "end": v(266.5, -140.5) * mm});
            skLineSegment(sketch, "E33.22.0.21", {"start": v(266.5, -116.75) * mm, "end": v(266.5, -135.5) * mm});
            skLineSegment(sketch, "E33.22.0.22", {"start": v(266.9, -111.75) * mm, "end": v(266.9, -93) * mm});
            skLineSegment(sketch, "E33.22.0.23", {"start": v(266.5, -164.25) * mm, "end": v(266.5, -183) * mm});
            skLineSegment(sketch, "E33.22.0.24", {"start": v(266.5, -111.75) * mm, "end": v(266.5, -93) * mm});
            skLineSegment(sketch, "E33.22.0.25", {"start": v(269.4, -176.12) * mm, "end": v(269.8, -176.12) * mm});
            skLineSegment(sketch, "E33.22.0.26", {"start": v(269.4, -171.12) * mm, "end": v(269.8, -171.12) * mm});
            skLineSegment(sketch, "E33.22.0.27", {"start": v(269.4, -152.37) * mm, "end": v(269.8, -152.37) * mm});
            skLineSegment(sketch, "E33.22.0.28", {"start": v(269.4, -147.37) * mm, "end": v(269.8, -147.37) * mm});
            skLineSegment(sketch, "E33.22.0.29", {"start": v(269.4, -128.62) * mm, "end": v(269.8, -128.62) * mm});
            skLineSegment(sketch, "E33.22.0.30", {"start": v(269.4, -123.62) * mm, "end": v(269.8, -123.62) * mm});
            skLineSegment(sketch, "E33.22.0.31", {"start": v(269.4, -104.87) * mm, "end": v(269.8, -104.87) * mm});
            skLineSegment(sketch, "E33.22.0.32", {"start": v(269.4, -99.87) * mm, "end": v(269.8, -99.87) * mm});
            skLineSegment(sketch, "E33.22.0.33", {"start": v(266.5, -164.25) * mm, "end": v(266.9, -164.25) * mm});
            skLineSegment(sketch, "E33.22.0.34", {"start": v(266.5, -159.25) * mm, "end": v(266.9, -159.25) * mm});
            skLineSegment(sketch, "E33.22.0.35", {"start": v(269.8, -93) * mm, "end": v(266.5, -93) * mm, "construction": true});
            skLineSegment(sketch, "E33.22.0.36", {"start": v(266.5, -140.5) * mm, "end": v(266.9, -140.5) * mm});
            skLineSegment(sketch, "E33.22.0.37", {"start": v(266.5, -135.5) * mm, "end": v(266.9, -135.5) * mm});
            skLineSegment(sketch, "E33.22.0.38", {"start": v(266.5, -116.75) * mm, "end": v(266.9, -116.75) * mm});
            skLineSegment(sketch, "E33.22.0.39", {"start": v(269.4, -183) * mm, "end": v(269.8, -183) * mm});
            skLineSegment(sketch, "E33.22.0.40", {"start": v(269.4, -93) * mm, "end": v(269.8, -93) * mm});
            skLineSegment(sketch, "E33.22.0.41", {"start": v(269.8, -183) * mm, "end": v(266.5, -183) * mm, "construction": true});
            skLineSegment(sketch, "E33.22.0.42", {"start": v(266.9, -111.75) * mm, "end": v(266.5, -111.75) * mm});
            skLineSegment(sketch, "E33.22.0.43", {"start": v(266.5, -183) * mm, "end": v(266.9, -183) * mm});
            skLineSegment(sketch, "E33.22.0.44", {"start": v(266.5, -111.75) * mm, "end": v(266.9, -111.75) * mm});
            skLineSegment(sketch, "E33.22.0.45", {"start": v(266.9, -93) * mm, "end": v(266.5, -93) * mm});
            skLineSegment(sketch, "E33.23.0.0", {"start": v(275.25, -99.87) * mm, "end": v(275.25, -93) * mm});
            skLineSegment(sketch, "E33.23.0.1", {"start": v(272.35, -183) * mm, "end": v(272.35, -93) * mm, "construction": true});
            skLineSegment(sketch, "E33.23.0.2", {"start": v(275.65, -152.37) * mm, "end": v(275.65, -171.12) * mm});
            skLineSegment(sketch, "E33.23.0.3", {"start": v(275.25, -104.87) * mm, "end": v(275.25, -123.62) * mm});
            skLineSegment(sketch, "E33.23.0.4", {"start": v(272.75, -159.25) * mm, "end": v(272.75, -140.5) * mm});
            skLineSegment(sketch, "E33.23.0.5", {"start": v(275.65, -128.62) * mm, "end": v(275.65, -147.37) * mm});
            skLineSegment(sketch, "E33.23.0.6", {"start": v(275.25, -128.62) * mm, "end": v(275.25, -147.37) * mm});
            skLineSegment(sketch, "E33.23.0.7", {"start": v(272.35, -164.25) * mm, "end": v(272.35, -183) * mm});
            skLineSegment(sketch, "E33.23.0.8", {"start": v(272.75, -164.25) * mm, "end": v(272.75, -183) * mm});
            skLineSegment(sketch, "E33.23.0.9", {"start": v(275.25, -176.12) * mm, "end": v(275.25, -183) * mm});
            skLineSegment(sketch, "E33.23.0.10", {"start": v(275.65, -176.12) * mm, "end": v(275.65, -183) * mm});
            skLineSegment(sketch, "E33.23.0.11", {"start": v(275.65, -183) * mm, "end": v(275.65, -93) * mm, "construction": true});
            skLineSegment(sketch, "E33.23.0.12", {"start": v(275.25, -152.37) * mm, "end": v(275.25, -171.12) * mm});
            skLineSegment(sketch, "E33.23.0.13", {"start": v(272.35, -140.5) * mm, "end": v(272.35, -159.25) * mm});
            skLineSegment(sketch, "E33.23.0.14", {"start": v(272.35, -116.75) * mm, "end": v(272.35, -135.5) * mm});
            skLineSegment(sketch, "E33.23.0.15", {"start": v(272.75, -116.75) * mm, "end": v(272.75, -135.5) * mm});
            skLineSegment(sketch, "E33.23.0.16", {"start": v(275.65, -104.87) * mm, "end": v(275.65, -123.62) * mm});
            skLineSegment(sketch, "E33.23.0.17", {"start": v(272.35, -93) * mm, "end": v(272.35, -111.75) * mm});
            skLineSegment(sketch, "E33.23.0.18", {"start": v(272.75, -93) * mm, "end": v(272.75, -111.75) * mm});
            skLineSegment(sketch, "E33.23.0.19", {"start": v(275.65, -99.87) * mm, "end": v(275.65, -93) * mm});
            skLineSegment(sketch, "E33.23.0.20", {"start": v(272.35, -159.25) * mm, "end": v(272.35, -140.5) * mm});
            skLineSegment(sketch, "E33.23.0.21", {"start": v(272.35, -116.75) * mm, "end": v(272.35, -135.5) * mm});
            skLineSegment(sketch, "E33.23.0.22", {"start": v(272.75, -111.75) * mm, "end": v(272.75, -93) * mm});
            skLineSegment(sketch, "E33.23.0.23", {"start": v(272.35, -164.25) * mm, "end": v(272.35, -183) * mm});
            skLineSegment(sketch, "E33.23.0.24", {"start": v(272.35, -111.75) * mm, "end": v(272.35, -93) * mm});
            skLineSegment(sketch, "E33.23.0.25", {"start": v(275.25, -176.12) * mm, "end": v(275.65, -176.12) * mm});
            skLineSegment(sketch, "E33.23.0.26", {"start": v(275.25, -171.12) * mm, "end": v(275.65, -171.12) * mm});
            skLineSegment(sketch, "E33.23.0.27", {"start": v(275.25, -152.37) * mm, "end": v(275.65, -152.37) * mm});
            skLineSegment(sketch, "E33.23.0.28", {"start": v(275.25, -147.37) * mm, "end": v(275.65, -147.37) * mm});
            skLineSegment(sketch, "E33.23.0.29", {"start": v(275.25, -128.62) * mm, "end": v(275.65, -128.62) * mm});
            skLineSegment(sketch, "E33.23.0.30", {"start": v(275.25, -123.62) * mm, "end": v(275.65, -123.62) * mm});
            skLineSegment(sketch, "E33.23.0.31", {"start": v(275.25, -104.87) * mm, "end": v(275.65, -104.87) * mm});
            skLineSegment(sketch, "E33.23.0.32", {"start": v(275.25, -99.87) * mm, "end": v(275.65, -99.87) * mm});
            skLineSegment(sketch, "E33.23.0.33", {"start": v(272.35, -164.25) * mm, "end": v(272.75, -164.25) * mm});
            skLineSegment(sketch, "E33.23.0.34", {"start": v(272.35, -159.25) * mm, "end": v(272.75, -159.25) * mm});
            skLineSegment(sketch, "E33.23.0.35", {"start": v(275.65, -93) * mm, "end": v(272.35, -93) * mm, "construction": true});
            skLineSegment(sketch, "E33.23.0.36", {"start": v(272.35, -140.5) * mm, "end": v(272.75, -140.5) * mm});
            skLineSegment(sketch, "E33.23.0.37", {"start": v(272.35, -135.5) * mm, "end": v(272.75, -135.5) * mm});
            skLineSegment(sketch, "E33.23.0.38", {"start": v(272.35, -116.75) * mm, "end": v(272.75, -116.75) * mm});
            skLineSegment(sketch, "E33.23.0.39", {"start": v(275.25, -183) * mm, "end": v(275.65, -183) * mm});
            skLineSegment(sketch, "E33.23.0.40", {"start": v(275.25, -93) * mm, "end": v(275.65, -93) * mm});
            skLineSegment(sketch, "E33.23.0.41", {"start": v(275.65, -183) * mm, "end": v(272.35, -183) * mm, "construction": true});
            skLineSegment(sketch, "E33.23.0.42", {"start": v(272.75, -111.75) * mm, "end": v(272.35, -111.75) * mm});
            skLineSegment(sketch, "E33.23.0.43", {"start": v(272.35, -183) * mm, "end": v(272.75, -183) * mm});
            skLineSegment(sketch, "E33.23.0.44", {"start": v(272.35, -111.75) * mm, "end": v(272.75, -111.75) * mm});
            skLineSegment(sketch, "E33.23.0.45", {"start": v(272.75, -93) * mm, "end": v(272.35, -93) * mm});
            skLineSegment(sketch, "E33.24.0.0", {"start": v(281.1, -99.87) * mm, "end": v(281.1, -93) * mm});
            skLineSegment(sketch, "E33.24.0.1", {"start": v(278.2, -183) * mm, "end": v(278.2, -93) * mm, "construction": true});
            skLineSegment(sketch, "E33.24.0.2", {"start": v(281.5, -152.37) * mm, "end": v(281.5, -171.12) * mm});
            skLineSegment(sketch, "E33.24.0.3", {"start": v(281.1, -104.87) * mm, "end": v(281.1, -123.62) * mm});
            skLineSegment(sketch, "E33.24.0.4", {"start": v(278.6, -159.25) * mm, "end": v(278.6, -140.5) * mm});
            skLineSegment(sketch, "E33.24.0.5", {"start": v(281.5, -128.62) * mm, "end": v(281.5, -147.37) * mm});
            skLineSegment(sketch, "E33.24.0.6", {"start": v(281.1, -128.62) * mm, "end": v(281.1, -147.37) * mm});
            skLineSegment(sketch, "E33.24.0.7", {"start": v(278.2, -164.25) * mm, "end": v(278.2, -183) * mm});
            skLineSegment(sketch, "E33.24.0.8", {"start": v(278.6, -164.25) * mm, "end": v(278.6, -183) * mm});
            skLineSegment(sketch, "E33.24.0.9", {"start": v(281.1, -176.12) * mm, "end": v(281.1, -183) * mm});
            skLineSegment(sketch, "E33.24.0.10", {"start": v(281.5, -176.12) * mm, "end": v(281.5, -183) * mm});
            skLineSegment(sketch, "E33.24.0.11", {"start": v(281.5, -183) * mm, "end": v(281.5, -93) * mm, "construction": true});
            skLineSegment(sketch, "E33.24.0.12", {"start": v(281.1, -152.37) * mm, "end": v(281.1, -171.12) * mm});
            skLineSegment(sketch, "E33.24.0.13", {"start": v(278.2, -140.5) * mm, "end": v(278.2, -159.25) * mm});
            skLineSegment(sketch, "E33.24.0.14", {"start": v(278.2, -116.75) * mm, "end": v(278.2, -135.5) * mm});
            skLineSegment(sketch, "E33.24.0.15", {"start": v(278.6, -116.75) * mm, "end": v(278.6, -135.5) * mm});
            skLineSegment(sketch, "E33.24.0.16", {"start": v(281.5, -104.87) * mm, "end": v(281.5, -123.62) * mm});
            skLineSegment(sketch, "E33.24.0.17", {"start": v(278.2, -93) * mm, "end": v(278.2, -111.75) * mm});
            skLineSegment(sketch, "E33.24.0.18", {"start": v(278.6, -93) * mm, "end": v(278.6, -111.75) * mm});
            skLineSegment(sketch, "E33.24.0.19", {"start": v(281.5, -99.87) * mm, "end": v(281.5, -93) * mm});
            skLineSegment(sketch, "E33.24.0.20", {"start": v(278.2, -159.25) * mm, "end": v(278.2, -140.5) * mm});
            skLineSegment(sketch, "E33.24.0.21", {"start": v(278.2, -116.75) * mm, "end": v(278.2, -135.5) * mm});
            skLineSegment(sketch, "E33.24.0.22", {"start": v(278.6, -111.75) * mm, "end": v(278.6, -93) * mm});
            skLineSegment(sketch, "E33.24.0.23", {"start": v(278.2, -164.25) * mm, "end": v(278.2, -183) * mm});
            skLineSegment(sketch, "E33.24.0.24", {"start": v(278.2, -111.75) * mm, "end": v(278.2, -93) * mm});
            skLineSegment(sketch, "E33.24.0.25", {"start": v(281.1, -176.12) * mm, "end": v(281.5, -176.12) * mm});
            skLineSegment(sketch, "E33.24.0.26", {"start": v(281.1, -171.12) * mm, "end": v(281.5, -171.12) * mm});
            skLineSegment(sketch, "E33.24.0.27", {"start": v(281.1, -152.37) * mm, "end": v(281.5, -152.37) * mm});
            skLineSegment(sketch, "E33.24.0.28", {"start": v(281.1, -147.37) * mm, "end": v(281.5, -147.37) * mm});
            skLineSegment(sketch, "E33.24.0.29", {"start": v(281.1, -128.62) * mm, "end": v(281.5, -128.62) * mm});
            skLineSegment(sketch, "E33.24.0.30", {"start": v(281.1, -123.62) * mm, "end": v(281.5, -123.62) * mm});
            skLineSegment(sketch, "E33.24.0.31", {"start": v(281.1, -104.87) * mm, "end": v(281.5, -104.87) * mm});
            skLineSegment(sketch, "E33.24.0.32", {"start": v(281.1, -99.87) * mm, "end": v(281.5, -99.87) * mm});
            skLineSegment(sketch, "E33.24.0.33", {"start": v(278.2, -164.25) * mm, "end": v(278.6, -164.25) * mm});
            skLineSegment(sketch, "E33.24.0.34", {"start": v(278.2, -159.25) * mm, "end": v(278.6, -159.25) * mm});
            skLineSegment(sketch, "E33.24.0.35", {"start": v(281.5, -93) * mm, "end": v(278.2, -93) * mm, "construction": true});
            skLineSegment(sketch, "E33.24.0.36", {"start": v(278.2, -140.5) * mm, "end": v(278.6, -140.5) * mm});
            skLineSegment(sketch, "E33.24.0.37", {"start": v(278.2, -135.5) * mm, "end": v(278.6, -135.5) * mm});
            skLineSegment(sketch, "E33.24.0.38", {"start": v(278.2, -116.75) * mm, "end": v(278.6, -116.75) * mm});
            skLineSegment(sketch, "E33.24.0.39", {"start": v(281.1, -183) * mm, "end": v(281.5, -183) * mm});
            skLineSegment(sketch, "E33.24.0.40", {"start": v(281.1, -93) * mm, "end": v(281.5, -93) * mm});
            skLineSegment(sketch, "E33.24.0.41", {"start": v(281.5, -183) * mm, "end": v(278.2, -183) * mm, "construction": true});
            skLineSegment(sketch, "E33.24.0.42", {"start": v(278.6, -111.75) * mm, "end": v(278.2, -111.75) * mm});
            skLineSegment(sketch, "E33.24.0.43", {"start": v(278.2, -183) * mm, "end": v(278.6, -183) * mm});
            skLineSegment(sketch, "E33.24.0.44", {"start": v(278.2, -111.75) * mm, "end": v(278.6, -111.75) * mm});
            skLineSegment(sketch, "E33.24.0.45", {"start": v(278.6, -93) * mm, "end": v(278.2, -93) * mm});
            skSolve(sketch);
        }
        {
            var Q0;
            Q0 = qSketchRegion(id + "F2", true);
            extrude(context, id + "F3", {"entities" : qUnion([Q0]), "operationType" : NewBodyOperationType.REMOVE, "oppositeDirection" : true, "depth" : 25 * mm});
        }
        {
            var Q0;
            Q0=makeQuery(id+"F2.imprint","IMPRINT",FACE,{"disambiguationData":[TD([[makeQuery(id+"F2.imprint","IMPRINT",EDGE,{"derivedFrom":makeQuery(id+"F1.opExtrude","CAP_EDGE",EDGE,{"disambiguationData":[OSD([sQuery(id+"F0.wireOp",EDGE,"E1.bottom")])],"isStart":false})}),-1.0]])]});
            var sketch = newSketch(context, id + "F4", { "sketchPlane" : qUnion([Q0])});
            skLineSegment(sketch, "E34.left", {"start": v(2.5, -164.25) * mm, "end": v(2.5, -183) * mm});
            skLineSegment(sketch, "E35.left", {"start": v(5.4, -176.12) * mm, "end": v(5.4, -183) * mm});
            skLineSegment(sketch, "E35.right", {"start": v(5.8, -176.12) * mm, "end": v(5.8, -183) * mm});
            skLineSegment(sketch, "E36.left", {"start": v(5.8, -183) * mm, "end": v(5.8, -93) * mm, "construction": true});
            skLineSegment(sketch, "E37.left", {"start": v(5.4, -152.37) * mm, "end": v(5.4, -171.12) * mm});
            skLineSegment(sketch, "E37.right", {"start": v(5.8, -152.37) * mm, "end": v(5.8, -171.12) * mm});
            skLineSegment(sketch, "E36.right", {"start": v(2.5, -183) * mm, "end": v(2.5, -93) * mm, "construction": true});
            skLineSegment(sketch, "E38.left", {"start": v(2.5, -140.5) * mm, "end": v(2.5, -159.25) * mm});
            skLineSegment(sketch, "E39.left", {"start": v(5.4, -128.62) * mm, "end": v(5.4, -147.37) * mm});
            skLineSegment(sketch, "E39.right", {"start": v(5.8, -128.62) * mm, "end": v(5.8, -147.37) * mm});
            skLineSegment(sketch, "E40.left", {"start": v(2.5, -116.75) * mm, "end": v(2.5, -135.5) * mm});
            skLineSegment(sketch, "E41.left", {"start": v(5.4, -104.87) * mm, "end": v(5.4, -123.62) * mm});
            skLineSegment(sketch, "E41.right", {"start": v(5.8, -104.87) * mm, "end": v(5.8, -123.62) * mm});
            skLineSegment(sketch, "E42.left", {"start": v(2.5, -93) * mm, "end": v(2.5, -111.75) * mm});
            skLineSegment(sketch, "E43.left", {"start": v(5.4, -99.87) * mm, "end": v(5.4, -93) * mm});
            skLineSegment(sketch, "E43.right", {"start": v(5.8, -99.87) * mm, "end": v(5.8, -93) * mm});
            skLineSegment(sketch, "E44.right", {"start": v(2.9, -164.25) * mm, "end": v(2.9, -183) * mm});
            skLineSegment(sketch, "E45.right", {"start": v(2.9, -159.25) * mm, "end": v(2.9, -140.5) * mm});
            skLineSegment(sketch, "E46.right", {"start": v(2.9, -116.75) * mm, "end": v(2.9, -135.5) * mm});
            skLineSegment(sketch, "E42.right", {"start": v(2.9, -93) * mm, "end": v(2.9, -111.75) * mm});
            skLineSegment(sketch, "E35.bottom", {"start": v(5.4, -176.12) * mm, "end": v(5.8, -176.12) * mm});
            skLineSegment(sketch, "E37.top", {"start": v(5.4, -171.12) * mm, "end": v(5.8, -171.12) * mm});
            skLineSegment(sketch, "E37.bottom", {"start": v(5.4, -152.37) * mm, "end": v(5.8, -152.37) * mm});
            skLineSegment(sketch, "E39.top", {"start": v(5.4, -147.37) * mm, "end": v(5.8, -147.37) * mm});
            skLineSegment(sketch, "E39.bottom", {"start": v(5.4, -128.62) * mm, "end": v(5.8, -128.62) * mm});
            skLineSegment(sketch, "E41.top", {"start": v(5.4, -123.62) * mm, "end": v(5.8, -123.62) * mm});
            skLineSegment(sketch, "E41.bottom", {"start": v(5.4, -104.87) * mm, "end": v(5.8, -104.87) * mm});
            skLineSegment(sketch, "E43.bottom", {"start": v(5.4, -99.87) * mm, "end": v(5.8, -99.87) * mm});
            skLineSegment(sketch, "E36.bottom", {"start": v(5.8, -183) * mm, "end": v(2.5, -183) * mm, "construction": true});
            skLineSegment(sketch, "E35.top", {"start": v(5.4, -183) * mm, "end": v(5.8, -183) * mm});
            skLineSegment(sketch, "E36.top", {"start": v(5.8, -93) * mm, "end": v(2.5, -93) * mm, "construction": true});
            skLineSegment(sketch, "E43.top", {"start": v(5.4, -93) * mm, "end": v(5.8, -93) * mm});
            skLineSegment(sketch, "E47", {"start": v(2.5, -111.75) * mm, "end": v(2.9, -111.75) * mm});
            skLineSegment(sketch, "E48", {"start": v(2.5, -116.75) * mm, "end": v(2.9, -116.75) * mm});
            skLineSegment(sketch, "E49", {"start": v(2.5, -135.5) * mm, "end": v(2.9, -135.5) * mm});
            skLineSegment(sketch, "E50", {"start": v(2.5, -140.5) * mm, "end": v(2.9, -140.5) * mm});
            skLineSegment(sketch, "E51", {"start": v(2.5, -164.25) * mm, "end": v(2.9, -164.25) * mm});
            skLineSegment(sketch, "E52", {"start": v(2.5, -159.25) * mm, "end": v(2.9, -159.25) * mm});
            skLineSegment(sketch, "E53", {"start": v(2.5, -183) * mm, "end": v(2.9, -183) * mm});
            skLineSegment(sketch, "E54", {"start": v(2.5, -93) * mm, "end": v(2.9, -93) * mm});
            skLineSegment(sketch, "E55.1.0.0", {"start": v(8.27, -164.25) * mm, "end": v(8.27, -183) * mm});
            skLineSegment(sketch, "E55.1.0.1", {"start": v(8.67, -164.25) * mm, "end": v(8.67, -183) * mm});
            skLineSegment(sketch, "E55.1.0.2", {"start": v(11.17, -176.12) * mm, "end": v(11.17, -183) * mm});
            skLineSegment(sketch, "E55.1.0.3", {"start": v(11.57, -176.12) * mm, "end": v(11.57, -183) * mm});
            skLineSegment(sketch, "E55.1.0.4", {"start": v(11.57, -183) * mm, "end": v(11.57, -93) * mm, "construction": true});
            skLineSegment(sketch, "E55.1.0.5", {"start": v(11.17, -152.37) * mm, "end": v(11.17, -171.12) * mm});
            skLineSegment(sketch, "E55.1.0.6", {"start": v(11.57, -152.37) * mm, "end": v(11.57, -171.12) * mm});
            skLineSegment(sketch, "E55.1.0.7", {"start": v(8.27, -140.5) * mm, "end": v(8.27, -159.25) * mm});
            skLineSegment(sketch, "E55.1.0.8", {"start": v(8.67, -159.25) * mm, "end": v(8.67, -140.5) * mm});
            skLineSegment(sketch, "E55.1.0.9", {"start": v(11.17, -128.62) * mm, "end": v(11.17, -147.37) * mm});
            skLineSegment(sketch, "E55.1.0.10", {"start": v(11.57, -128.62) * mm, "end": v(11.57, -147.37) * mm});
            skLineSegment(sketch, "E55.1.0.11", {"start": v(8.27, -183) * mm, "end": v(8.27, -93) * mm, "construction": true});
            skLineSegment(sketch, "E55.1.0.12", {"start": v(8.27, -116.75) * mm, "end": v(8.27, -135.5) * mm});
            skLineSegment(sketch, "E55.1.0.13", {"start": v(8.67, -116.75) * mm, "end": v(8.67, -135.5) * mm});
            skLineSegment(sketch, "E55.1.0.14", {"start": v(11.17, -104.87) * mm, "end": v(11.17, -123.62) * mm});
            skLineSegment(sketch, "E55.1.0.15", {"start": v(11.57, -104.87) * mm, "end": v(11.57, -123.62) * mm});
            skLineSegment(sketch, "E55.1.0.16", {"start": v(8.27, -93) * mm, "end": v(8.27, -111.75) * mm});
            skLineSegment(sketch, "E55.1.0.17", {"start": v(8.67, -93) * mm, "end": v(8.67, -111.75) * mm});
            skLineSegment(sketch, "E55.1.0.18", {"start": v(11.17, -99.87) * mm, "end": v(11.17, -93) * mm});
            skLineSegment(sketch, "E55.1.0.19", {"start": v(11.57, -99.87) * mm, "end": v(11.57, -93) * mm});
            skLineSegment(sketch, "E55.1.0.20", {"start": v(11.17, -176.12) * mm, "end": v(11.57, -176.12) * mm});
            skLineSegment(sketch, "E55.1.0.21", {"start": v(11.17, -171.12) * mm, "end": v(11.57, -171.12) * mm});
            skLineSegment(sketch, "E55.1.0.22", {"start": v(8.27, -164.25) * mm, "end": v(8.67, -164.25) * mm});
            skLineSegment(sketch, "E55.1.0.23", {"start": v(8.27, -159.25) * mm, "end": v(8.67, -159.25) * mm});
            skLineSegment(sketch, "E55.1.0.24", {"start": v(11.17, -152.37) * mm, "end": v(11.57, -152.37) * mm});
            skLineSegment(sketch, "E55.1.0.25", {"start": v(11.17, -147.37) * mm, "end": v(11.57, -147.37) * mm});
            skLineSegment(sketch, "E55.1.0.26", {"start": v(8.27, -140.5) * mm, "end": v(8.67, -140.5) * mm});
            skLineSegment(sketch, "E55.1.0.27", {"start": v(8.27, -135.5) * mm, "end": v(8.67, -135.5) * mm});
            skLineSegment(sketch, "E55.1.0.28", {"start": v(11.17, -128.62) * mm, "end": v(11.57, -128.62) * mm});
            skLineSegment(sketch, "E55.1.0.29", {"start": v(11.17, -123.62) * mm, "end": v(11.57, -123.62) * mm});
            skLineSegment(sketch, "E55.1.0.30", {"start": v(8.27, -116.75) * mm, "end": v(8.67, -116.75) * mm});
            skLineSegment(sketch, "E55.1.0.31", {"start": v(8.27, -111.75) * mm, "end": v(8.67, -111.75) * mm});
            skLineSegment(sketch, "E55.1.0.32", {"start": v(11.17, -104.87) * mm, "end": v(11.57, -104.87) * mm});
            skLineSegment(sketch, "E55.1.0.33", {"start": v(11.17, -99.87) * mm, "end": v(11.57, -99.87) * mm});
            skLineSegment(sketch, "E55.1.0.34", {"start": v(11.17, -183) * mm, "end": v(11.57, -183) * mm});
            skLineSegment(sketch, "E55.1.0.35", {"start": v(8.27, -183) * mm, "end": v(8.67, -183) * mm});
            skLineSegment(sketch, "E55.1.0.36", {"start": v(11.57, -183) * mm, "end": v(8.27, -183) * mm, "construction": true});
            skLineSegment(sketch, "E55.1.0.37", {"start": v(8.27, -93) * mm, "end": v(8.67, -93) * mm});
            skLineSegment(sketch, "E55.1.0.38", {"start": v(11.57, -93) * mm, "end": v(8.27, -93) * mm, "construction": true});
            skLineSegment(sketch, "E55.1.0.39", {"start": v(11.17, -93) * mm, "end": v(11.57, -93) * mm});
            skLineSegment(sketch, "E55.2.0.0", {"start": v(14.04, -164.25) * mm, "end": v(14.04, -183) * mm});
            skLineSegment(sketch, "E55.2.0.1", {"start": v(14.44, -164.25) * mm, "end": v(14.44, -183) * mm});
            skLineSegment(sketch, "E55.2.0.2", {"start": v(16.94, -176.12) * mm, "end": v(16.94, -183) * mm});
            skLineSegment(sketch, "E55.2.0.3", {"start": v(17.34, -176.12) * mm, "end": v(17.34, -183) * mm});
            skLineSegment(sketch, "E55.2.0.4", {"start": v(17.34, -183) * mm, "end": v(17.34, -93) * mm, "construction": true});
            skLineSegment(sketch, "E55.2.0.5", {"start": v(16.94, -152.37) * mm, "end": v(16.94, -171.12) * mm});
            skLineSegment(sketch, "E55.2.0.6", {"start": v(17.34, -152.37) * mm, "end": v(17.34, -171.12) * mm});
            skLineSegment(sketch, "E55.2.0.7", {"start": v(14.04, -140.5) * mm, "end": v(14.04, -159.25) * mm});
            skLineSegment(sketch, "E55.2.0.8", {"start": v(14.44, -159.25) * mm, "end": v(14.44, -140.5) * mm});
            skLineSegment(sketch, "E55.2.0.9", {"start": v(16.94, -128.62) * mm, "end": v(16.94, -147.37) * mm});
            skLineSegment(sketch, "E55.2.0.10", {"start": v(17.34, -128.62) * mm, "end": v(17.34, -147.37) * mm});
            skLineSegment(sketch, "E55.2.0.11", {"start": v(14.04, -183) * mm, "end": v(14.04, -93) * mm, "construction": true});
            skLineSegment(sketch, "E55.2.0.12", {"start": v(14.04, -116.75) * mm, "end": v(14.04, -135.5) * mm});
            skLineSegment(sketch, "E55.2.0.13", {"start": v(14.44, -116.75) * mm, "end": v(14.44, -135.5) * mm});
            skLineSegment(sketch, "E55.2.0.14", {"start": v(16.94, -104.87) * mm, "end": v(16.94, -123.62) * mm});
            skLineSegment(sketch, "E55.2.0.15", {"start": v(17.34, -104.87) * mm, "end": v(17.34, -123.62) * mm});
            skLineSegment(sketch, "E55.2.0.16", {"start": v(14.04, -93) * mm, "end": v(14.04, -111.75) * mm});
            skLineSegment(sketch, "E55.2.0.17", {"start": v(14.44, -93) * mm, "end": v(14.44, -111.75) * mm});
            skLineSegment(sketch, "E55.2.0.18", {"start": v(16.94, -99.87) * mm, "end": v(16.94, -93) * mm});
            skLineSegment(sketch, "E55.2.0.19", {"start": v(17.34, -99.87) * mm, "end": v(17.34, -93) * mm});
            skLineSegment(sketch, "E55.2.0.20", {"start": v(16.94, -176.12) * mm, "end": v(17.34, -176.12) * mm});
            skLineSegment(sketch, "E55.2.0.21", {"start": v(16.94, -171.12) * mm, "end": v(17.34, -171.12) * mm});
            skLineSegment(sketch, "E55.2.0.22", {"start": v(14.04, -164.25) * mm, "end": v(14.44, -164.25) * mm});
            skLineSegment(sketch, "E55.2.0.23", {"start": v(14.04, -159.25) * mm, "end": v(14.44, -159.25) * mm});
            skLineSegment(sketch, "E55.2.0.24", {"start": v(16.94, -152.37) * mm, "end": v(17.34, -152.37) * mm});
            skLineSegment(sketch, "E55.2.0.25", {"start": v(16.94, -147.37) * mm, "end": v(17.34, -147.37) * mm});
            skLineSegment(sketch, "E55.2.0.26", {"start": v(14.04, -140.5) * mm, "end": v(14.44, -140.5) * mm});
            skLineSegment(sketch, "E55.2.0.27", {"start": v(14.04, -135.5) * mm, "end": v(14.44, -135.5) * mm});
            skLineSegment(sketch, "E55.2.0.28", {"start": v(16.94, -128.62) * mm, "end": v(17.34, -128.62) * mm});
            skLineSegment(sketch, "E55.2.0.29", {"start": v(16.94, -123.62) * mm, "end": v(17.34, -123.62) * mm});
            skLineSegment(sketch, "E55.2.0.30", {"start": v(14.04, -116.75) * mm, "end": v(14.44, -116.75) * mm});
            skLineSegment(sketch, "E55.2.0.31", {"start": v(14.04, -111.75) * mm, "end": v(14.44, -111.75) * mm});
            skLineSegment(sketch, "E55.2.0.32", {"start": v(16.94, -104.87) * mm, "end": v(17.34, -104.87) * mm});
            skLineSegment(sketch, "E55.2.0.33", {"start": v(16.94, -99.87) * mm, "end": v(17.34, -99.87) * mm});
            skLineSegment(sketch, "E55.2.0.34", {"start": v(16.94, -183) * mm, "end": v(17.34, -183) * mm});
            skLineSegment(sketch, "E55.2.0.35", {"start": v(14.04, -183) * mm, "end": v(14.44, -183) * mm});
            skLineSegment(sketch, "E55.2.0.36", {"start": v(17.34, -183) * mm, "end": v(14.04, -183) * mm, "construction": true});
            skLineSegment(sketch, "E55.2.0.37", {"start": v(14.04, -93) * mm, "end": v(14.44, -93) * mm});
            skLineSegment(sketch, "E55.2.0.38", {"start": v(17.34, -93) * mm, "end": v(14.04, -93) * mm, "construction": true});
            skLineSegment(sketch, "E55.2.0.39", {"start": v(16.94, -93) * mm, "end": v(17.34, -93) * mm});
            skLineSegment(sketch, "E55.3.0.0", {"start": v(19.81, -164.25) * mm, "end": v(19.81, -183) * mm});
            skLineSegment(sketch, "E55.3.0.1", {"start": v(20.21, -164.25) * mm, "end": v(20.21, -183) * mm});
            skLineSegment(sketch, "E55.3.0.2", {"start": v(22.71, -176.12) * mm, "end": v(22.71, -183) * mm});
            skLineSegment(sketch, "E55.3.0.3", {"start": v(23.11, -176.12) * mm, "end": v(23.11, -183) * mm});
            skLineSegment(sketch, "E55.3.0.4", {"start": v(23.11, -183) * mm, "end": v(23.11, -93) * mm, "construction": true});
            skLineSegment(sketch, "E55.3.0.5", {"start": v(22.71, -152.37) * mm, "end": v(22.71, -171.12) * mm});
            skLineSegment(sketch, "E55.3.0.6", {"start": v(23.11, -152.37) * mm, "end": v(23.11, -171.12) * mm});
            skLineSegment(sketch, "E55.3.0.7", {"start": v(19.81, -140.5) * mm, "end": v(19.81, -159.25) * mm});
            skLineSegment(sketch, "E55.3.0.8", {"start": v(20.21, -159.25) * mm, "end": v(20.21, -140.5) * mm});
            skLineSegment(sketch, "E55.3.0.9", {"start": v(22.71, -128.62) * mm, "end": v(22.71, -147.37) * mm});
            skLineSegment(sketch, "E55.3.0.10", {"start": v(23.11, -128.62) * mm, "end": v(23.11, -147.37) * mm});
            skLineSegment(sketch, "E55.3.0.11", {"start": v(19.81, -183) * mm, "end": v(19.81, -93) * mm, "construction": true});
            skLineSegment(sketch, "E55.3.0.12", {"start": v(19.81, -116.75) * mm, "end": v(19.81, -135.5) * mm});
            skLineSegment(sketch, "E55.3.0.13", {"start": v(20.21, -116.75) * mm, "end": v(20.21, -135.5) * mm});
            skLineSegment(sketch, "E55.3.0.14", {"start": v(22.71, -104.87) * mm, "end": v(22.71, -123.62) * mm});
            skLineSegment(sketch, "E55.3.0.15", {"start": v(23.11, -104.87) * mm, "end": v(23.11, -123.62) * mm});
            skLineSegment(sketch, "E55.3.0.16", {"start": v(19.81, -93) * mm, "end": v(19.81, -111.75) * mm});
            skLineSegment(sketch, "E55.3.0.17", {"start": v(20.21, -93) * mm, "end": v(20.21, -111.75) * mm});
            skLineSegment(sketch, "E55.3.0.18", {"start": v(22.71, -99.87) * mm, "end": v(22.71, -93) * mm});
            skLineSegment(sketch, "E55.3.0.19", {"start": v(23.11, -99.87) * mm, "end": v(23.11, -93) * mm});
            skLineSegment(sketch, "E55.3.0.20", {"start": v(22.71, -176.12) * mm, "end": v(23.11, -176.12) * mm});
            skLineSegment(sketch, "E55.3.0.21", {"start": v(22.71, -171.12) * mm, "end": v(23.11, -171.12) * mm});
            skLineSegment(sketch, "E55.3.0.22", {"start": v(19.81, -164.25) * mm, "end": v(20.21, -164.25) * mm});
            skLineSegment(sketch, "E55.3.0.23", {"start": v(19.81, -159.25) * mm, "end": v(20.21, -159.25) * mm});
            skLineSegment(sketch, "E55.3.0.24", {"start": v(22.71, -152.37) * mm, "end": v(23.11, -152.37) * mm});
            skLineSegment(sketch, "E55.3.0.25", {"start": v(22.71, -147.37) * mm, "end": v(23.11, -147.37) * mm});
            skLineSegment(sketch, "E55.3.0.26", {"start": v(19.81, -140.5) * mm, "end": v(20.21, -140.5) * mm});
            skLineSegment(sketch, "E55.3.0.27", {"start": v(19.81, -135.5) * mm, "end": v(20.21, -135.5) * mm});
            skLineSegment(sketch, "E55.3.0.28", {"start": v(22.71, -128.62) * mm, "end": v(23.11, -128.62) * mm});
            skLineSegment(sketch, "E55.3.0.29", {"start": v(22.71, -123.62) * mm, "end": v(23.11, -123.62) * mm});
            skLineSegment(sketch, "E55.3.0.30", {"start": v(19.81, -116.75) * mm, "end": v(20.21, -116.75) * mm});
            skLineSegment(sketch, "E55.3.0.31", {"start": v(19.81, -111.75) * mm, "end": v(20.21, -111.75) * mm});
            skLineSegment(sketch, "E55.3.0.32", {"start": v(22.71, -104.87) * mm, "end": v(23.11, -104.87) * mm});
            skLineSegment(sketch, "E55.3.0.33", {"start": v(22.71, -99.87) * mm, "end": v(23.11, -99.87) * mm});
            skLineSegment(sketch, "E55.3.0.34", {"start": v(22.71, -183) * mm, "end": v(23.11, -183) * mm});
            skLineSegment(sketch, "E55.3.0.35", {"start": v(19.81, -183) * mm, "end": v(20.21, -183) * mm});
            skLineSegment(sketch, "E55.3.0.36", {"start": v(23.11, -183) * mm, "end": v(19.81, -183) * mm, "construction": true});
            skLineSegment(sketch, "E55.3.0.37", {"start": v(19.81, -93) * mm, "end": v(20.21, -93) * mm});
            skLineSegment(sketch, "E55.3.0.38", {"start": v(23.11, -93) * mm, "end": v(19.81, -93) * mm, "construction": true});
            skLineSegment(sketch, "E55.3.0.39", {"start": v(22.71, -93) * mm, "end": v(23.11, -93) * mm});
            skLineSegment(sketch, "E55.4.0.0", {"start": v(25.58, -164.25) * mm, "end": v(25.58, -183) * mm});
            skLineSegment(sketch, "E55.4.0.1", {"start": v(25.98, -164.25) * mm, "end": v(25.98, -183) * mm});
            skLineSegment(sketch, "E55.4.0.2", {"start": v(28.48, -176.12) * mm, "end": v(28.48, -183) * mm});
            skLineSegment(sketch, "E55.4.0.3", {"start": v(28.88, -176.12) * mm, "end": v(28.88, -183) * mm});
            skLineSegment(sketch, "E55.4.0.4", {"start": v(28.88, -183) * mm, "end": v(28.88, -93) * mm, "construction": true});
            skLineSegment(sketch, "E55.4.0.5", {"start": v(28.48, -152.37) * mm, "end": v(28.48, -171.12) * mm});
            skLineSegment(sketch, "E55.4.0.6", {"start": v(28.88, -152.37) * mm, "end": v(28.88, -171.12) * mm});
            skLineSegment(sketch, "E55.4.0.7", {"start": v(25.58, -140.5) * mm, "end": v(25.58, -159.25) * mm});
            skLineSegment(sketch, "E55.4.0.8", {"start": v(25.98, -159.25) * mm, "end": v(25.98, -140.5) * mm});
            skLineSegment(sketch, "E55.4.0.9", {"start": v(28.48, -128.62) * mm, "end": v(28.48, -147.37) * mm});
            skLineSegment(sketch, "E55.4.0.10", {"start": v(28.88, -128.62) * mm, "end": v(28.88, -147.37) * mm});
            skLineSegment(sketch, "E55.4.0.11", {"start": v(25.58, -183) * mm, "end": v(25.58, -93) * mm, "construction": true});
            skLineSegment(sketch, "E55.4.0.12", {"start": v(25.58, -116.75) * mm, "end": v(25.58, -135.5) * mm});
            skLineSegment(sketch, "E55.4.0.13", {"start": v(25.98, -116.75) * mm, "end": v(25.98, -135.5) * mm});
            skLineSegment(sketch, "E55.4.0.14", {"start": v(28.48, -104.87) * mm, "end": v(28.48, -123.62) * mm});
            skLineSegment(sketch, "E55.4.0.15", {"start": v(28.88, -104.87) * mm, "end": v(28.88, -123.62) * mm});
            skLineSegment(sketch, "E55.4.0.16", {"start": v(25.58, -93) * mm, "end": v(25.58, -111.75) * mm});
            skLineSegment(sketch, "E55.4.0.17", {"start": v(25.98, -93) * mm, "end": v(25.98, -111.75) * mm});
            skLineSegment(sketch, "E55.4.0.18", {"start": v(28.48, -99.87) * mm, "end": v(28.48, -93) * mm});
            skLineSegment(sketch, "E55.4.0.19", {"start": v(28.88, -99.87) * mm, "end": v(28.88, -93) * mm});
            skLineSegment(sketch, "E55.4.0.20", {"start": v(28.48, -176.12) * mm, "end": v(28.88, -176.12) * mm});
            skLineSegment(sketch, "E55.4.0.21", {"start": v(28.48, -171.12) * mm, "end": v(28.88, -171.12) * mm});
            skLineSegment(sketch, "E55.4.0.22", {"start": v(25.58, -164.25) * mm, "end": v(25.98, -164.25) * mm});
            skLineSegment(sketch, "E55.4.0.23", {"start": v(25.58, -159.25) * mm, "end": v(25.98, -159.25) * mm});
            skLineSegment(sketch, "E55.4.0.24", {"start": v(28.48, -152.37) * mm, "end": v(28.88, -152.37) * mm});
            skLineSegment(sketch, "E55.4.0.25", {"start": v(28.48, -147.37) * mm, "end": v(28.88, -147.37) * mm});
            skLineSegment(sketch, "E55.4.0.26", {"start": v(25.58, -140.5) * mm, "end": v(25.98, -140.5) * mm});
            skLineSegment(sketch, "E55.4.0.27", {"start": v(25.58, -135.5) * mm, "end": v(25.98, -135.5) * mm});
            skLineSegment(sketch, "E55.4.0.28", {"start": v(28.48, -128.62) * mm, "end": v(28.88, -128.62) * mm});
            skLineSegment(sketch, "E55.4.0.29", {"start": v(28.48, -123.62) * mm, "end": v(28.88, -123.62) * mm});
            skLineSegment(sketch, "E55.4.0.30", {"start": v(25.58, -116.75) * mm, "end": v(25.98, -116.75) * mm});
            skLineSegment(sketch, "E55.4.0.31", {"start": v(25.58, -111.75) * mm, "end": v(25.98, -111.75) * mm});
            skLineSegment(sketch, "E55.4.0.32", {"start": v(28.48, -104.87) * mm, "end": v(28.88, -104.87) * mm});
            skLineSegment(sketch, "E55.4.0.33", {"start": v(28.48, -99.87) * mm, "end": v(28.88, -99.87) * mm});
            skLineSegment(sketch, "E55.4.0.34", {"start": v(28.48, -183) * mm, "end": v(28.88, -183) * mm});
            skLineSegment(sketch, "E55.4.0.35", {"start": v(25.58, -183) * mm, "end": v(25.98, -183) * mm});
            skLineSegment(sketch, "E55.4.0.36", {"start": v(28.88, -183) * mm, "end": v(25.58, -183) * mm, "construction": true});
            skLineSegment(sketch, "E55.4.0.37", {"start": v(25.58, -93) * mm, "end": v(25.98, -93) * mm});
            skLineSegment(sketch, "E55.4.0.38", {"start": v(28.88, -93) * mm, "end": v(25.58, -93) * mm, "construction": true});
            skLineSegment(sketch, "E55.4.0.39", {"start": v(28.48, -93) * mm, "end": v(28.88, -93) * mm});
            skLineSegment(sketch, "E55.5.0.0", {"start": v(31.35, -164.25) * mm, "end": v(31.35, -183) * mm});
            skLineSegment(sketch, "E55.5.0.1", {"start": v(31.75, -164.25) * mm, "end": v(31.75, -183) * mm});
            skLineSegment(sketch, "E55.5.0.2", {"start": v(34.25, -176.12) * mm, "end": v(34.25, -183) * mm});
            skLineSegment(sketch, "E55.5.0.3", {"start": v(34.65, -176.12) * mm, "end": v(34.65, -183) * mm});
            skLineSegment(sketch, "E55.5.0.4", {"start": v(34.65, -183) * mm, "end": v(34.65, -93) * mm, "construction": true});
            skLineSegment(sketch, "E55.5.0.5", {"start": v(34.25, -152.37) * mm, "end": v(34.25, -171.12) * mm});
            skLineSegment(sketch, "E55.5.0.6", {"start": v(34.65, -152.37) * mm, "end": v(34.65, -171.12) * mm});
            skLineSegment(sketch, "E55.5.0.7", {"start": v(31.35, -140.5) * mm, "end": v(31.35, -159.25) * mm});
            skLineSegment(sketch, "E55.5.0.8", {"start": v(31.75, -159.25) * mm, "end": v(31.75, -140.5) * mm});
            skLineSegment(sketch, "E55.5.0.9", {"start": v(34.25, -128.62) * mm, "end": v(34.25, -147.37) * mm});
            skLineSegment(sketch, "E55.5.0.10", {"start": v(34.65, -128.62) * mm, "end": v(34.65, -147.37) * mm});
            skLineSegment(sketch, "E55.5.0.11", {"start": v(31.35, -183) * mm, "end": v(31.35, -93) * mm, "construction": true});
            skLineSegment(sketch, "E55.5.0.12", {"start": v(31.35, -116.75) * mm, "end": v(31.35, -135.5) * mm});
            skLineSegment(sketch, "E55.5.0.13", {"start": v(31.75, -116.75) * mm, "end": v(31.75, -135.5) * mm});
            skLineSegment(sketch, "E55.5.0.14", {"start": v(34.25, -104.87) * mm, "end": v(34.25, -123.62) * mm});
            skLineSegment(sketch, "E55.5.0.15", {"start": v(34.65, -104.87) * mm, "end": v(34.65, -123.62) * mm});
            skLineSegment(sketch, "E55.5.0.16", {"start": v(31.35, -93) * mm, "end": v(31.35, -111.75) * mm});
            skLineSegment(sketch, "E55.5.0.17", {"start": v(31.75, -93) * mm, "end": v(31.75, -111.75) * mm});
            skLineSegment(sketch, "E55.5.0.18", {"start": v(34.25, -99.87) * mm, "end": v(34.25, -93) * mm});
            skLineSegment(sketch, "E55.5.0.19", {"start": v(34.65, -99.87) * mm, "end": v(34.65, -93) * mm});
            skLineSegment(sketch, "E55.5.0.20", {"start": v(34.25, -176.12) * mm, "end": v(34.65, -176.12) * mm});
            skLineSegment(sketch, "E55.5.0.21", {"start": v(34.25, -171.12) * mm, "end": v(34.65, -171.12) * mm});
            skLineSegment(sketch, "E55.5.0.22", {"start": v(31.35, -164.25) * mm, "end": v(31.75, -164.25) * mm});
            skLineSegment(sketch, "E55.5.0.23", {"start": v(31.35, -159.25) * mm, "end": v(31.75, -159.25) * mm});
            skLineSegment(sketch, "E55.5.0.24", {"start": v(34.25, -152.37) * mm, "end": v(34.65, -152.37) * mm});
            skLineSegment(sketch, "E55.5.0.25", {"start": v(34.25, -147.37) * mm, "end": v(34.65, -147.37) * mm});
            skLineSegment(sketch, "E55.5.0.26", {"start": v(31.35, -140.5) * mm, "end": v(31.75, -140.5) * mm});
            skLineSegment(sketch, "E55.5.0.27", {"start": v(31.35, -135.5) * mm, "end": v(31.75, -135.5) * mm});
            skLineSegment(sketch, "E55.5.0.28", {"start": v(34.25, -128.62) * mm, "end": v(34.65, -128.62) * mm});
            skLineSegment(sketch, "E55.5.0.29", {"start": v(34.25, -123.62) * mm, "end": v(34.65, -123.62) * mm});
            skLineSegment(sketch, "E55.5.0.30", {"start": v(31.35, -116.75) * mm, "end": v(31.75, -116.75) * mm});
            skLineSegment(sketch, "E55.5.0.31", {"start": v(31.35, -111.75) * mm, "end": v(31.75, -111.75) * mm});
            skLineSegment(sketch, "E55.5.0.32", {"start": v(34.25, -104.87) * mm, "end": v(34.65, -104.87) * mm});
            skLineSegment(sketch, "E55.5.0.33", {"start": v(34.25, -99.87) * mm, "end": v(34.65, -99.87) * mm});
            skLineSegment(sketch, "E55.5.0.34", {"start": v(34.25, -183) * mm, "end": v(34.65, -183) * mm});
            skLineSegment(sketch, "E55.5.0.35", {"start": v(31.35, -183) * mm, "end": v(31.75, -183) * mm});
            skLineSegment(sketch, "E55.5.0.36", {"start": v(34.65, -183) * mm, "end": v(31.35, -183) * mm, "construction": true});
            skLineSegment(sketch, "E55.5.0.37", {"start": v(31.35, -93) * mm, "end": v(31.75, -93) * mm});
            skLineSegment(sketch, "E55.5.0.38", {"start": v(34.65, -93) * mm, "end": v(31.35, -93) * mm, "construction": true});
            skLineSegment(sketch, "E55.5.0.39", {"start": v(34.25, -93) * mm, "end": v(34.65, -93) * mm});
            skLineSegment(sketch, "E55.6.0.0", {"start": v(37.12, -164.25) * mm, "end": v(37.12, -183) * mm});
            skLineSegment(sketch, "E55.6.0.1", {"start": v(37.52, -164.25) * mm, "end": v(37.52, -183) * mm});
            skLineSegment(sketch, "E55.6.0.2", {"start": v(40.02, -176.12) * mm, "end": v(40.02, -183) * mm});
            skLineSegment(sketch, "E55.6.0.3", {"start": v(40.42, -176.12) * mm, "end": v(40.42, -183) * mm});
            skLineSegment(sketch, "E55.6.0.4", {"start": v(40.42, -183) * mm, "end": v(40.42, -93) * mm, "construction": true});
            skLineSegment(sketch, "E55.6.0.5", {"start": v(40.02, -152.37) * mm, "end": v(40.02, -171.12) * mm});
            skLineSegment(sketch, "E55.6.0.6", {"start": v(40.42, -152.37) * mm, "end": v(40.42, -171.12) * mm});
            skLineSegment(sketch, "E55.6.0.7", {"start": v(37.12, -140.5) * mm, "end": v(37.12, -159.25) * mm});
            skLineSegment(sketch, "E55.6.0.8", {"start": v(37.52, -159.25) * mm, "end": v(37.52, -140.5) * mm});
            skLineSegment(sketch, "E55.6.0.9", {"start": v(40.02, -128.62) * mm, "end": v(40.02, -147.37) * mm});
            skLineSegment(sketch, "E55.6.0.10", {"start": v(40.42, -128.62) * mm, "end": v(40.42, -147.37) * mm});
            skLineSegment(sketch, "E55.6.0.11", {"start": v(37.12, -183) * mm, "end": v(37.12, -93) * mm, "construction": true});
            skLineSegment(sketch, "E55.6.0.12", {"start": v(37.12, -116.75) * mm, "end": v(37.12, -135.5) * mm});
            skLineSegment(sketch, "E55.6.0.13", {"start": v(37.52, -116.75) * mm, "end": v(37.52, -135.5) * mm});
            skLineSegment(sketch, "E55.6.0.14", {"start": v(40.02, -104.87) * mm, "end": v(40.02, -123.62) * mm});
            skLineSegment(sketch, "E55.6.0.15", {"start": v(40.42, -104.87) * mm, "end": v(40.42, -123.62) * mm});
            skLineSegment(sketch, "E55.6.0.16", {"start": v(37.12, -93) * mm, "end": v(37.12, -111.75) * mm});
            skLineSegment(sketch, "E55.6.0.17", {"start": v(37.52, -93) * mm, "end": v(37.52, -111.75) * mm});
            skLineSegment(sketch, "E55.6.0.18", {"start": v(40.02, -99.87) * mm, "end": v(40.02, -93) * mm});
            skLineSegment(sketch, "E55.6.0.19", {"start": v(40.42, -99.87) * mm, "end": v(40.42, -93) * mm});
            skLineSegment(sketch, "E55.6.0.20", {"start": v(40.02, -176.12) * mm, "end": v(40.42, -176.12) * mm});
            skLineSegment(sketch, "E55.6.0.21", {"start": v(40.02, -171.12) * mm, "end": v(40.42, -171.12) * mm});
            skLineSegment(sketch, "E55.6.0.22", {"start": v(37.12, -164.25) * mm, "end": v(37.52, -164.25) * mm});
            skLineSegment(sketch, "E55.6.0.23", {"start": v(37.12, -159.25) * mm, "end": v(37.52, -159.25) * mm});
            skLineSegment(sketch, "E55.6.0.24", {"start": v(40.02, -152.37) * mm, "end": v(40.42, -152.37) * mm});
            skLineSegment(sketch, "E55.6.0.25", {"start": v(40.02, -147.37) * mm, "end": v(40.42, -147.37) * mm});
            skLineSegment(sketch, "E55.6.0.26", {"start": v(37.12, -140.5) * mm, "end": v(37.52, -140.5) * mm});
            skLineSegment(sketch, "E55.6.0.27", {"start": v(37.12, -135.5) * mm, "end": v(37.52, -135.5) * mm});
            skLineSegment(sketch, "E55.6.0.28", {"start": v(40.02, -128.62) * mm, "end": v(40.42, -128.62) * mm});
            skLineSegment(sketch, "E55.6.0.29", {"start": v(40.02, -123.62) * mm, "end": v(40.42, -123.62) * mm});
            skLineSegment(sketch, "E55.6.0.30", {"start": v(37.12, -116.75) * mm, "end": v(37.52, -116.75) * mm});
            skLineSegment(sketch, "E55.6.0.31", {"start": v(37.12, -111.75) * mm, "end": v(37.52, -111.75) * mm});
            skLineSegment(sketch, "E55.6.0.32", {"start": v(40.02, -104.87) * mm, "end": v(40.42, -104.87) * mm});
            skLineSegment(sketch, "E55.6.0.33", {"start": v(40.02, -99.87) * mm, "end": v(40.42, -99.87) * mm});
            skLineSegment(sketch, "E55.6.0.34", {"start": v(40.02, -183) * mm, "end": v(40.42, -183) * mm});
            skLineSegment(sketch, "E55.6.0.35", {"start": v(37.12, -183) * mm, "end": v(37.52, -183) * mm});
            skLineSegment(sketch, "E55.6.0.36", {"start": v(40.42, -183) * mm, "end": v(37.12, -183) * mm, "construction": true});
            skLineSegment(sketch, "E55.6.0.37", {"start": v(37.12, -93) * mm, "end": v(37.52, -93) * mm});
            skLineSegment(sketch, "E55.6.0.38", {"start": v(40.42, -93) * mm, "end": v(37.12, -93) * mm, "construction": true});
            skLineSegment(sketch, "E55.6.0.39", {"start": v(40.02, -93) * mm, "end": v(40.42, -93) * mm});
            skLineSegment(sketch, "E55.7.0.0", {"start": v(42.9, -164.25) * mm, "end": v(42.9, -183) * mm});
            skLineSegment(sketch, "E55.7.0.1", {"start": v(43.3, -164.25) * mm, "end": v(43.3, -183) * mm});
            skLineSegment(sketch, "E55.7.0.2", {"start": v(45.8, -176.12) * mm, "end": v(45.8, -183) * mm});
            skLineSegment(sketch, "E55.7.0.3", {"start": v(46.2, -176.12) * mm, "end": v(46.2, -183) * mm});
            skLineSegment(sketch, "E55.7.0.4", {"start": v(46.2, -183) * mm, "end": v(46.2, -93) * mm, "construction": true});
            skLineSegment(sketch, "E55.7.0.5", {"start": v(45.8, -152.37) * mm, "end": v(45.8, -171.12) * mm});
            skLineSegment(sketch, "E55.7.0.6", {"start": v(46.2, -152.37) * mm, "end": v(46.2, -171.12) * mm});
            skLineSegment(sketch, "E55.7.0.7", {"start": v(42.9, -140.5) * mm, "end": v(42.9, -159.25) * mm});
            skLineSegment(sketch, "E55.7.0.8", {"start": v(43.3, -159.25) * mm, "end": v(43.3, -140.5) * mm});
            skLineSegment(sketch, "E55.7.0.9", {"start": v(45.8, -128.62) * mm, "end": v(45.8, -147.37) * mm});
            skLineSegment(sketch, "E55.7.0.10", {"start": v(46.2, -128.62) * mm, "end": v(46.2, -147.37) * mm});
            skLineSegment(sketch, "E55.7.0.11", {"start": v(42.9, -183) * mm, "end": v(42.9, -93) * mm, "construction": true});
            skLineSegment(sketch, "E55.7.0.12", {"start": v(42.9, -116.75) * mm, "end": v(42.9, -135.5) * mm});
            skLineSegment(sketch, "E55.7.0.13", {"start": v(43.3, -116.75) * mm, "end": v(43.3, -135.5) * mm});
            skLineSegment(sketch, "E55.7.0.14", {"start": v(45.8, -104.87) * mm, "end": v(45.8, -123.62) * mm});
            skLineSegment(sketch, "E55.7.0.15", {"start": v(46.2, -104.87) * mm, "end": v(46.2, -123.62) * mm});
            skLineSegment(sketch, "E55.7.0.16", {"start": v(42.9, -93) * mm, "end": v(42.9, -111.75) * mm});
            skLineSegment(sketch, "E55.7.0.17", {"start": v(43.3, -93) * mm, "end": v(43.3, -111.75) * mm});
            skLineSegment(sketch, "E55.7.0.18", {"start": v(45.8, -99.87) * mm, "end": v(45.8, -93) * mm});
            skLineSegment(sketch, "E55.7.0.19", {"start": v(46.2, -99.87) * mm, "end": v(46.2, -93) * mm});
            skLineSegment(sketch, "E55.7.0.20", {"start": v(45.8, -176.12) * mm, "end": v(46.2, -176.12) * mm});
            skLineSegment(sketch, "E55.7.0.21", {"start": v(45.8, -171.12) * mm, "end": v(46.2, -171.12) * mm});
            skLineSegment(sketch, "E55.7.0.22", {"start": v(42.9, -164.25) * mm, "end": v(43.3, -164.25) * mm});
            skLineSegment(sketch, "E55.7.0.23", {"start": v(42.9, -159.25) * mm, "end": v(43.3, -159.25) * mm});
            skLineSegment(sketch, "E55.7.0.24", {"start": v(45.8, -152.37) * mm, "end": v(46.2, -152.37) * mm});
            skLineSegment(sketch, "E55.7.0.25", {"start": v(45.8, -147.37) * mm, "end": v(46.2, -147.37) * mm});
            skLineSegment(sketch, "E55.7.0.26", {"start": v(42.9, -140.5) * mm, "end": v(43.3, -140.5) * mm});
            skLineSegment(sketch, "E55.7.0.27", {"start": v(42.9, -135.5) * mm, "end": v(43.3, -135.5) * mm});
            skLineSegment(sketch, "E55.7.0.28", {"start": v(45.8, -128.62) * mm, "end": v(46.2, -128.62) * mm});
            skLineSegment(sketch, "E55.7.0.29", {"start": v(45.8, -123.62) * mm, "end": v(46.2, -123.62) * mm});
            skLineSegment(sketch, "E55.7.0.30", {"start": v(42.9, -116.75) * mm, "end": v(43.3, -116.75) * mm});
            skLineSegment(sketch, "E55.7.0.31", {"start": v(42.9, -111.75) * mm, "end": v(43.3, -111.75) * mm});
            skLineSegment(sketch, "E55.7.0.32", {"start": v(45.8, -104.87) * mm, "end": v(46.2, -104.87) * mm});
            skLineSegment(sketch, "E55.7.0.33", {"start": v(45.8, -99.87) * mm, "end": v(46.2, -99.87) * mm});
            skLineSegment(sketch, "E55.7.0.34", {"start": v(45.8, -183) * mm, "end": v(46.2, -183) * mm});
            skLineSegment(sketch, "E55.7.0.35", {"start": v(42.9, -183) * mm, "end": v(43.3, -183) * mm});
            skLineSegment(sketch, "E55.7.0.36", {"start": v(46.2, -183) * mm, "end": v(42.9, -183) * mm, "construction": true});
            skLineSegment(sketch, "E55.7.0.37", {"start": v(42.9, -93) * mm, "end": v(43.3, -93) * mm});
            skLineSegment(sketch, "E55.7.0.38", {"start": v(46.2, -93) * mm, "end": v(42.9, -93) * mm, "construction": true});
            skLineSegment(sketch, "E55.7.0.39", {"start": v(45.8, -93) * mm, "end": v(46.2, -93) * mm});
            skLineSegment(sketch, "E55.8.0.0", {"start": v(48.66, -164.25) * mm, "end": v(48.66, -183) * mm});
            skLineSegment(sketch, "E55.8.0.1", {"start": v(49.06, -164.25) * mm, "end": v(49.06, -183) * mm});
            skLineSegment(sketch, "E55.8.0.2", {"start": v(51.56, -176.12) * mm, "end": v(51.56, -183) * mm});
            skLineSegment(sketch, "E55.8.0.3", {"start": v(51.96, -176.12) * mm, "end": v(51.96, -183) * mm});
            skLineSegment(sketch, "E55.8.0.4", {"start": v(51.96, -183) * mm, "end": v(51.96, -93) * mm, "construction": true});
            skLineSegment(sketch, "E55.8.0.5", {"start": v(51.56, -152.37) * mm, "end": v(51.56, -171.12) * mm});
            skLineSegment(sketch, "E55.8.0.6", {"start": v(51.96, -152.37) * mm, "end": v(51.96, -171.12) * mm});
            skLineSegment(sketch, "E55.8.0.7", {"start": v(48.66, -140.5) * mm, "end": v(48.66, -159.25) * mm});
            skLineSegment(sketch, "E55.8.0.8", {"start": v(49.06, -159.25) * mm, "end": v(49.06, -140.5) * mm});
            skLineSegment(sketch, "E55.8.0.9", {"start": v(51.56, -128.62) * mm, "end": v(51.56, -147.37) * mm});
            skLineSegment(sketch, "E55.8.0.10", {"start": v(51.96, -128.62) * mm, "end": v(51.96, -147.37) * mm});
            skLineSegment(sketch, "E55.8.0.11", {"start": v(48.66, -183) * mm, "end": v(48.66, -93) * mm, "construction": true});
            skLineSegment(sketch, "E55.8.0.12", {"start": v(48.66, -116.75) * mm, "end": v(48.66, -135.5) * mm});
            skLineSegment(sketch, "E55.8.0.13", {"start": v(49.06, -116.75) * mm, "end": v(49.06, -135.5) * mm});
            skLineSegment(sketch, "E55.8.0.14", {"start": v(51.56, -104.87) * mm, "end": v(51.56, -123.62) * mm});
            skLineSegment(sketch, "E55.8.0.15", {"start": v(51.96, -104.87) * mm, "end": v(51.96, -123.62) * mm});
            skLineSegment(sketch, "E55.8.0.16", {"start": v(48.66, -93) * mm, "end": v(48.66, -111.75) * mm});
            skLineSegment(sketch, "E55.8.0.17", {"start": v(49.06, -93) * mm, "end": v(49.06, -111.75) * mm});
            skLineSegment(sketch, "E55.8.0.18", {"start": v(51.56, -99.87) * mm, "end": v(51.56, -93) * mm});
            skLineSegment(sketch, "E55.8.0.19", {"start": v(51.96, -99.87) * mm, "end": v(51.96, -93) * mm});
            skLineSegment(sketch, "E55.8.0.20", {"start": v(51.56, -176.12) * mm, "end": v(51.96, -176.12) * mm});
            skLineSegment(sketch, "E55.8.0.21", {"start": v(51.56, -171.12) * mm, "end": v(51.96, -171.12) * mm});
            skLineSegment(sketch, "E55.8.0.22", {"start": v(48.66, -164.25) * mm, "end": v(49.06, -164.25) * mm});
            skLineSegment(sketch, "E55.8.0.23", {"start": v(48.66, -159.25) * mm, "end": v(49.06, -159.25) * mm});
            skLineSegment(sketch, "E55.8.0.24", {"start": v(51.56, -152.37) * mm, "end": v(51.96, -152.37) * mm});
            skLineSegment(sketch, "E55.8.0.25", {"start": v(51.56, -147.37) * mm, "end": v(51.96, -147.37) * mm});
            skLineSegment(sketch, "E55.8.0.26", {"start": v(48.66, -140.5) * mm, "end": v(49.06, -140.5) * mm});
            skLineSegment(sketch, "E55.8.0.27", {"start": v(48.66, -135.5) * mm, "end": v(49.06, -135.5) * mm});
            skLineSegment(sketch, "E55.8.0.28", {"start": v(51.56, -128.62) * mm, "end": v(51.96, -128.62) * mm});
            skLineSegment(sketch, "E55.8.0.29", {"start": v(51.56, -123.62) * mm, "end": v(51.96, -123.62) * mm});
            skLineSegment(sketch, "E55.8.0.30", {"start": v(48.66, -116.75) * mm, "end": v(49.06, -116.75) * mm});
            skLineSegment(sketch, "E55.8.0.31", {"start": v(48.66, -111.75) * mm, "end": v(49.06, -111.75) * mm});
            skLineSegment(sketch, "E55.8.0.32", {"start": v(51.56, -104.87) * mm, "end": v(51.96, -104.87) * mm});
            skLineSegment(sketch, "E55.8.0.33", {"start": v(51.56, -99.87) * mm, "end": v(51.96, -99.87) * mm});
            skLineSegment(sketch, "E55.8.0.34", {"start": v(51.56, -183) * mm, "end": v(51.96, -183) * mm});
            skLineSegment(sketch, "E55.8.0.35", {"start": v(48.66, -183) * mm, "end": v(49.06, -183) * mm});
            skLineSegment(sketch, "E55.8.0.36", {"start": v(51.96, -183) * mm, "end": v(48.66, -183) * mm, "construction": true});
            skLineSegment(sketch, "E55.8.0.37", {"start": v(48.66, -93) * mm, "end": v(49.06, -93) * mm});
            skLineSegment(sketch, "E55.8.0.38", {"start": v(51.96, -93) * mm, "end": v(48.66, -93) * mm, "construction": true});
            skLineSegment(sketch, "E55.8.0.39", {"start": v(51.56, -93) * mm, "end": v(51.96, -93) * mm});
            skLineSegment(sketch, "E55.9.0.0", {"start": v(54.43, -164.25) * mm, "end": v(54.43, -183) * mm});
            skLineSegment(sketch, "E55.9.0.1", {"start": v(54.83, -164.25) * mm, "end": v(54.83, -183) * mm});
            skLineSegment(sketch, "E55.9.0.2", {"start": v(57.33, -176.12) * mm, "end": v(57.33, -183) * mm});
            skLineSegment(sketch, "E55.9.0.3", {"start": v(57.73, -176.12) * mm, "end": v(57.73, -183) * mm});
            skLineSegment(sketch, "E55.9.0.4", {"start": v(57.73, -183) * mm, "end": v(57.73, -93) * mm, "construction": true});
            skLineSegment(sketch, "E55.9.0.5", {"start": v(57.33, -152.37) * mm, "end": v(57.33, -171.12) * mm});
            skLineSegment(sketch, "E55.9.0.6", {"start": v(57.73, -152.37) * mm, "end": v(57.73, -171.12) * mm});
            skLineSegment(sketch, "E55.9.0.7", {"start": v(54.43, -140.5) * mm, "end": v(54.43, -159.25) * mm});
            skLineSegment(sketch, "E55.9.0.8", {"start": v(54.83, -159.25) * mm, "end": v(54.83, -140.5) * mm});
            skLineSegment(sketch, "E55.9.0.9", {"start": v(57.33, -128.62) * mm, "end": v(57.33, -147.37) * mm});
            skLineSegment(sketch, "E55.9.0.10", {"start": v(57.73, -128.62) * mm, "end": v(57.73, -147.37) * mm});
            skLineSegment(sketch, "E55.9.0.11", {"start": v(54.43, -183) * mm, "end": v(54.43, -93) * mm, "construction": true});
            skLineSegment(sketch, "E55.9.0.12", {"start": v(54.43, -116.75) * mm, "end": v(54.43, -135.5) * mm});
            skLineSegment(sketch, "E55.9.0.13", {"start": v(54.83, -116.75) * mm, "end": v(54.83, -135.5) * mm});
            skLineSegment(sketch, "E55.9.0.14", {"start": v(57.33, -104.87) * mm, "end": v(57.33, -123.62) * mm});
            skLineSegment(sketch, "E55.9.0.15", {"start": v(57.73, -104.87) * mm, "end": v(57.73, -123.62) * mm});
            skLineSegment(sketch, "E55.9.0.16", {"start": v(54.43, -93) * mm, "end": v(54.43, -111.75) * mm});
            skLineSegment(sketch, "E55.9.0.17", {"start": v(54.83, -93) * mm, "end": v(54.83, -111.75) * mm});
            skLineSegment(sketch, "E55.9.0.18", {"start": v(57.33, -99.87) * mm, "end": v(57.33, -93) * mm});
            skLineSegment(sketch, "E55.9.0.19", {"start": v(57.73, -99.87) * mm, "end": v(57.73, -93) * mm});
            skLineSegment(sketch, "E55.9.0.20", {"start": v(57.33, -176.12) * mm, "end": v(57.73, -176.12) * mm});
            skLineSegment(sketch, "E55.9.0.21", {"start": v(57.33, -171.12) * mm, "end": v(57.73, -171.12) * mm});
            skLineSegment(sketch, "E55.9.0.22", {"start": v(54.43, -164.25) * mm, "end": v(54.83, -164.25) * mm});
            skLineSegment(sketch, "E55.9.0.23", {"start": v(54.43, -159.25) * mm, "end": v(54.83, -159.25) * mm});
            skLineSegment(sketch, "E55.9.0.24", {"start": v(57.33, -152.37) * mm, "end": v(57.73, -152.37) * mm});
            skLineSegment(sketch, "E55.9.0.25", {"start": v(57.33, -147.37) * mm, "end": v(57.73, -147.37) * mm});
            skLineSegment(sketch, "E55.9.0.26", {"start": v(54.43, -140.5) * mm, "end": v(54.83, -140.5) * mm});
            skLineSegment(sketch, "E55.9.0.27", {"start": v(54.43, -135.5) * mm, "end": v(54.83, -135.5) * mm});
            skLineSegment(sketch, "E55.9.0.28", {"start": v(57.33, -128.62) * mm, "end": v(57.73, -128.62) * mm});
            skLineSegment(sketch, "E55.9.0.29", {"start": v(57.33, -123.62) * mm, "end": v(57.73, -123.62) * mm});
            skLineSegment(sketch, "E55.9.0.30", {"start": v(54.43, -116.75) * mm, "end": v(54.83, -116.75) * mm});
            skLineSegment(sketch, "E55.9.0.31", {"start": v(54.43, -111.75) * mm, "end": v(54.83, -111.75) * mm});
            skLineSegment(sketch, "E55.9.0.32", {"start": v(57.33, -104.87) * mm, "end": v(57.73, -104.87) * mm});
            skLineSegment(sketch, "E55.9.0.33", {"start": v(57.33, -99.87) * mm, "end": v(57.73, -99.87) * mm});
            skLineSegment(sketch, "E55.9.0.34", {"start": v(57.33, -183) * mm, "end": v(57.73, -183) * mm});
            skLineSegment(sketch, "E55.9.0.35", {"start": v(54.43, -183) * mm, "end": v(54.83, -183) * mm});
            skLineSegment(sketch, "E55.9.0.36", {"start": v(57.73, -183) * mm, "end": v(54.43, -183) * mm, "construction": true});
            skLineSegment(sketch, "E55.9.0.37", {"start": v(54.43, -93) * mm, "end": v(54.83, -93) * mm});
            skLineSegment(sketch, "E55.9.0.38", {"start": v(57.73, -93) * mm, "end": v(54.43, -93) * mm, "construction": true});
            skLineSegment(sketch, "E55.9.0.39", {"start": v(57.33, -93) * mm, "end": v(57.73, -93) * mm});
            skLineSegment(sketch, "E55.10.0.0", {"start": v(60.2, -164.25) * mm, "end": v(60.2, -183) * mm});
            skLineSegment(sketch, "E55.10.0.1", {"start": v(60.6, -164.25) * mm, "end": v(60.6, -183) * mm});
            skLineSegment(sketch, "E55.10.0.2", {"start": v(63.1, -176.12) * mm, "end": v(63.1, -183) * mm});
            skLineSegment(sketch, "E55.10.0.3", {"start": v(63.5, -176.12) * mm, "end": v(63.5, -183) * mm});
            skLineSegment(sketch, "E55.10.0.4", {"start": v(63.5, -183) * mm, "end": v(63.5, -93) * mm, "construction": true});
            skLineSegment(sketch, "E55.10.0.5", {"start": v(63.1, -152.37) * mm, "end": v(63.1, -171.12) * mm});
            skLineSegment(sketch, "E55.10.0.6", {"start": v(63.5, -152.37) * mm, "end": v(63.5, -171.12) * mm});
            skLineSegment(sketch, "E55.10.0.7", {"start": v(60.2, -140.5) * mm, "end": v(60.2, -159.25) * mm});
            skLineSegment(sketch, "E55.10.0.8", {"start": v(60.6, -159.25) * mm, "end": v(60.6, -140.5) * mm});
            skLineSegment(sketch, "E55.10.0.9", {"start": v(63.1, -128.62) * mm, "end": v(63.1, -147.37) * mm});
            skLineSegment(sketch, "E55.10.0.10", {"start": v(63.5, -128.62) * mm, "end": v(63.5, -147.37) * mm});
            skLineSegment(sketch, "E55.10.0.11", {"start": v(60.2, -183) * mm, "end": v(60.2, -93) * mm, "construction": true});
            skLineSegment(sketch, "E55.10.0.12", {"start": v(60.2, -116.75) * mm, "end": v(60.2, -135.5) * mm});
            skLineSegment(sketch, "E55.10.0.13", {"start": v(60.6, -116.75) * mm, "end": v(60.6, -135.5) * mm});
            skLineSegment(sketch, "E55.10.0.14", {"start": v(63.1, -104.87) * mm, "end": v(63.1, -123.62) * mm});
            skLineSegment(sketch, "E55.10.0.15", {"start": v(63.5, -104.87) * mm, "end": v(63.5, -123.62) * mm});
            skLineSegment(sketch, "E55.10.0.16", {"start": v(60.2, -93) * mm, "end": v(60.2, -111.75) * mm});
            skLineSegment(sketch, "E55.10.0.17", {"start": v(60.6, -93) * mm, "end": v(60.6, -111.75) * mm});
            skLineSegment(sketch, "E55.10.0.18", {"start": v(63.1, -99.87) * mm, "end": v(63.1, -93) * mm});
            skLineSegment(sketch, "E55.10.0.19", {"start": v(63.5, -99.87) * mm, "end": v(63.5, -93) * mm});
            skLineSegment(sketch, "E55.10.0.20", {"start": v(63.1, -176.12) * mm, "end": v(63.5, -176.12) * mm});
            skLineSegment(sketch, "E55.10.0.21", {"start": v(63.1, -171.12) * mm, "end": v(63.5, -171.12) * mm});
            skLineSegment(sketch, "E55.10.0.22", {"start": v(60.2, -164.25) * mm, "end": v(60.6, -164.25) * mm});
            skLineSegment(sketch, "E55.10.0.23", {"start": v(60.2, -159.25) * mm, "end": v(60.6, -159.25) * mm});
            skLineSegment(sketch, "E55.10.0.24", {"start": v(63.1, -152.37) * mm, "end": v(63.5, -152.37) * mm});
            skLineSegment(sketch, "E55.10.0.25", {"start": v(63.1, -147.37) * mm, "end": v(63.5, -147.37) * mm});
            skLineSegment(sketch, "E55.10.0.26", {"start": v(60.2, -140.5) * mm, "end": v(60.6, -140.5) * mm});
            skLineSegment(sketch, "E55.10.0.27", {"start": v(60.2, -135.5) * mm, "end": v(60.6, -135.5) * mm});
            skLineSegment(sketch, "E55.10.0.28", {"start": v(63.1, -128.62) * mm, "end": v(63.5, -128.62) * mm});
            skLineSegment(sketch, "E55.10.0.29", {"start": v(63.1, -123.62) * mm, "end": v(63.5, -123.62) * mm});
            skLineSegment(sketch, "E55.10.0.30", {"start": v(60.2, -116.75) * mm, "end": v(60.6, -116.75) * mm});
            skLineSegment(sketch, "E55.10.0.31", {"start": v(60.2, -111.75) * mm, "end": v(60.6, -111.75) * mm});
            skLineSegment(sketch, "E55.10.0.32", {"start": v(63.1, -104.87) * mm, "end": v(63.5, -104.87) * mm});
            skLineSegment(sketch, "E55.10.0.33", {"start": v(63.1, -99.87) * mm, "end": v(63.5, -99.87) * mm});
            skLineSegment(sketch, "E55.10.0.34", {"start": v(63.1, -183) * mm, "end": v(63.5, -183) * mm});
            skLineSegment(sketch, "E55.10.0.35", {"start": v(60.2, -183) * mm, "end": v(60.6, -183) * mm});
            skLineSegment(sketch, "E55.10.0.36", {"start": v(63.5, -183) * mm, "end": v(60.2, -183) * mm, "construction": true});
            skLineSegment(sketch, "E55.10.0.37", {"start": v(60.2, -93) * mm, "end": v(60.6, -93) * mm});
            skLineSegment(sketch, "E55.10.0.38", {"start": v(63.5, -93) * mm, "end": v(60.2, -93) * mm, "construction": true});
            skLineSegment(sketch, "E55.10.0.39", {"start": v(63.1, -93) * mm, "end": v(63.5, -93) * mm});
            skLineSegment(sketch, "E55.11.0.0", {"start": v(65.97, -164.25) * mm, "end": v(65.97, -183) * mm});
            skLineSegment(sketch, "E55.11.0.1", {"start": v(66.37, -164.25) * mm, "end": v(66.37, -183) * mm});
            skLineSegment(sketch, "E55.11.0.2", {"start": v(68.87, -176.12) * mm, "end": v(68.87, -183) * mm});
            skLineSegment(sketch, "E55.11.0.3", {"start": v(69.27, -176.12) * mm, "end": v(69.27, -183) * mm});
            skLineSegment(sketch, "E55.11.0.4", {"start": v(69.27, -183) * mm, "end": v(69.27, -93) * mm, "construction": true});
            skLineSegment(sketch, "E55.11.0.5", {"start": v(68.87, -152.37) * mm, "end": v(68.87, -171.12) * mm});
            skLineSegment(sketch, "E55.11.0.6", {"start": v(69.27, -152.37) * mm, "end": v(69.27, -171.12) * mm});
            skLineSegment(sketch, "E55.11.0.7", {"start": v(65.97, -140.5) * mm, "end": v(65.97, -159.25) * mm});
            skLineSegment(sketch, "E55.11.0.8", {"start": v(66.37, -159.25) * mm, "end": v(66.37, -140.5) * mm});
            skLineSegment(sketch, "E55.11.0.9", {"start": v(68.87, -128.62) * mm, "end": v(68.87, -147.37) * mm});
            skLineSegment(sketch, "E55.11.0.10", {"start": v(69.27, -128.62) * mm, "end": v(69.27, -147.37) * mm});
            skLineSegment(sketch, "E55.11.0.11", {"start": v(65.97, -183) * mm, "end": v(65.97, -93) * mm, "construction": true});
            skLineSegment(sketch, "E55.11.0.12", {"start": v(65.97, -116.75) * mm, "end": v(65.97, -135.5) * mm});
            skLineSegment(sketch, "E55.11.0.13", {"start": v(66.37, -116.75) * mm, "end": v(66.37, -135.5) * mm});
            skLineSegment(sketch, "E55.11.0.14", {"start": v(68.87, -104.87) * mm, "end": v(68.87, -123.62) * mm});
            skLineSegment(sketch, "E55.11.0.15", {"start": v(69.27, -104.87) * mm, "end": v(69.27, -123.62) * mm});
            skLineSegment(sketch, "E55.11.0.16", {"start": v(65.97, -93) * mm, "end": v(65.97, -111.75) * mm});
            skLineSegment(sketch, "E55.11.0.17", {"start": v(66.37, -93) * mm, "end": v(66.37, -111.75) * mm});
            skLineSegment(sketch, "E55.11.0.18", {"start": v(68.87, -99.87) * mm, "end": v(68.87, -93) * mm});
            skLineSegment(sketch, "E55.11.0.19", {"start": v(69.27, -99.87) * mm, "end": v(69.27, -93) * mm});
            skLineSegment(sketch, "E55.11.0.20", {"start": v(68.87, -176.12) * mm, "end": v(69.27, -176.12) * mm});
            skLineSegment(sketch, "E55.11.0.21", {"start": v(68.87, -171.12) * mm, "end": v(69.27, -171.12) * mm});
            skLineSegment(sketch, "E55.11.0.22", {"start": v(65.97, -164.25) * mm, "end": v(66.37, -164.25) * mm});
            skLineSegment(sketch, "E55.11.0.23", {"start": v(65.97, -159.25) * mm, "end": v(66.37, -159.25) * mm});
            skLineSegment(sketch, "E55.11.0.24", {"start": v(68.87, -152.37) * mm, "end": v(69.27, -152.37) * mm});
            skLineSegment(sketch, "E55.11.0.25", {"start": v(68.87, -147.37) * mm, "end": v(69.27, -147.37) * mm});
            skLineSegment(sketch, "E55.11.0.26", {"start": v(65.97, -140.5) * mm, "end": v(66.37, -140.5) * mm});
            skLineSegment(sketch, "E55.11.0.27", {"start": v(65.97, -135.5) * mm, "end": v(66.37, -135.5) * mm});
            skLineSegment(sketch, "E55.11.0.28", {"start": v(68.87, -128.62) * mm, "end": v(69.27, -128.62) * mm});
            skLineSegment(sketch, "E55.11.0.29", {"start": v(68.87, -123.62) * mm, "end": v(69.27, -123.62) * mm});
            skLineSegment(sketch, "E55.11.0.30", {"start": v(65.97, -116.75) * mm, "end": v(66.37, -116.75) * mm});
            skLineSegment(sketch, "E55.11.0.31", {"start": v(65.97, -111.75) * mm, "end": v(66.37, -111.75) * mm});
            skLineSegment(sketch, "E55.11.0.32", {"start": v(68.87, -104.87) * mm, "end": v(69.27, -104.87) * mm});
            skLineSegment(sketch, "E55.11.0.33", {"start": v(68.87, -99.87) * mm, "end": v(69.27, -99.87) * mm});
            skLineSegment(sketch, "E55.11.0.34", {"start": v(68.87, -183) * mm, "end": v(69.27, -183) * mm});
            skLineSegment(sketch, "E55.11.0.35", {"start": v(65.97, -183) * mm, "end": v(66.37, -183) * mm});
            skLineSegment(sketch, "E55.11.0.36", {"start": v(69.27, -183) * mm, "end": v(65.97, -183) * mm, "construction": true});
            skLineSegment(sketch, "E55.11.0.37", {"start": v(65.97, -93) * mm, "end": v(66.37, -93) * mm});
            skLineSegment(sketch, "E55.11.0.38", {"start": v(69.27, -93) * mm, "end": v(65.97, -93) * mm, "construction": true});
            skLineSegment(sketch, "E55.11.0.39", {"start": v(68.87, -93) * mm, "end": v(69.27, -93) * mm});
            skLineSegment(sketch, "E55.12.0.0", {"start": v(71.74, -164.25) * mm, "end": v(71.74, -183) * mm});
            skLineSegment(sketch, "E55.12.0.1", {"start": v(72.14, -164.25) * mm, "end": v(72.14, -183) * mm});
            skLineSegment(sketch, "E55.12.0.2", {"start": v(74.64, -176.12) * mm, "end": v(74.64, -183) * mm});
            skLineSegment(sketch, "E55.12.0.3", {"start": v(75.04, -176.12) * mm, "end": v(75.04, -183) * mm});
            skLineSegment(sketch, "E55.12.0.4", {"start": v(75.04, -183) * mm, "end": v(75.04, -93) * mm, "construction": true});
            skLineSegment(sketch, "E55.12.0.5", {"start": v(74.64, -152.37) * mm, "end": v(74.64, -171.12) * mm});
            skLineSegment(sketch, "E55.12.0.6", {"start": v(75.04, -152.37) * mm, "end": v(75.04, -171.12) * mm});
            skLineSegment(sketch, "E55.12.0.7", {"start": v(71.74, -140.5) * mm, "end": v(71.74, -159.25) * mm});
            skLineSegment(sketch, "E55.12.0.8", {"start": v(72.14, -159.25) * mm, "end": v(72.14, -140.5) * mm});
            skLineSegment(sketch, "E55.12.0.9", {"start": v(74.64, -128.62) * mm, "end": v(74.64, -147.37) * mm});
            skLineSegment(sketch, "E55.12.0.10", {"start": v(75.04, -128.62) * mm, "end": v(75.04, -147.37) * mm});
            skLineSegment(sketch, "E55.12.0.11", {"start": v(71.74, -183) * mm, "end": v(71.74, -93) * mm, "construction": true});
            skLineSegment(sketch, "E55.12.0.12", {"start": v(71.74, -116.75) * mm, "end": v(71.74, -135.5) * mm});
            skLineSegment(sketch, "E55.12.0.13", {"start": v(72.14, -116.75) * mm, "end": v(72.14, -135.5) * mm});
            skLineSegment(sketch, "E55.12.0.14", {"start": v(74.64, -104.87) * mm, "end": v(74.64, -123.62) * mm});
            skLineSegment(sketch, "E55.12.0.15", {"start": v(75.04, -104.87) * mm, "end": v(75.04, -123.62) * mm});
            skLineSegment(sketch, "E55.12.0.16", {"start": v(71.74, -93) * mm, "end": v(71.74, -111.75) * mm});
            skLineSegment(sketch, "E55.12.0.17", {"start": v(72.14, -93) * mm, "end": v(72.14, -111.75) * mm});
            skLineSegment(sketch, "E55.12.0.18", {"start": v(74.64, -99.87) * mm, "end": v(74.64, -93) * mm});
            skLineSegment(sketch, "E55.12.0.19", {"start": v(75.04, -99.87) * mm, "end": v(75.04, -93) * mm});
            skLineSegment(sketch, "E55.12.0.20", {"start": v(74.64, -176.12) * mm, "end": v(75.04, -176.12) * mm});
            skLineSegment(sketch, "E55.12.0.21", {"start": v(74.64, -171.12) * mm, "end": v(75.04, -171.12) * mm});
            skLineSegment(sketch, "E55.12.0.22", {"start": v(71.74, -164.25) * mm, "end": v(72.14, -164.25) * mm});
            skLineSegment(sketch, "E55.12.0.23", {"start": v(71.74, -159.25) * mm, "end": v(72.14, -159.25) * mm});
            skLineSegment(sketch, "E55.12.0.24", {"start": v(74.64, -152.37) * mm, "end": v(75.04, -152.37) * mm});
            skLineSegment(sketch, "E55.12.0.25", {"start": v(74.64, -147.37) * mm, "end": v(75.04, -147.37) * mm});
            skLineSegment(sketch, "E55.12.0.26", {"start": v(71.74, -140.5) * mm, "end": v(72.14, -140.5) * mm});
            skLineSegment(sketch, "E55.12.0.27", {"start": v(71.74, -135.5) * mm, "end": v(72.14, -135.5) * mm});
            skLineSegment(sketch, "E55.12.0.28", {"start": v(74.64, -128.62) * mm, "end": v(75.04, -128.62) * mm});
            skLineSegment(sketch, "E55.12.0.29", {"start": v(74.64, -123.62) * mm, "end": v(75.04, -123.62) * mm});
            skLineSegment(sketch, "E55.12.0.30", {"start": v(71.74, -116.75) * mm, "end": v(72.14, -116.75) * mm});
            skLineSegment(sketch, "E55.12.0.31", {"start": v(71.74, -111.75) * mm, "end": v(72.14, -111.75) * mm});
            skLineSegment(sketch, "E55.12.0.32", {"start": v(74.64, -104.87) * mm, "end": v(75.04, -104.87) * mm});
            skLineSegment(sketch, "E55.12.0.33", {"start": v(74.64, -99.87) * mm, "end": v(75.04, -99.87) * mm});
            skLineSegment(sketch, "E55.12.0.34", {"start": v(74.64, -183) * mm, "end": v(75.04, -183) * mm});
            skLineSegment(sketch, "E55.12.0.35", {"start": v(71.74, -183) * mm, "end": v(72.14, -183) * mm});
            skLineSegment(sketch, "E55.12.0.36", {"start": v(75.04, -183) * mm, "end": v(71.74, -183) * mm, "construction": true});
            skLineSegment(sketch, "E55.12.0.37", {"start": v(71.74, -93) * mm, "end": v(72.14, -93) * mm});
            skLineSegment(sketch, "E55.12.0.38", {"start": v(75.04, -93) * mm, "end": v(71.74, -93) * mm, "construction": true});
            skLineSegment(sketch, "E55.12.0.39", {"start": v(74.64, -93) * mm, "end": v(75.04, -93) * mm});
            skLineSegment(sketch, "E55.13.0.0", {"start": v(77.51, -164.25) * mm, "end": v(77.51, -183) * mm});
            skLineSegment(sketch, "E55.13.0.1", {"start": v(77.91, -164.25) * mm, "end": v(77.91, -183) * mm});
            skLineSegment(sketch, "E55.13.0.2", {"start": v(80.41, -176.12) * mm, "end": v(80.41, -183) * mm});
            skLineSegment(sketch, "E55.13.0.3", {"start": v(80.81, -176.12) * mm, "end": v(80.81, -183) * mm});
            skLineSegment(sketch, "E55.13.0.4", {"start": v(80.81, -183) * mm, "end": v(80.81, -93) * mm, "construction": true});
            skLineSegment(sketch, "E55.13.0.5", {"start": v(80.41, -152.37) * mm, "end": v(80.41, -171.12) * mm});
            skLineSegment(sketch, "E55.13.0.6", {"start": v(80.81, -152.37) * mm, "end": v(80.81, -171.12) * mm});
            skLineSegment(sketch, "E55.13.0.7", {"start": v(77.51, -140.5) * mm, "end": v(77.51, -159.25) * mm});
            skLineSegment(sketch, "E55.13.0.8", {"start": v(77.91, -159.25) * mm, "end": v(77.91, -140.5) * mm});
            skLineSegment(sketch, "E55.13.0.9", {"start": v(80.41, -128.62) * mm, "end": v(80.41, -147.37) * mm});
            skLineSegment(sketch, "E55.13.0.10", {"start": v(80.81, -128.62) * mm, "end": v(80.81, -147.37) * mm});
            skLineSegment(sketch, "E55.13.0.11", {"start": v(77.51, -183) * mm, "end": v(77.5, -93) * mm, "construction": true});
            skLineSegment(sketch, "E55.13.0.12", {"start": v(77.51, -116.75) * mm, "end": v(77.51, -135.5) * mm});
            skLineSegment(sketch, "E55.13.0.13", {"start": v(77.91, -116.75) * mm, "end": v(77.91, -135.5) * mm});
            skLineSegment(sketch, "E55.13.0.14", {"start": v(80.41, -104.87) * mm, "end": v(80.41, -123.62) * mm});
            skLineSegment(sketch, "E55.13.0.15", {"start": v(80.81, -104.87) * mm, "end": v(80.81, -123.62) * mm});
            skLineSegment(sketch, "E55.13.0.16", {"start": v(77.51, -93) * mm, "end": v(77.51, -111.75) * mm});
            skLineSegment(sketch, "E55.13.0.17", {"start": v(77.91, -93) * mm, "end": v(77.91, -111.75) * mm});
            skLineSegment(sketch, "E55.13.0.18", {"start": v(80.41, -99.87) * mm, "end": v(80.41, -93) * mm});
            skLineSegment(sketch, "E55.13.0.19", {"start": v(80.81, -99.87) * mm, "end": v(80.81, -93) * mm});
            skLineSegment(sketch, "E55.13.0.20", {"start": v(80.41, -176.12) * mm, "end": v(80.81, -176.12) * mm});
            skLineSegment(sketch, "E55.13.0.21", {"start": v(80.41, -171.12) * mm, "end": v(80.81, -171.12) * mm});
            skLineSegment(sketch, "E55.13.0.22", {"start": v(77.51, -164.25) * mm, "end": v(77.91, -164.25) * mm});
            skLineSegment(sketch, "E55.13.0.23", {"start": v(77.51, -159.25) * mm, "end": v(77.91, -159.25) * mm});
            skLineSegment(sketch, "E55.13.0.24", {"start": v(80.41, -152.37) * mm, "end": v(80.81, -152.37) * mm});
            skLineSegment(sketch, "E55.13.0.25", {"start": v(80.41, -147.37) * mm, "end": v(80.81, -147.37) * mm});
            skLineSegment(sketch, "E55.13.0.26", {"start": v(77.51, -140.5) * mm, "end": v(77.91, -140.5) * mm});
            skLineSegment(sketch, "E55.13.0.27", {"start": v(77.51, -135.5) * mm, "end": v(77.91, -135.5) * mm});
            skLineSegment(sketch, "E55.13.0.28", {"start": v(80.41, -128.62) * mm, "end": v(80.81, -128.62) * mm});
            skLineSegment(sketch, "E55.13.0.29", {"start": v(80.41, -123.62) * mm, "end": v(80.81, -123.62) * mm});
            skLineSegment(sketch, "E55.13.0.30", {"start": v(77.51, -116.75) * mm, "end": v(77.91, -116.75) * mm});
            skLineSegment(sketch, "E55.13.0.31", {"start": v(77.51, -111.75) * mm, "end": v(77.91, -111.75) * mm});
            skLineSegment(sketch, "E55.13.0.32", {"start": v(80.41, -104.87) * mm, "end": v(80.81, -104.87) * mm});
            skLineSegment(sketch, "E55.13.0.33", {"start": v(80.41, -99.87) * mm, "end": v(80.81, -99.87) * mm});
            skLineSegment(sketch, "E55.13.0.34", {"start": v(80.41, -183) * mm, "end": v(80.81, -183) * mm});
            skLineSegment(sketch, "E55.13.0.35", {"start": v(77.51, -183) * mm, "end": v(77.91, -183) * mm});
            skLineSegment(sketch, "E55.13.0.36", {"start": v(80.81, -183) * mm, "end": v(77.51, -183) * mm, "construction": true});
            skLineSegment(sketch, "E55.13.0.37", {"start": v(77.51, -93) * mm, "end": v(77.91, -93) * mm});
            skLineSegment(sketch, "E55.13.0.38", {"start": v(80.81, -93) * mm, "end": v(77.51, -93) * mm, "construction": true});
            skLineSegment(sketch, "E55.13.0.39", {"start": v(80.41, -93) * mm, "end": v(80.81, -93) * mm});
            skLineSegment(sketch, "E55.14.0.0", {"start": v(83.28, -164.25) * mm, "end": v(83.28, -183) * mm});
            skLineSegment(sketch, "E55.14.0.1", {"start": v(83.68, -164.25) * mm, "end": v(83.68, -183) * mm});
            skLineSegment(sketch, "E55.14.0.2", {"start": v(86.18, -176.12) * mm, "end": v(86.18, -183) * mm});
            skLineSegment(sketch, "E55.14.0.3", {"start": v(86.58, -176.12) * mm, "end": v(86.58, -183) * mm});
            skLineSegment(sketch, "E55.14.0.4", {"start": v(86.58, -183) * mm, "end": v(86.58, -93) * mm, "construction": true});
            skLineSegment(sketch, "E55.14.0.5", {"start": v(86.18, -152.37) * mm, "end": v(86.18, -171.12) * mm});
            skLineSegment(sketch, "E55.14.0.6", {"start": v(86.58, -152.37) * mm, "end": v(86.58, -171.12) * mm});
            skLineSegment(sketch, "E55.14.0.7", {"start": v(83.28, -140.5) * mm, "end": v(83.28, -159.25) * mm});
            skLineSegment(sketch, "E55.14.0.8", {"start": v(83.68, -159.25) * mm, "end": v(83.68, -140.5) * mm});
            skLineSegment(sketch, "E55.14.0.9", {"start": v(86.18, -128.62) * mm, "end": v(86.18, -147.37) * mm});
            skLineSegment(sketch, "E55.14.0.10", {"start": v(86.58, -128.62) * mm, "end": v(86.58, -147.37) * mm});
            skLineSegment(sketch, "E55.14.0.11", {"start": v(83.28, -183) * mm, "end": v(83.28, -93) * mm, "construction": true});
            skLineSegment(sketch, "E55.14.0.12", {"start": v(83.28, -116.75) * mm, "end": v(83.28, -135.5) * mm});
            skLineSegment(sketch, "E55.14.0.13", {"start": v(83.68, -116.75) * mm, "end": v(83.68, -135.5) * mm});
            skLineSegment(sketch, "E55.14.0.14", {"start": v(86.18, -104.87) * mm, "end": v(86.18, -123.62) * mm});
            skLineSegment(sketch, "E55.14.0.15", {"start": v(86.58, -104.87) * mm, "end": v(86.58, -123.62) * mm});
            skLineSegment(sketch, "E55.14.0.16", {"start": v(83.28, -93) * mm, "end": v(83.28, -111.75) * mm});
            skLineSegment(sketch, "E55.14.0.17", {"start": v(83.68, -93) * mm, "end": v(83.68, -111.75) * mm});
            skLineSegment(sketch, "E55.14.0.18", {"start": v(86.18, -99.87) * mm, "end": v(86.18, -93) * mm});
            skLineSegment(sketch, "E55.14.0.19", {"start": v(86.58, -99.87) * mm, "end": v(86.58, -93) * mm});
            skLineSegment(sketch, "E55.14.0.20", {"start": v(86.18, -176.12) * mm, "end": v(86.58, -176.12) * mm});
            skLineSegment(sketch, "E55.14.0.21", {"start": v(86.18, -171.12) * mm, "end": v(86.58, -171.12) * mm});
            skLineSegment(sketch, "E55.14.0.22", {"start": v(83.28, -164.25) * mm, "end": v(83.68, -164.25) * mm});
            skLineSegment(sketch, "E55.14.0.23", {"start": v(83.28, -159.25) * mm, "end": v(83.68, -159.25) * mm});
            skLineSegment(sketch, "E55.14.0.24", {"start": v(86.18, -152.37) * mm, "end": v(86.58, -152.37) * mm});
            skLineSegment(sketch, "E55.14.0.25", {"start": v(86.18, -147.37) * mm, "end": v(86.58, -147.37) * mm});
            skLineSegment(sketch, "E55.14.0.26", {"start": v(83.28, -140.5) * mm, "end": v(83.68, -140.5) * mm});
            skLineSegment(sketch, "E55.14.0.27", {"start": v(83.28, -135.5) * mm, "end": v(83.68, -135.5) * mm});
            skLineSegment(sketch, "E55.14.0.28", {"start": v(86.18, -128.62) * mm, "end": v(86.58, -128.62) * mm});
            skLineSegment(sketch, "E55.14.0.29", {"start": v(86.18, -123.62) * mm, "end": v(86.58, -123.62) * mm});
            skLineSegment(sketch, "E55.14.0.30", {"start": v(83.28, -116.75) * mm, "end": v(83.68, -116.75) * mm});
            skLineSegment(sketch, "E55.14.0.31", {"start": v(83.28, -111.75) * mm, "end": v(83.68, -111.75) * mm});
            skLineSegment(sketch, "E55.14.0.32", {"start": v(86.18, -104.87) * mm, "end": v(86.58, -104.87) * mm});
            skLineSegment(sketch, "E55.14.0.33", {"start": v(86.18, -99.87) * mm, "end": v(86.58, -99.87) * mm});
            skLineSegment(sketch, "E55.14.0.34", {"start": v(86.18, -183) * mm, "end": v(86.58, -183) * mm});
            skLineSegment(sketch, "E55.14.0.35", {"start": v(83.28, -183) * mm, "end": v(83.68, -183) * mm});
            skLineSegment(sketch, "E55.14.0.36", {"start": v(86.58, -183) * mm, "end": v(83.28, -183) * mm, "construction": true});
            skLineSegment(sketch, "E55.14.0.37", {"start": v(83.28, -93) * mm, "end": v(83.68, -93) * mm});
            skLineSegment(sketch, "E55.14.0.38", {"start": v(86.58, -93) * mm, "end": v(83.28, -93) * mm, "construction": true});
            skLineSegment(sketch, "E55.14.0.39", {"start": v(86.18, -93) * mm, "end": v(86.58, -93) * mm});
            skLineSegment(sketch, "E55.15.0.0", {"start": v(89.05, -164.25) * mm, "end": v(89.05, -183) * mm});
            skLineSegment(sketch, "E55.15.0.1", {"start": v(89.45, -164.25) * mm, "end": v(89.45, -183) * mm});
            skLineSegment(sketch, "E55.15.0.2", {"start": v(91.95, -176.12) * mm, "end": v(91.95, -183) * mm});
            skLineSegment(sketch, "E55.15.0.3", {"start": v(92.35, -176.12) * mm, "end": v(92.35, -183) * mm});
            skLineSegment(sketch, "E55.15.0.4", {"start": v(92.35, -183) * mm, "end": v(92.35, -93) * mm, "construction": true});
            skLineSegment(sketch, "E55.15.0.5", {"start": v(91.95, -152.37) * mm, "end": v(91.95, -171.12) * mm});
            skLineSegment(sketch, "E55.15.0.6", {"start": v(92.35, -152.37) * mm, "end": v(92.35, -171.12) * mm});
            skLineSegment(sketch, "E55.15.0.7", {"start": v(89.05, -140.5) * mm, "end": v(89.05, -159.25) * mm});
            skLineSegment(sketch, "E55.15.0.8", {"start": v(89.45, -159.25) * mm, "end": v(89.45, -140.5) * mm});
            skLineSegment(sketch, "E55.15.0.9", {"start": v(91.95, -128.62) * mm, "end": v(91.95, -147.37) * mm});
            skLineSegment(sketch, "E55.15.0.10", {"start": v(92.35, -128.62) * mm, "end": v(92.35, -147.37) * mm});
            skLineSegment(sketch, "E55.15.0.11", {"start": v(89.05, -183) * mm, "end": v(89.05, -93) * mm, "construction": true});
            skLineSegment(sketch, "E55.15.0.12", {"start": v(89.05, -116.75) * mm, "end": v(89.05, -135.5) * mm});
            skLineSegment(sketch, "E55.15.0.13", {"start": v(89.45, -116.75) * mm, "end": v(89.45, -135.5) * mm});
            skLineSegment(sketch, "E55.15.0.14", {"start": v(91.95, -104.87) * mm, "end": v(91.95, -123.62) * mm});
            skLineSegment(sketch, "E55.15.0.15", {"start": v(92.35, -104.87) * mm, "end": v(92.35, -123.62) * mm});
            skLineSegment(sketch, "E55.15.0.16", {"start": v(89.05, -93) * mm, "end": v(89.05, -111.75) * mm});
            skLineSegment(sketch, "E55.15.0.17", {"start": v(89.45, -93) * mm, "end": v(89.45, -111.75) * mm});
            skLineSegment(sketch, "E55.15.0.18", {"start": v(91.95, -99.87) * mm, "end": v(91.95, -93) * mm});
            skLineSegment(sketch, "E55.15.0.19", {"start": v(92.35, -99.87) * mm, "end": v(92.35, -93) * mm});
            skLineSegment(sketch, "E55.15.0.20", {"start": v(91.95, -176.12) * mm, "end": v(92.35, -176.12) * mm});
            skLineSegment(sketch, "E55.15.0.21", {"start": v(91.95, -171.12) * mm, "end": v(92.35, -171.12) * mm});
            skLineSegment(sketch, "E55.15.0.22", {"start": v(89.05, -164.25) * mm, "end": v(89.45, -164.25) * mm});
            skLineSegment(sketch, "E55.15.0.23", {"start": v(89.05, -159.25) * mm, "end": v(89.45, -159.25) * mm});
            skLineSegment(sketch, "E55.15.0.24", {"start": v(91.95, -152.37) * mm, "end": v(92.35, -152.37) * mm});
            skLineSegment(sketch, "E55.15.0.25", {"start": v(91.95, -147.37) * mm, "end": v(92.35, -147.37) * mm});
            skLineSegment(sketch, "E55.15.0.26", {"start": v(89.05, -140.5) * mm, "end": v(89.45, -140.5) * mm});
            skLineSegment(sketch, "E55.15.0.27", {"start": v(89.05, -135.5) * mm, "end": v(89.45, -135.5) * mm});
            skLineSegment(sketch, "E55.15.0.28", {"start": v(91.95, -128.62) * mm, "end": v(92.35, -128.62) * mm});
            skLineSegment(sketch, "E55.15.0.29", {"start": v(91.95, -123.62) * mm, "end": v(92.35, -123.62) * mm});
            skLineSegment(sketch, "E55.15.0.30", {"start": v(89.05, -116.75) * mm, "end": v(89.45, -116.75) * mm});
            skLineSegment(sketch, "E55.15.0.31", {"start": v(89.05, -111.75) * mm, "end": v(89.45, -111.75) * mm});
            skLineSegment(sketch, "E55.15.0.32", {"start": v(91.95, -104.87) * mm, "end": v(92.35, -104.87) * mm});
            skLineSegment(sketch, "E55.15.0.33", {"start": v(91.95, -99.87) * mm, "end": v(92.35, -99.87) * mm});
            skLineSegment(sketch, "E55.15.0.34", {"start": v(91.95, -183) * mm, "end": v(92.35, -183) * mm});
            skLineSegment(sketch, "E55.15.0.35", {"start": v(89.05, -183) * mm, "end": v(89.45, -183) * mm});
            skLineSegment(sketch, "E55.15.0.36", {"start": v(92.35, -183) * mm, "end": v(89.05, -183) * mm, "construction": true});
            skLineSegment(sketch, "E55.15.0.37", {"start": v(89.05, -93) * mm, "end": v(89.45, -93) * mm});
            skLineSegment(sketch, "E55.15.0.38", {"start": v(92.35, -93) * mm, "end": v(89.05, -93) * mm, "construction": true});
            skLineSegment(sketch, "E55.15.0.39", {"start": v(91.95, -93) * mm, "end": v(92.35, -93) * mm});
            skLineSegment(sketch, "E55.16.0.0", {"start": v(94.82, -164.25) * mm, "end": v(94.82, -183) * mm});
            skLineSegment(sketch, "E55.16.0.1", {"start": v(95.22, -164.25) * mm, "end": v(95.22, -183) * mm});
            skLineSegment(sketch, "E55.16.0.2", {"start": v(97.72, -176.12) * mm, "end": v(97.72, -183) * mm});
            skLineSegment(sketch, "E55.16.0.3", {"start": v(98.12, -176.12) * mm, "end": v(98.12, -183) * mm});
            skLineSegment(sketch, "E55.16.0.4", {"start": v(98.12, -183) * mm, "end": v(98.12, -93) * mm, "construction": true});
            skLineSegment(sketch, "E55.16.0.5", {"start": v(97.72, -152.37) * mm, "end": v(97.72, -171.12) * mm});
            skLineSegment(sketch, "E55.16.0.6", {"start": v(98.12, -152.37) * mm, "end": v(98.12, -171.12) * mm});
            skLineSegment(sketch, "E55.16.0.7", {"start": v(94.82, -140.5) * mm, "end": v(94.82, -159.25) * mm});
            skLineSegment(sketch, "E55.16.0.8", {"start": v(95.22, -159.25) * mm, "end": v(95.22, -140.5) * mm});
            skLineSegment(sketch, "E55.16.0.9", {"start": v(97.72, -128.62) * mm, "end": v(97.72, -147.37) * mm});
            skLineSegment(sketch, "E55.16.0.10", {"start": v(98.12, -128.62) * mm, "end": v(98.12, -147.37) * mm});
            skLineSegment(sketch, "E55.16.0.11", {"start": v(94.82, -183) * mm, "end": v(94.82, -93) * mm, "construction": true});
            skLineSegment(sketch, "E55.16.0.12", {"start": v(94.82, -116.75) * mm, "end": v(94.82, -135.5) * mm});
            skLineSegment(sketch, "E55.16.0.13", {"start": v(95.22, -116.75) * mm, "end": v(95.22, -135.5) * mm});
            skLineSegment(sketch, "E55.16.0.14", {"start": v(97.72, -104.87) * mm, "end": v(97.72, -123.62) * mm});
            skLineSegment(sketch, "E55.16.0.15", {"start": v(98.12, -104.87) * mm, "end": v(98.12, -123.62) * mm});
            skLineSegment(sketch, "E55.16.0.16", {"start": v(94.82, -93) * mm, "end": v(94.82, -111.75) * mm});
            skLineSegment(sketch, "E55.16.0.17", {"start": v(95.22, -93) * mm, "end": v(95.22, -111.75) * mm});
            skLineSegment(sketch, "E55.16.0.18", {"start": v(97.72, -99.87) * mm, "end": v(97.72, -93) * mm});
            skLineSegment(sketch, "E55.16.0.19", {"start": v(98.12, -99.87) * mm, "end": v(98.12, -93) * mm});
            skLineSegment(sketch, "E55.16.0.20", {"start": v(97.72, -176.12) * mm, "end": v(98.12, -176.12) * mm});
            skLineSegment(sketch, "E55.16.0.21", {"start": v(97.72, -171.12) * mm, "end": v(98.12, -171.12) * mm});
            skLineSegment(sketch, "E55.16.0.22", {"start": v(94.82, -164.25) * mm, "end": v(95.22, -164.25) * mm});
            skLineSegment(sketch, "E55.16.0.23", {"start": v(94.82, -159.25) * mm, "end": v(95.22, -159.25) * mm});
            skLineSegment(sketch, "E55.16.0.24", {"start": v(97.72, -152.37) * mm, "end": v(98.12, -152.37) * mm});
            skLineSegment(sketch, "E55.16.0.25", {"start": v(97.72, -147.37) * mm, "end": v(98.12, -147.37) * mm});
            skLineSegment(sketch, "E55.16.0.26", {"start": v(94.82, -140.5) * mm, "end": v(95.22, -140.5) * mm});
            skLineSegment(sketch, "E55.16.0.27", {"start": v(94.82, -135.5) * mm, "end": v(95.22, -135.5) * mm});
            skLineSegment(sketch, "E55.16.0.28", {"start": v(97.72, -128.62) * mm, "end": v(98.12, -128.62) * mm});
            skLineSegment(sketch, "E55.16.0.29", {"start": v(97.72, -123.62) * mm, "end": v(98.12, -123.62) * mm});
            skLineSegment(sketch, "E55.16.0.30", {"start": v(94.82, -116.75) * mm, "end": v(95.22, -116.75) * mm});
            skLineSegment(sketch, "E55.16.0.31", {"start": v(94.82, -111.75) * mm, "end": v(95.22, -111.75) * mm});
            skLineSegment(sketch, "E55.16.0.32", {"start": v(97.72, -104.87) * mm, "end": v(98.12, -104.87) * mm});
            skLineSegment(sketch, "E55.16.0.33", {"start": v(97.72, -99.87) * mm, "end": v(98.12, -99.87) * mm});
            skLineSegment(sketch, "E55.16.0.34", {"start": v(97.72, -183) * mm, "end": v(98.12, -183) * mm});
            skLineSegment(sketch, "E55.16.0.35", {"start": v(94.82, -183) * mm, "end": v(95.22, -183) * mm});
            skLineSegment(sketch, "E55.16.0.36", {"start": v(98.12, -183) * mm, "end": v(94.82, -183) * mm, "construction": true});
            skLineSegment(sketch, "E55.16.0.37", {"start": v(94.82, -93) * mm, "end": v(95.22, -93) * mm});
            skLineSegment(sketch, "E55.16.0.38", {"start": v(98.12, -93) * mm, "end": v(94.82, -93) * mm, "construction": true});
            skLineSegment(sketch, "E55.16.0.39", {"start": v(97.72, -93) * mm, "end": v(98.12, -93) * mm});
            skLineSegment(sketch, "E55.17.0.0", {"start": v(100.6, -164.25) * mm, "end": v(100.6, -183) * mm});
            skLineSegment(sketch, "E55.17.0.1", {"start": v(101, -164.25) * mm, "end": v(101, -183) * mm});
            skLineSegment(sketch, "E55.17.0.2", {"start": v(103.5, -176.12) * mm, "end": v(103.5, -183) * mm});
            skLineSegment(sketch, "E55.17.0.3", {"start": v(103.9, -176.12) * mm, "end": v(103.9, -183) * mm});
            skLineSegment(sketch, "E55.17.0.4", {"start": v(103.9, -183) * mm, "end": v(103.9, -93) * mm, "construction": true});
            skLineSegment(sketch, "E55.17.0.5", {"start": v(103.5, -152.37) * mm, "end": v(103.5, -171.12) * mm});
            skLineSegment(sketch, "E55.17.0.6", {"start": v(103.9, -152.37) * mm, "end": v(103.9, -171.12) * mm});
            skLineSegment(sketch, "E55.17.0.7", {"start": v(100.6, -140.5) * mm, "end": v(100.6, -159.25) * mm});
            skLineSegment(sketch, "E55.17.0.8", {"start": v(101, -159.25) * mm, "end": v(101, -140.5) * mm});
            skLineSegment(sketch, "E55.17.0.9", {"start": v(103.5, -128.62) * mm, "end": v(103.5, -147.37) * mm});
            skLineSegment(sketch, "E55.17.0.10", {"start": v(103.9, -128.62) * mm, "end": v(103.9, -147.37) * mm});
            skLineSegment(sketch, "E55.17.0.11", {"start": v(100.6, -183) * mm, "end": v(100.6, -93) * mm, "construction": true});
            skLineSegment(sketch, "E55.17.0.12", {"start": v(100.6, -116.75) * mm, "end": v(100.6, -135.5) * mm});
            skLineSegment(sketch, "E55.17.0.13", {"start": v(101, -116.75) * mm, "end": v(101, -135.5) * mm});
            skLineSegment(sketch, "E55.17.0.14", {"start": v(103.5, -104.87) * mm, "end": v(103.5, -123.62) * mm});
            skLineSegment(sketch, "E55.17.0.15", {"start": v(103.9, -104.87) * mm, "end": v(103.9, -123.62) * mm});
            skLineSegment(sketch, "E55.17.0.16", {"start": v(100.6, -93) * mm, "end": v(100.6, -111.75) * mm});
            skLineSegment(sketch, "E55.17.0.17", {"start": v(101, -93) * mm, "end": v(101, -111.75) * mm});
            skLineSegment(sketch, "E55.17.0.18", {"start": v(103.5, -99.87) * mm, "end": v(103.5, -93) * mm});
            skLineSegment(sketch, "E55.17.0.19", {"start": v(103.9, -99.87) * mm, "end": v(103.9, -93) * mm});
            skLineSegment(sketch, "E55.17.0.20", {"start": v(103.5, -176.12) * mm, "end": v(103.9, -176.12) * mm});
            skLineSegment(sketch, "E55.17.0.21", {"start": v(103.5, -171.12) * mm, "end": v(103.9, -171.12) * mm});
            skLineSegment(sketch, "E55.17.0.22", {"start": v(100.6, -164.25) * mm, "end": v(101, -164.25) * mm});
            skLineSegment(sketch, "E55.17.0.23", {"start": v(100.6, -159.25) * mm, "end": v(101, -159.25) * mm});
            skLineSegment(sketch, "E55.17.0.24", {"start": v(103.5, -152.37) * mm, "end": v(103.9, -152.37) * mm});
            skLineSegment(sketch, "E55.17.0.25", {"start": v(103.5, -147.37) * mm, "end": v(103.9, -147.37) * mm});
            skLineSegment(sketch, "E55.17.0.26", {"start": v(100.6, -140.5) * mm, "end": v(101, -140.5) * mm});
            skLineSegment(sketch, "E55.17.0.27", {"start": v(100.6, -135.5) * mm, "end": v(101, -135.5) * mm});
            skLineSegment(sketch, "E55.17.0.28", {"start": v(103.5, -128.62) * mm, "end": v(103.9, -128.62) * mm});
            skLineSegment(sketch, "E55.17.0.29", {"start": v(103.5, -123.62) * mm, "end": v(103.9, -123.62) * mm});
            skLineSegment(sketch, "E55.17.0.30", {"start": v(100.6, -116.75) * mm, "end": v(101, -116.75) * mm});
            skLineSegment(sketch, "E55.17.0.31", {"start": v(100.6, -111.75) * mm, "end": v(101, -111.75) * mm});
            skLineSegment(sketch, "E55.17.0.32", {"start": v(103.49, -104.87) * mm, "end": v(103.9, -104.87) * mm});
            skLineSegment(sketch, "E55.17.0.33", {"start": v(103.49, -99.87) * mm, "end": v(103.9, -99.87) * mm});
            skLineSegment(sketch, "E55.17.0.34", {"start": v(103.5, -183) * mm, "end": v(103.9, -183) * mm});
            skLineSegment(sketch, "E55.17.0.35", {"start": v(100.6, -183) * mm, "end": v(101, -183) * mm});
            skLineSegment(sketch, "E55.17.0.36", {"start": v(103.9, -183) * mm, "end": v(100.6, -183) * mm, "construction": true});
            skLineSegment(sketch, "E55.17.0.37", {"start": v(100.6, -93) * mm, "end": v(101, -93) * mm});
            skLineSegment(sketch, "E55.17.0.38", {"start": v(103.9, -93) * mm, "end": v(100.6, -93) * mm, "construction": true});
            skLineSegment(sketch, "E55.17.0.39", {"start": v(103.5, -93) * mm, "end": v(103.9, -93) * mm});
            skLineSegment(sketch, "E55.18.0.0", {"start": v(106.36, -164.25) * mm, "end": v(106.36, -183) * mm});
            skLineSegment(sketch, "E55.18.0.1", {"start": v(106.76, -164.25) * mm, "end": v(106.76, -183) * mm});
            skLineSegment(sketch, "E55.18.0.2", {"start": v(109.26, -176.12) * mm, "end": v(109.26, -183) * mm});
            skLineSegment(sketch, "E55.18.0.3", {"start": v(109.66, -176.12) * mm, "end": v(109.66, -183) * mm});
            skLineSegment(sketch, "E55.18.0.4", {"start": v(109.66, -183) * mm, "end": v(109.66, -93) * mm, "construction": true});
            skLineSegment(sketch, "E55.18.0.5", {"start": v(109.26, -152.37) * mm, "end": v(109.26, -171.12) * mm});
            skLineSegment(sketch, "E55.18.0.6", {"start": v(109.66, -152.37) * mm, "end": v(109.66, -171.12) * mm});
            skLineSegment(sketch, "E55.18.0.7", {"start": v(106.36, -140.5) * mm, "end": v(106.36, -159.25) * mm});
            skLineSegment(sketch, "E55.18.0.8", {"start": v(106.76, -159.25) * mm, "end": v(106.76, -140.5) * mm});
            skLineSegment(sketch, "E55.18.0.9", {"start": v(109.26, -128.62) * mm, "end": v(109.26, -147.37) * mm});
            skLineSegment(sketch, "E55.18.0.10", {"start": v(109.66, -128.62) * mm, "end": v(109.66, -147.37) * mm});
            skLineSegment(sketch, "E55.18.0.11", {"start": v(106.36, -183) * mm, "end": v(106.36, -93) * mm, "construction": true});
            skLineSegment(sketch, "E55.18.0.12", {"start": v(106.36, -116.75) * mm, "end": v(106.36, -135.5) * mm});
            skLineSegment(sketch, "E55.18.0.13", {"start": v(106.76, -116.75) * mm, "end": v(106.76, -135.5) * mm});
            skLineSegment(sketch, "E55.18.0.14", {"start": v(109.26, -104.87) * mm, "end": v(109.26, -123.62) * mm});
            skLineSegment(sketch, "E55.18.0.15", {"start": v(109.66, -104.87) * mm, "end": v(109.66, -123.62) * mm});
            skLineSegment(sketch, "E55.18.0.16", {"start": v(106.36, -93) * mm, "end": v(106.36, -111.75) * mm});
            skLineSegment(sketch, "E55.18.0.17", {"start": v(106.76, -93) * mm, "end": v(106.76, -111.75) * mm});
            skLineSegment(sketch, "E55.18.0.18", {"start": v(109.26, -99.87) * mm, "end": v(109.26, -93) * mm});
            skLineSegment(sketch, "E55.18.0.19", {"start": v(109.66, -99.87) * mm, "end": v(109.66, -93) * mm});
            skLineSegment(sketch, "E55.18.0.20", {"start": v(109.26, -176.12) * mm, "end": v(109.66, -176.12) * mm});
            skLineSegment(sketch, "E55.18.0.21", {"start": v(109.26, -171.12) * mm, "end": v(109.66, -171.12) * mm});
            skLineSegment(sketch, "E55.18.0.22", {"start": v(106.36, -164.25) * mm, "end": v(106.76, -164.25) * mm});
            skLineSegment(sketch, "E55.18.0.23", {"start": v(106.36, -159.25) * mm, "end": v(106.76, -159.25) * mm});
            skLineSegment(sketch, "E55.18.0.24", {"start": v(109.26, -152.37) * mm, "end": v(109.66, -152.37) * mm});
            skLineSegment(sketch, "E55.18.0.25", {"start": v(109.26, -147.37) * mm, "end": v(109.66, -147.37) * mm});
            skLineSegment(sketch, "E55.18.0.26", {"start": v(106.36, -140.5) * mm, "end": v(106.76, -140.5) * mm});
            skLineSegment(sketch, "E55.18.0.27", {"start": v(106.36, -135.5) * mm, "end": v(106.76, -135.5) * mm});
            skLineSegment(sketch, "E55.18.0.28", {"start": v(109.26, -128.62) * mm, "end": v(109.66, -128.62) * mm});
            skLineSegment(sketch, "E55.18.0.29", {"start": v(109.26, -123.62) * mm, "end": v(109.66, -123.62) * mm});
            skLineSegment(sketch, "E55.18.0.30", {"start": v(106.36, -116.75) * mm, "end": v(106.76, -116.75) * mm});
            skLineSegment(sketch, "E55.18.0.31", {"start": v(106.36, -111.75) * mm, "end": v(106.76, -111.75) * mm});
            skLineSegment(sketch, "E55.18.0.32", {"start": v(109.26, -104.87) * mm, "end": v(109.66, -104.87) * mm});
            skLineSegment(sketch, "E55.18.0.33", {"start": v(109.26, -99.87) * mm, "end": v(109.66, -99.87) * mm});
            skLineSegment(sketch, "E55.18.0.34", {"start": v(109.26, -183) * mm, "end": v(109.66, -183) * mm});
            skLineSegment(sketch, "E55.18.0.35", {"start": v(106.36, -183) * mm, "end": v(106.76, -183) * mm});
            skLineSegment(sketch, "E55.18.0.36", {"start": v(109.66, -183) * mm, "end": v(106.36, -183) * mm, "construction": true});
            skLineSegment(sketch, "E55.18.0.37", {"start": v(106.36, -93) * mm, "end": v(106.76, -93) * mm});
            skLineSegment(sketch, "E55.18.0.38", {"start": v(109.66, -93) * mm, "end": v(106.36, -93) * mm, "construction": true});
            skLineSegment(sketch, "E55.18.0.39", {"start": v(109.26, -93) * mm, "end": v(109.66, -93) * mm});
            skLineSegment(sketch, "E55.19.0.0", {"start": v(112.13, -164.25) * mm, "end": v(112.13, -183) * mm});
            skLineSegment(sketch, "E55.19.0.1", {"start": v(112.53, -164.25) * mm, "end": v(112.53, -183) * mm});
            skLineSegment(sketch, "E55.19.0.2", {"start": v(115.03, -176.12) * mm, "end": v(115.03, -183) * mm});
            skLineSegment(sketch, "E55.19.0.3", {"start": v(115.43, -176.12) * mm, "end": v(115.43, -183) * mm});
            skLineSegment(sketch, "E55.19.0.4", {"start": v(115.43, -183) * mm, "end": v(115.43, -93) * mm, "construction": true});
            skLineSegment(sketch, "E55.19.0.5", {"start": v(115.03, -152.37) * mm, "end": v(115.03, -171.12) * mm});
            skLineSegment(sketch, "E55.19.0.6", {"start": v(115.43, -152.37) * mm, "end": v(115.43, -171.12) * mm});
            skLineSegment(sketch, "E55.19.0.7", {"start": v(112.13, -140.5) * mm, "end": v(112.13, -159.25) * mm});
            skLineSegment(sketch, "E55.19.0.8", {"start": v(112.53, -159.25) * mm, "end": v(112.53, -140.5) * mm});
            skLineSegment(sketch, "E55.19.0.9", {"start": v(115.03, -128.62) * mm, "end": v(115.03, -147.37) * mm});
            skLineSegment(sketch, "E55.19.0.10", {"start": v(115.43, -128.62) * mm, "end": v(115.43, -147.37) * mm});
            skLineSegment(sketch, "E55.19.0.11", {"start": v(112.13, -183) * mm, "end": v(112.13, -93) * mm, "construction": true});
            skLineSegment(sketch, "E55.19.0.12", {"start": v(112.13, -116.75) * mm, "end": v(112.13, -135.5) * mm});
            skLineSegment(sketch, "E55.19.0.13", {"start": v(112.53, -116.75) * mm, "end": v(112.53, -135.5) * mm});
            skLineSegment(sketch, "E55.19.0.14", {"start": v(115.03, -104.87) * mm, "end": v(115.03, -123.62) * mm});
            skLineSegment(sketch, "E55.19.0.15", {"start": v(115.43, -104.87) * mm, "end": v(115.43, -123.62) * mm});
            skLineSegment(sketch, "E55.19.0.16", {"start": v(112.13, -93) * mm, "end": v(112.13, -111.75) * mm});
            skLineSegment(sketch, "E55.19.0.17", {"start": v(112.53, -93) * mm, "end": v(112.53, -111.75) * mm});
            skLineSegment(sketch, "E55.19.0.18", {"start": v(115.03, -99.87) * mm, "end": v(115.03, -93) * mm});
            skLineSegment(sketch, "E55.19.0.19", {"start": v(115.43, -99.87) * mm, "end": v(115.43, -93) * mm});
            skLineSegment(sketch, "E55.19.0.20", {"start": v(115.03, -176.12) * mm, "end": v(115.43, -176.12) * mm});
            skLineSegment(sketch, "E55.19.0.21", {"start": v(115.03, -171.12) * mm, "end": v(115.43, -171.12) * mm});
            skLineSegment(sketch, "E55.19.0.22", {"start": v(112.13, -164.25) * mm, "end": v(112.53, -164.25) * mm});
            skLineSegment(sketch, "E55.19.0.23", {"start": v(112.13, -159.25) * mm, "end": v(112.53, -159.25) * mm});
            skLineSegment(sketch, "E55.19.0.24", {"start": v(115.03, -152.37) * mm, "end": v(115.43, -152.37) * mm});
            skLineSegment(sketch, "E55.19.0.25", {"start": v(115.03, -147.37) * mm, "end": v(115.43, -147.37) * mm});
            skLineSegment(sketch, "E55.19.0.26", {"start": v(112.13, -140.5) * mm, "end": v(112.53, -140.5) * mm});
            skLineSegment(sketch, "E55.19.0.27", {"start": v(112.13, -135.5) * mm, "end": v(112.53, -135.5) * mm});
            skLineSegment(sketch, "E55.19.0.28", {"start": v(115.03, -128.62) * mm, "end": v(115.43, -128.62) * mm});
            skLineSegment(sketch, "E55.19.0.29", {"start": v(115.03, -123.62) * mm, "end": v(115.43, -123.62) * mm});
            skLineSegment(sketch, "E55.19.0.30", {"start": v(112.13, -116.75) * mm, "end": v(112.53, -116.75) * mm});
            skLineSegment(sketch, "E55.19.0.31", {"start": v(112.13, -111.75) * mm, "end": v(112.53, -111.75) * mm});
            skLineSegment(sketch, "E55.19.0.32", {"start": v(115.03, -104.87) * mm, "end": v(115.43, -104.87) * mm});
            skLineSegment(sketch, "E55.19.0.33", {"start": v(115.03, -99.87) * mm, "end": v(115.43, -99.87) * mm});
            skLineSegment(sketch, "E55.19.0.34", {"start": v(115.03, -183) * mm, "end": v(115.43, -183) * mm});
            skLineSegment(sketch, "E55.19.0.35", {"start": v(112.13, -183) * mm, "end": v(112.53, -183) * mm});
            skLineSegment(sketch, "E55.19.0.36", {"start": v(115.43, -183) * mm, "end": v(112.13, -183) * mm, "construction": true});
            skLineSegment(sketch, "E55.19.0.37", {"start": v(112.13, -93) * mm, "end": v(112.53, -93) * mm});
            skLineSegment(sketch, "E55.19.0.38", {"start": v(115.43, -93) * mm, "end": v(112.13, -93) * mm, "construction": true});
            skLineSegment(sketch, "E55.19.0.39", {"start": v(115.03, -93) * mm, "end": v(115.43, -93) * mm});
            skLineSegment(sketch, "E55.20.0.0", {"start": v(117.9, -164.25) * mm, "end": v(117.9, -183) * mm});
            skLineSegment(sketch, "E55.20.0.1", {"start": v(118.3, -164.25) * mm, "end": v(118.3, -183) * mm});
            skLineSegment(sketch, "E55.20.0.2", {"start": v(120.8, -176.12) * mm, "end": v(120.8, -183) * mm});
            skLineSegment(sketch, "E55.20.0.3", {"start": v(121.2, -176.12) * mm, "end": v(121.2, -183) * mm});
            skLineSegment(sketch, "E55.20.0.4", {"start": v(121.2, -183) * mm, "end": v(121.2, -93) * mm, "construction": true});
            skLineSegment(sketch, "E55.20.0.5", {"start": v(120.8, -152.37) * mm, "end": v(120.8, -171.12) * mm});
            skLineSegment(sketch, "E55.20.0.6", {"start": v(121.2, -152.37) * mm, "end": v(121.2, -171.12) * mm});
            skLineSegment(sketch, "E55.20.0.7", {"start": v(117.9, -140.5) * mm, "end": v(117.9, -159.25) * mm});
            skLineSegment(sketch, "E55.20.0.8", {"start": v(118.3, -159.25) * mm, "end": v(118.3, -140.5) * mm});
            skLineSegment(sketch, "E55.20.0.9", {"start": v(120.8, -128.62) * mm, "end": v(120.8, -147.37) * mm});
            skLineSegment(sketch, "E55.20.0.10", {"start": v(121.2, -128.62) * mm, "end": v(121.2, -147.37) * mm});
            skLineSegment(sketch, "E55.20.0.11", {"start": v(117.9, -183) * mm, "end": v(117.9, -93) * mm, "construction": true});
            skLineSegment(sketch, "E55.20.0.12", {"start": v(117.9, -116.75) * mm, "end": v(117.9, -135.5) * mm});
            skLineSegment(sketch, "E55.20.0.13", {"start": v(118.3, -116.75) * mm, "end": v(118.3, -135.5) * mm});
            skLineSegment(sketch, "E55.20.0.14", {"start": v(120.8, -104.87) * mm, "end": v(120.8, -123.62) * mm});
            skLineSegment(sketch, "E55.20.0.15", {"start": v(121.2, -104.87) * mm, "end": v(121.2, -123.62) * mm});
            skLineSegment(sketch, "E55.20.0.16", {"start": v(117.9, -93) * mm, "end": v(117.9, -111.75) * mm});
            skLineSegment(sketch, "E55.20.0.17", {"start": v(118.3, -93) * mm, "end": v(118.3, -111.75) * mm});
            skLineSegment(sketch, "E55.20.0.18", {"start": v(120.8, -99.87) * mm, "end": v(120.8, -93) * mm});
            skLineSegment(sketch, "E55.20.0.19", {"start": v(121.2, -99.87) * mm, "end": v(121.2, -93) * mm});
            skLineSegment(sketch, "E55.20.0.20", {"start": v(120.8, -176.12) * mm, "end": v(121.2, -176.12) * mm});
            skLineSegment(sketch, "E55.20.0.21", {"start": v(120.8, -171.12) * mm, "end": v(121.2, -171.12) * mm});
            skLineSegment(sketch, "E55.20.0.22", {"start": v(117.9, -164.25) * mm, "end": v(118.3, -164.25) * mm});
            skLineSegment(sketch, "E55.20.0.23", {"start": v(117.9, -159.25) * mm, "end": v(118.3, -159.25) * mm});
            skLineSegment(sketch, "E55.20.0.24", {"start": v(120.8, -152.37) * mm, "end": v(121.2, -152.37) * mm});
            skLineSegment(sketch, "E55.20.0.25", {"start": v(120.8, -147.37) * mm, "end": v(121.2, -147.37) * mm});
            skLineSegment(sketch, "E55.20.0.26", {"start": v(117.9, -140.5) * mm, "end": v(118.3, -140.5) * mm});
            skLineSegment(sketch, "E55.20.0.27", {"start": v(117.9, -135.5) * mm, "end": v(118.3, -135.5) * mm});
            skLineSegment(sketch, "E55.20.0.28", {"start": v(120.8, -128.62) * mm, "end": v(121.2, -128.62) * mm});
            skLineSegment(sketch, "E55.20.0.29", {"start": v(120.8, -123.62) * mm, "end": v(121.2, -123.62) * mm});
            skLineSegment(sketch, "E55.20.0.30", {"start": v(117.9, -116.75) * mm, "end": v(118.3, -116.75) * mm});
            skLineSegment(sketch, "E55.20.0.31", {"start": v(117.9, -111.75) * mm, "end": v(118.3, -111.75) * mm});
            skLineSegment(sketch, "E55.20.0.32", {"start": v(120.8, -104.87) * mm, "end": v(121.2, -104.87) * mm});
            skLineSegment(sketch, "E55.20.0.33", {"start": v(120.8, -99.87) * mm, "end": v(121.2, -99.87) * mm});
            skLineSegment(sketch, "E55.20.0.34", {"start": v(120.8, -183) * mm, "end": v(121.2, -183) * mm});
            skLineSegment(sketch, "E55.20.0.35", {"start": v(117.9, -183) * mm, "end": v(118.3, -183) * mm});
            skLineSegment(sketch, "E55.20.0.36", {"start": v(121.2, -183) * mm, "end": v(117.9, -183) * mm, "construction": true});
            skLineSegment(sketch, "E55.20.0.37", {"start": v(117.9, -93) * mm, "end": v(118.3, -93) * mm});
            skLineSegment(sketch, "E55.20.0.38", {"start": v(121.2, -93) * mm, "end": v(117.9, -93) * mm, "construction": true});
            skLineSegment(sketch, "E55.20.0.39", {"start": v(120.8, -93) * mm, "end": v(121.2, -93) * mm});
            skLineSegment(sketch, "E55.21.0.0", {"start": v(123.67, -164.25) * mm, "end": v(123.67, -183) * mm});
            skLineSegment(sketch, "E55.21.0.1", {"start": v(124.07, -164.25) * mm, "end": v(124.07, -183) * mm});
            skLineSegment(sketch, "E55.21.0.2", {"start": v(126.57, -176.12) * mm, "end": v(126.57, -183) * mm});
            skLineSegment(sketch, "E55.21.0.3", {"start": v(126.97, -176.12) * mm, "end": v(126.97, -183) * mm});
            skLineSegment(sketch, "E55.21.0.4", {"start": v(126.97, -183) * mm, "end": v(126.97, -93) * mm, "construction": true});
            skLineSegment(sketch, "E55.21.0.5", {"start": v(126.57, -152.37) * mm, "end": v(126.57, -171.12) * mm});
            skLineSegment(sketch, "E55.21.0.6", {"start": v(126.97, -152.37) * mm, "end": v(126.97, -171.12) * mm});
            skLineSegment(sketch, "E55.21.0.7", {"start": v(123.67, -140.5) * mm, "end": v(123.67, -159.25) * mm});
            skLineSegment(sketch, "E55.21.0.8", {"start": v(124.07, -159.25) * mm, "end": v(124.07, -140.5) * mm});
            skLineSegment(sketch, "E55.21.0.9", {"start": v(126.57, -128.62) * mm, "end": v(126.57, -147.37) * mm});
            skLineSegment(sketch, "E55.21.0.10", {"start": v(126.97, -128.62) * mm, "end": v(126.97, -147.37) * mm});
            skLineSegment(sketch, "E55.21.0.11", {"start": v(123.67, -183) * mm, "end": v(123.67, -93) * mm, "construction": true});
            skLineSegment(sketch, "E55.21.0.12", {"start": v(123.67, -116.75) * mm, "end": v(123.67, -135.5) * mm});
            skLineSegment(sketch, "E55.21.0.13", {"start": v(124.07, -116.75) * mm, "end": v(124.07, -135.5) * mm});
            skLineSegment(sketch, "E55.21.0.14", {"start": v(126.57, -104.87) * mm, "end": v(126.57, -123.62) * mm});
            skLineSegment(sketch, "E55.21.0.15", {"start": v(126.97, -104.87) * mm, "end": v(126.97, -123.62) * mm});
            skLineSegment(sketch, "E55.21.0.16", {"start": v(123.67, -93) * mm, "end": v(123.67, -111.75) * mm});
            skLineSegment(sketch, "E55.21.0.17", {"start": v(124.07, -93) * mm, "end": v(124.07, -111.75) * mm});
            skLineSegment(sketch, "E55.21.0.18", {"start": v(126.57, -99.87) * mm, "end": v(126.57, -93) * mm});
            skLineSegment(sketch, "E55.21.0.19", {"start": v(126.97, -99.87) * mm, "end": v(126.97, -93) * mm});
            skLineSegment(sketch, "E55.21.0.20", {"start": v(126.57, -176.12) * mm, "end": v(126.97, -176.12) * mm});
            skLineSegment(sketch, "E55.21.0.21", {"start": v(126.57, -171.12) * mm, "end": v(126.97, -171.12) * mm});
            skLineSegment(sketch, "E55.21.0.22", {"start": v(123.67, -164.25) * mm, "end": v(124.07, -164.25) * mm});
            skLineSegment(sketch, "E55.21.0.23", {"start": v(123.67, -159.25) * mm, "end": v(124.07, -159.25) * mm});
            skLineSegment(sketch, "E55.21.0.24", {"start": v(126.57, -152.37) * mm, "end": v(126.97, -152.37) * mm});
            skLineSegment(sketch, "E55.21.0.25", {"start": v(126.57, -147.37) * mm, "end": v(126.97, -147.37) * mm});
            skLineSegment(sketch, "E55.21.0.26", {"start": v(123.67, -140.5) * mm, "end": v(124.07, -140.5) * mm});
            skLineSegment(sketch, "E55.21.0.27", {"start": v(123.67, -135.5) * mm, "end": v(124.07, -135.5) * mm});
            skLineSegment(sketch, "E55.21.0.28", {"start": v(126.57, -128.62) * mm, "end": v(126.97, -128.62) * mm});
            skLineSegment(sketch, "E55.21.0.29", {"start": v(126.57, -123.62) * mm, "end": v(126.97, -123.62) * mm});
            skLineSegment(sketch, "E55.21.0.30", {"start": v(123.67, -116.75) * mm, "end": v(124.07, -116.75) * mm});
            skLineSegment(sketch, "E55.21.0.31", {"start": v(123.67, -111.75) * mm, "end": v(124.07, -111.75) * mm});
            skLineSegment(sketch, "E55.21.0.32", {"start": v(126.57, -104.87) * mm, "end": v(126.97, -104.87) * mm});
            skLineSegment(sketch, "E55.21.0.33", {"start": v(126.57, -99.87) * mm, "end": v(126.97, -99.87) * mm});
            skLineSegment(sketch, "E55.21.0.34", {"start": v(126.57, -183) * mm, "end": v(126.97, -183) * mm});
            skLineSegment(sketch, "E55.21.0.35", {"start": v(123.67, -183) * mm, "end": v(124.07, -183) * mm});
            skLineSegment(sketch, "E55.21.0.36", {"start": v(126.97, -183) * mm, "end": v(123.67, -183) * mm, "construction": true});
            skLineSegment(sketch, "E55.21.0.37", {"start": v(123.67, -93) * mm, "end": v(124.07, -93) * mm});
            skLineSegment(sketch, "E55.21.0.38", {"start": v(126.97, -93) * mm, "end": v(123.67, -93) * mm, "construction": true});
            skLineSegment(sketch, "E55.21.0.39", {"start": v(126.57, -93) * mm, "end": v(126.97, -93) * mm});
            skLineSegment(sketch, "E55.22.0.0", {"start": v(129.44, -164.25) * mm, "end": v(129.44, -183) * mm});
            skLineSegment(sketch, "E55.22.0.1", {"start": v(129.84, -164.25) * mm, "end": v(129.84, -183) * mm});
            skLineSegment(sketch, "E55.22.0.2", {"start": v(132.34, -176.12) * mm, "end": v(132.34, -183) * mm});
            skLineSegment(sketch, "E55.22.0.3", {"start": v(132.74, -176.12) * mm, "end": v(132.74, -183) * mm});
            skLineSegment(sketch, "E55.22.0.4", {"start": v(132.74, -183) * mm, "end": v(132.74, -93) * mm, "construction": true});
            skLineSegment(sketch, "E55.22.0.5", {"start": v(132.34, -152.37) * mm, "end": v(132.34, -171.12) * mm});
            skLineSegment(sketch, "E55.22.0.6", {"start": v(132.74, -152.37) * mm, "end": v(132.74, -171.12) * mm});
            skLineSegment(sketch, "E55.22.0.7", {"start": v(129.44, -140.5) * mm, "end": v(129.44, -159.25) * mm});
            skLineSegment(sketch, "E55.22.0.8", {"start": v(129.84, -159.25) * mm, "end": v(129.84, -140.5) * mm});
            skLineSegment(sketch, "E55.22.0.9", {"start": v(132.34, -128.62) * mm, "end": v(132.34, -147.37) * mm});
            skLineSegment(sketch, "E55.22.0.10", {"start": v(132.74, -128.62) * mm, "end": v(132.74, -147.37) * mm});
            skLineSegment(sketch, "E55.22.0.11", {"start": v(129.44, -183) * mm, "end": v(129.44, -93) * mm, "construction": true});
            skLineSegment(sketch, "E55.22.0.12", {"start": v(129.44, -116.75) * mm, "end": v(129.44, -135.5) * mm});
            skLineSegment(sketch, "E55.22.0.13", {"start": v(129.84, -116.75) * mm, "end": v(129.84, -135.5) * mm});
            skLineSegment(sketch, "E55.22.0.14", {"start": v(132.34, -104.87) * mm, "end": v(132.34, -123.62) * mm});
            skLineSegment(sketch, "E55.22.0.15", {"start": v(132.74, -104.87) * mm, "end": v(132.74, -123.62) * mm});
            skLineSegment(sketch, "E55.22.0.16", {"start": v(129.44, -93) * mm, "end": v(129.44, -111.75) * mm});
            skLineSegment(sketch, "E55.22.0.17", {"start": v(129.84, -93) * mm, "end": v(129.84, -111.75) * mm});
            skLineSegment(sketch, "E55.22.0.18", {"start": v(132.34, -99.87) * mm, "end": v(132.34, -93) * mm});
            skLineSegment(sketch, "E55.22.0.19", {"start": v(132.74, -99.87) * mm, "end": v(132.74, -93) * mm});
            skLineSegment(sketch, "E55.22.0.20", {"start": v(132.34, -176.12) * mm, "end": v(132.74, -176.12) * mm});
            skLineSegment(sketch, "E55.22.0.21", {"start": v(132.34, -171.12) * mm, "end": v(132.74, -171.12) * mm});
            skLineSegment(sketch, "E55.22.0.22", {"start": v(129.44, -164.25) * mm, "end": v(129.84, -164.25) * mm});
            skLineSegment(sketch, "E55.22.0.23", {"start": v(129.44, -159.25) * mm, "end": v(129.84, -159.25) * mm});
            skLineSegment(sketch, "E55.22.0.24", {"start": v(132.34, -152.37) * mm, "end": v(132.74, -152.37) * mm});
            skLineSegment(sketch, "E55.22.0.25", {"start": v(132.34, -147.37) * mm, "end": v(132.74, -147.37) * mm});
            skLineSegment(sketch, "E55.22.0.26", {"start": v(129.44, -140.5) * mm, "end": v(129.84, -140.5) * mm});
            skLineSegment(sketch, "E55.22.0.27", {"start": v(129.44, -135.5) * mm, "end": v(129.84, -135.5) * mm});
            skLineSegment(sketch, "E55.22.0.28", {"start": v(132.34, -128.62) * mm, "end": v(132.74, -128.62) * mm});
            skLineSegment(sketch, "E55.22.0.29", {"start": v(132.34, -123.62) * mm, "end": v(132.74, -123.62) * mm});
            skLineSegment(sketch, "E55.22.0.30", {"start": v(129.44, -116.75) * mm, "end": v(129.84, -116.75) * mm});
            skLineSegment(sketch, "E55.22.0.31", {"start": v(129.44, -111.75) * mm, "end": v(129.84, -111.75) * mm});
            skLineSegment(sketch, "E55.22.0.32", {"start": v(132.34, -104.87) * mm, "end": v(132.74, -104.87) * mm});
            skLineSegment(sketch, "E55.22.0.33", {"start": v(132.34, -99.87) * mm, "end": v(132.74, -99.87) * mm});
            skLineSegment(sketch, "E55.22.0.34", {"start": v(132.34, -183) * mm, "end": v(132.74, -183) * mm});
            skLineSegment(sketch, "E55.22.0.35", {"start": v(129.44, -183) * mm, "end": v(129.84, -183) * mm});
            skLineSegment(sketch, "E55.22.0.36", {"start": v(132.74, -183) * mm, "end": v(129.44, -183) * mm, "construction": true});
            skLineSegment(sketch, "E55.22.0.37", {"start": v(129.44, -93) * mm, "end": v(129.84, -93) * mm});
            skLineSegment(sketch, "E55.22.0.38", {"start": v(132.74, -93) * mm, "end": v(129.44, -93) * mm, "construction": true});
            skLineSegment(sketch, "E55.22.0.39", {"start": v(132.34, -93) * mm, "end": v(132.74, -93) * mm});
            skLineSegment(sketch, "E55.direction1", {"start": v(2.5, -183) * mm, "end": v(8.27, -183) * mm, "construction": true});
            skSolve(sketch);
        }
        {
            var Q0;
            Q0 = qSketchRegion(id + "F4", true);
            extrude(context, id + "F5", {"entities" : qUnion([Q0]), "operationType" : NewBodyOperationType.REMOVE, "oppositeDirection" : true, "depth" : 25 * mm});
        }
        {
            var Q0;
            Q0=sQuery(id+"F0.wireOp",VERTEX,"E4.bottom.start");
            var Q1;
            Q1=sQuery(id+"F0.wireOp",VERTEX,"E4.bottom.end");
            var Q2;
            Q2=sQuery(id+"F0.wireOp",VERTEX,"E4.left.end");
            var Q3;
            Q3=sQuery(id+"F0.wireOp",VERTEX,"E4.top.end");
            var Q4;
            Q4=sQuery(id+"F0.wireOp",VERTEX,"E5.bottom.start");
            var Q5;
            Q5=sQuery(id+"F0.wireOp",VERTEX,"E5.left.end");
            var Q6;
            Q6=sQuery(id+"F0.wireOp",VERTEX,"E5.right.start");
            var Q7;
            Q7=sQuery(id+"F0.wireOp",VERTEX,"E5.top.end");
            var Q8;
            Q8=sQuery(id+"F0.wireOp",VERTEX,"E13.MirrorCS.end");
            var Q9;
            Q9=sQuery(id+"F0.wireOp",VERTEX,"E13.MirrorCS.start");
            var Q10;
            Q10=sQuery(id+"F0.wireOp",VERTEX,"E14.MirrorCS.end");
            var Q11;
            Q11=sQuery(id+"F0.wireOp",VERTEX,"E15.MirrorCS.end");
            var Q12;
            Q12=makeQuery(id+"F1.opExtrude","SWEPT_BODY",BODY,{"disambiguationData":[OSD([sQuery(id+"F0.wireOp",EDGE,"E1.bottom"),sQuery(id+"F0.wireOp",EDGE,"E1.top"),sQuery(id+"F0.wireOp",EDGE,"E1.left"),sQuery(id+"F0.wireOp",EDGE,"E1.right")])]});
            var Q13;
            Q13=makeQuery(id+"F1.opExtrude","SWEPT_BODY",BODY,{"disambiguationData":[OSD([sQuery(id+"F0.wireOp",EDGE,"E2.bottom"),sQuery(id+"F0.wireOp",EDGE,"E2.top"),sQuery(id+"F0.wireOp",EDGE,"E2.left"),sQuery(id+"F0.wireOp",EDGE,"E2.right")])]});
            var Q14;
            Q14=makeQuery(id+"F1.opExtrude","SWEPT_BODY",BODY,{"disambiguationData":[OSD([sQuery(id+"F0.wireOp",EDGE,"E9.MirrorCS"),sQuery(id+"F0.wireOp",EDGE,"E10.MirrorCS"),sQuery(id+"F0.wireOp",EDGE,"E11.MirrorCS"),sQuery(id+"F0.wireOp",EDGE,"E12.MirrorCS")])]});
            hole(context, id + "F6", {"style" : HoleStyle.SIMPLE, "holeDiameter" : 3.5 * mm, "endStyle" : HoleEndStyle.THROUGH, "oppositeDirection" : true, "locations" : qUnion([Q0, Q1, Q2, Q3, Q4, Q5, Q6, Q7, Q8, Q9, Q10, Q11]), "scope" : qUnion([Q12, Q13, Q14])});
        }
        {
            var Q0;
            {var subQ2=sQuery(id+"F0.wireOp",EDGE,"E1.left");var subQ75=makeQuery(id+"F1.opExtrude","CAP_EDGE",EDGE,{"disambiguationData":[OSD([subQ2])],"isStart":false});Q0=makeQuery(id+"F2.imprint","IMPRINT",FACE,{"disambiguationData":[TD([[makeQuery(id+"F2.imprint","IMPRINT",EDGE,{"derivedFrom":subQ75}),1.0]])]});}
            var sketch = newSketch(context, id + "F7", { "sketchPlane" : qUnion([Q0])});
            skLineSegment(sketch, "E56.0", {"start": v(280.9, -138) * mm, "end": v(0, -138) * mm, "construction": true});
            skLineSegment(sketch, "E57.rect.bottom", {"start": v(127.4, -107) * mm, "end": v(4.9, -107) * mm, "construction": true});
            skLineSegment(sketch, "E57.rect.top", {"start": v(127.4, -169) * mm, "end": v(4.9, -169) * mm, "construction": true});
            skLineSegment(sketch, "E57.rect.left", {"start": v(127.4, -107) * mm, "end": v(127.4, -169) * mm, "construction": true});
            skLineSegment(sketch, "E57.rect.right", {"start": v(4.9, -107) * mm, "end": v(4.9, -169) * mm, "construction": true});
            skPoint(sketch, "E57.rect.middle", {"position": v(66.15, -138) * mm});
            skLineSegment(sketch, "E58.0", {"start": v(208.1, -93) * mm, "end": v(208.1, -183) * mm, "construction": true});
            skLineSegment(sketch, "E59.rect.bottom", {"start": v(276, -107) * mm, "end": v(140.2, -107) * mm, "construction": true});
            skLineSegment(sketch, "E59.rect.top", {"start": v(276, -169) * mm, "end": v(140.2, -169) * mm, "construction": true});
            skLineSegment(sketch, "E59.rect.left", {"start": v(276, -107) * mm, "end": v(276, -169) * mm, "construction": true});
            skLineSegment(sketch, "E59.rect.right", {"start": v(140.2, -107) * mm, "end": v(140.2, -169) * mm, "construction": true});
            skPoint(sketch, "E59.rect.middle", {"position": v(208.1, -138) * mm});
            skLineSegment(sketch, "E60.MirrorCS", {"start": v(288.8, -107) * mm, "end": v(288.8, -169) * mm, "construction": true});
            skLineSegment(sketch, "E61.MirrorCS", {"start": v(424.6, -107) * mm, "end": v(424.6, -169) * mm, "construction": true});
            skLineSegment(sketch, "E62.MirrorCS", {"start": v(288.8, -107) * mm, "end": v(424.6, -107) * mm, "construction": true});
            skLineSegment(sketch, "E63.MirrorCS", {"start": v(288.8, -169) * mm, "end": v(424.6, -169) * mm, "construction": true});
            skLineSegment(sketch, "E64.0", {"start": v(66.15, -93) * mm, "end": v(66.15, -183) * mm, "construction": true});
            skPoint(sketch, "E65", {"position": v(66.15, -107) * mm});
            skPoint(sketch, "E66", {"position": v(66.15, -169) * mm});
            skPoint(sketch, "E67", {"position": v(208.1, -107) * mm});
            skPoint(sketch, "E68", {"position": v(208.1, -169) * mm});
            skPoint(sketch, "E69", {"position": v(356.7, -169) * mm});
            skPoint(sketch, "E70", {"position": v(356.7, -107) * mm});
            skSolve(sketch);
        }
        {
            var Q0;
            Q0=sQuery(id+"F7.wireOp",VERTEX,"E57.rect.bottom.end");
            var Q1;
            Q1=sQuery(id+"F7.wireOp",VERTEX,"E57.rect.top.end");
            var Q2;
            Q2=sQuery(id+"F7.wireOp",VERTEX,"E57.rect.bottom.start");
            var Q3;
            Q3=sQuery(id+"F7.wireOp",VERTEX,"E57.rect.top.start");
            var Q4;
            Q4=sQuery(id+"F7.wireOp",VERTEX,"E59.rect.bottom.end");
            var Q5;
            Q5=sQuery(id+"F7.wireOp",VERTEX,"E59.rect.top.end");
            var Q6;
            Q6=sQuery(id+"F7.wireOp",VERTEX,"E59.rect.top.start");
            var Q7;
            Q7=sQuery(id+"F7.wireOp",VERTEX,"E59.rect.bottom.start");
            var Q8;
            Q8=sQuery(id+"F7.wireOp",VERTEX,"E60.MirrorCS.start");
            var Q9;
            Q9=sQuery(id+"F7.wireOp",VERTEX,"E60.MirrorCS.end");
            var Q10;
            Q10=sQuery(id+"F7.wireOp",VERTEX,"E61.MirrorCS.start");
            var Q11;
            Q11=sQuery(id+"F7.wireOp",VERTEX,"E63.MirrorCS.end");
            var Q12;
            Q12=sQuery(id+"F7.wireOp",VERTEX,"E65");
            var Q13;
            Q13=sQuery(id+"F7.wireOp",VERTEX,"E66");
            var Q14;
            Q14=sQuery(id+"F7.wireOp",VERTEX,"E67");
            var Q15;
            Q15=sQuery(id+"F7.wireOp",VERTEX,"E68");
            var Q16;
            Q16=sQuery(id+"F7.wireOp",VERTEX,"E70");
            var Q17;
            Q17=sQuery(id+"F7.wireOp",VERTEX,"E69");
            var Q18;
            Q18=makeQuery(id+"F1.opExtrude","SWEPT_BODY",BODY,{"disambiguationData":[OSD([sQuery(id+"F0.wireOp",EDGE,"E1.bottom"),sQuery(id+"F0.wireOp",EDGE,"E1.top"),sQuery(id+"F0.wireOp",EDGE,"E1.left"),sQuery(id+"F0.wireOp",EDGE,"E1.right")])]});
            var Q19;
            Q19=makeQuery(id+"F1.opExtrude","SWEPT_BODY",BODY,{"disambiguationData":[OSD([sQuery(id+"F0.wireOp",EDGE,"E2.bottom"),sQuery(id+"F0.wireOp",EDGE,"E2.top"),sQuery(id+"F0.wireOp",EDGE,"E2.left"),sQuery(id+"F0.wireOp",EDGE,"E2.right")])]});
            var Q20;
            Q20=makeQuery(id+"F1.opExtrude","SWEPT_BODY",BODY,{"disambiguationData":[OSD([sQuery(id+"F0.wireOp",EDGE,"E9.MirrorCS"),sQuery(id+"F0.wireOp",EDGE,"E10.MirrorCS"),sQuery(id+"F0.wireOp",EDGE,"E11.MirrorCS"),sQuery(id+"F0.wireOp",EDGE,"E12.MirrorCS")])]});
            hole(context, id + "F8", {"style" : HoleStyle.SIMPLE, "holeDiameter" : 3.5 * mm, "endStyle" : HoleEndStyle.THROUGH, "locations" : qUnion([Q0, Q1, Q2, Q3, Q4, Q5, Q6, Q7, Q8, Q9, Q10, Q11, Q12, Q13, Q14, Q15, Q16, Q17]), "scope" : qUnion([Q18, Q19, Q20])});
        }
    });
